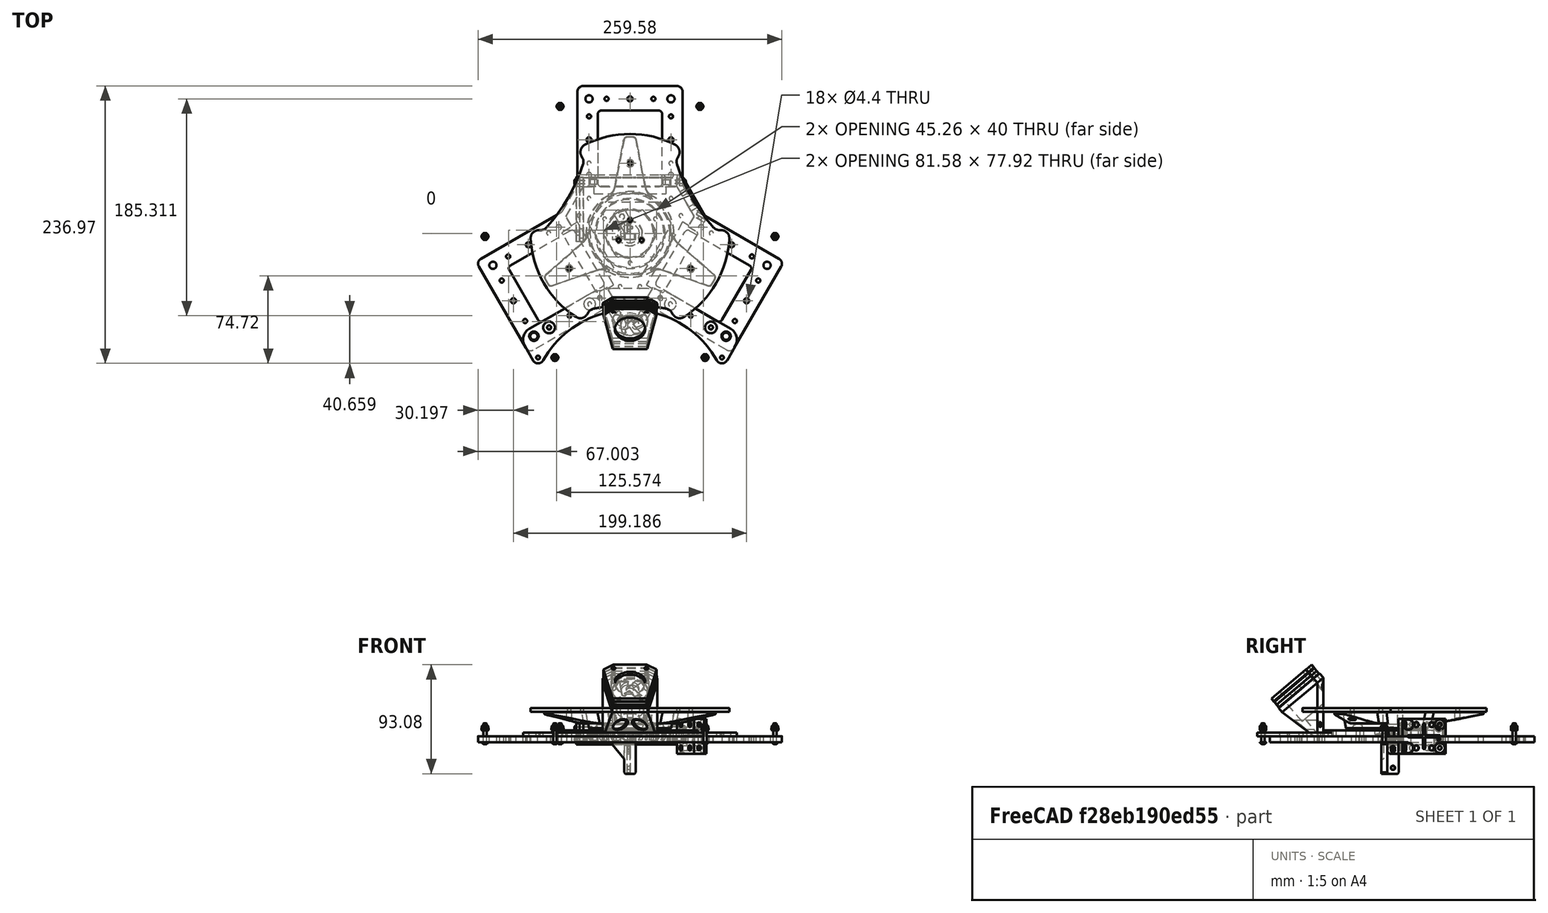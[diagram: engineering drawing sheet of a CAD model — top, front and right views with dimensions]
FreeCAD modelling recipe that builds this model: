
FCSTD DOCUMENT  (FreeCAD 2024.113R14555 (Git shallow))
Label: structures
License: Creative Commons Attribution-NoDerivatives
LicenseURL: http://creativecommons.org/licenses/by-nd/4.0/
objects: Sketcher::SketchObject×49, PartDesign::Pad×28, PartDesign::Pocket×26, PartDesign::Chamfer×25, PartDesign::Fillet×22, PartDesign::Body×20, App::Link×19, Part::FeaturePython×16, TechDraw::DrawProjGroupItem×14, TechDraw::DrawProjGroup×14, App::Part×12, TechDraw::DrawSVGTemplate×10, TechDraw::DrawPage×10, PartDesign::Mirrored×8, PartDesign::SubShapeBinder×7, PartDesign::PolarPattern×6, App::DocumentObjectGroup×6, TechDraw::DrawViewDimension×5, Part::SubShapeBinder×3, Part::Mirroring×2, +8 more types
note: 521 computed .brp shape members not serialized (recipe doc carries the construction recipe); baked Part::Feature solids carry a one-line shape summary decoded from their .brp
EXTERNAL_REF file=generic-hardware.FCStd obj=Part035
EXTERNAL_REF file=generic-hardware.FCStd obj=Part036
EXTERNAL_REF file=../robot_holonome.FCStd obj=Part

FEATURE [Sketcher::SketchObject] Sketch032
  ArcFitTolerance = 0
  AttachmentSupport = -> [XY_Plane026]
  ExternalBSplineMaxDegree = 0
  ExternalBSplineTolerance = 0
  FullyConstrained = true
  InternalTolerance = 1e-06
  InvalidShape = false
  MakeInternals = false
  MapMode = 5
  Support = -> [XY_Plane026]
  TreeRank = 0
  ValidateShape = true
  sketch-geometry (56):
    g0: LineSegment StartX=-131.619 StartY=-24.0289 StartZ=0 EndX=-58.007 EndY=18.4711 EndZ=0
    g1: LineSegment StartX=-58.007 StartY=18.4711 StartZ=0 EndX=-45 EndY=41 EndZ=0
    g2: LineSegment StartX=-45 StartY=41 StartZ=0 EndX=-45 EndY=126 EndZ=0
    g3: LineSegment StartX=-45 StartY=126 StartZ=0 EndX=45 EndY=126 EndZ=0
    g4: LineSegment StartX=45 StartY=126 StartZ=0 EndX=45 EndY=41 EndZ=0
    g5: LineSegment StartX=45 StartY=41 StartZ=0 EndX=58.007 EndY=18.4711 EndZ=0
    g6: LineSegment StartX=58.007 StartY=18.4711 StartZ=0 EndX=131.619 EndY=-24.0289 EndZ=0
    g7: LineSegment StartX=131.619 StartY=-24.0289 StartZ=0 EndX=86.6192 EndY=-101.971 EndZ=0
    g8: LineSegment StartX=86.6192 StartY=-101.971 StartZ=0 EndX=13.007 EndY=-59.4711 EndZ=0
    g9: LineSegment StartX=13.007 StartY=-59.4711 StartZ=0 EndX=-13.007 EndY=-59.4711 EndZ=0
    g10: LineSegment StartX=-13.007 StartY=-59.4711 StartZ=0 EndX=-86.6192 EndY=-101.971 EndZ=0
    g11: LineSegment StartX=-86.6192 StartY=-101.971 StartZ=0 EndX=-131.619 EndY=-24.0289 EndZ=0
    g12: LineSegment [constr] StartX=-1e-16 StartY=1e-16 StartZ=0 EndX=-1e-16 EndY=126 EndZ=0
    g13: LineSegment [constr] StartX=-1e-16 StartY=1e-16 StartZ=0 EndX=-109.119 EndY=-63 EndZ=0
    g14: LineSegment [constr] StartX=-1e-16 StartY=1e-16 StartZ=0 EndX=109.119 EndY=-63 EndZ=0
    g15: LineSegment StartX=-27.5 StartY=40 StartZ=0 EndX=27.5 EndY=40 EndZ=0
    g16: LineSegment StartX=27.5 StartY=40 StartZ=0 EndX=27.5 EndY=105 EndZ=0
    g17: LineSegment StartX=27.5 StartY=105 StartZ=0 EndX=-27.5 EndY=105 EndZ=0
    g18: LineSegment StartX=-27.5 StartY=105 StartZ=0 EndX=-27.5 EndY=40 EndZ=0
    g19: LineSegment StartX=20.891 StartY=-43.8157 StartZ=0 EndX=48.391 EndY=3.8157 EndZ=0
    g20: LineSegment StartX=48.391 StartY=3.8157 StartZ=0 EndX=104.683 EndY=-28.6843 EndZ=0
    g21: LineSegment StartX=104.683 StartY=-28.6843 StartZ=0 EndX=77.1827 EndY=-76.3157 EndZ=0
    g22: LineSegment StartX=77.1827 StartY=-76.3157 StartZ=0 EndX=20.891 EndY=-43.8157 EndZ=0
    g23: LineSegment StartX=-104.683 StartY=-28.6843 StartZ=0 EndX=-77.1827 EndY=-76.3157 EndZ=0
    g24: LineSegment StartX=-77.1827 StartY=-76.3157 StartZ=0 EndX=-20.891 EndY=-43.8157 EndZ=0
    g25: LineSegment StartX=-20.891 StartY=-43.8157 StartZ=0 EndX=-48.391 EndY=3.8157 EndZ=0
    g26: LineSegment StartX=-48.391 StartY=3.8157 StartZ=0 EndX=-104.683 EndY=-28.6843 EndZ=0
    g27: Circle [constr] CenterX=-1e-16 CenterY=1e-16 CenterZ=0 NormalX=0 NormalY=0 NormalZ=1 AngleXU=0 Radius=48.5412
    g28: LineSegment StartX=-11.547 StartY=-20 StartZ=0 EndX=-23.094 EndY=0 EndZ=0
    g29: LineSegment StartX=-23.094 StartY=-1.3e-15 StartZ=0 EndX=-11.547 EndY=20 EndZ=0
    g30: LineSegment StartX=-11.547 StartY=20 StartZ=0 EndX=11.547 EndY=20 EndZ=0
    g31: LineSegment StartX=11.547 StartY=20 StartZ=0 EndX=23.094 EndY=0 EndZ=0
    g32: LineSegment StartX=23.094 StartY=9e-16 StartZ=0 EndX=11.547 EndY=-20 EndZ=0
    g33: LineSegment StartX=11.547 StartY=-20 StartZ=0 EndX=-11.547 EndY=-20 EndZ=0
    g34: Circle [constr] CenterX=-1e-16 CenterY=1e-16 CenterZ=0 NormalX=0 NormalY=0 NormalZ=1 AngleXU=0 Radius=23.094
    g35: Circle CenterX=-21.6506 CenterY=12.5 CenterZ=0 NormalX=0 NormalY=0 NormalZ=1 AngleXU=0 Radius=1.6
    g36: Circle CenterX=21.6506 CenterY=12.5 CenterZ=0 NormalX=0 NormalY=0 NormalZ=1 AngleXU=0 Radius=1.6
    g37: Circle CenterX=0 CenterY=-25 CenterZ=0 NormalX=0 NormalY=0 NormalZ=1 AngleXU=0 Radius=1.6
    g38: LineSegment [constr] StartX=0 StartY=-25 StartZ=0 EndX=-1e-16 EndY=0 EndZ=0
    g39: LineSegment [constr] StartX=-1e-16 StartY=1e-16 StartZ=0 EndX=21.6506 EndY=12.5 EndZ=0
    g40: LineSegment [constr] StartX=-1e-16 StartY=1e-16 StartZ=0 EndX=-21.6506 EndY=12.5 EndZ=0
    g41: LineSegment [constr] StartX=-45 StartY=126 StartZ=0 EndX=-131.619 EndY=-24.0289 EndZ=0
    g42: LineSegment [constr] StartX=-86.6192 StartY=-101.971 StartZ=0 EndX=86.6192 EndY=-101.971 EndZ=0
    g43: LineSegment [constr] StartX=131.619 StartY=-24.0289 StartZ=0 EndX=45 EndY=126 EndZ=0
    g44: LineSegment [constr] StartX=-45 StartY=126 StartZ=0 EndX=-55 EndY=108.679 EndZ=0
    g45: LineSegment [constr] StartX=-55 StartY=108.679 StartZ=0 EndX=-45 EndY=41 EndZ=0
    g46: LineSegment [constr] StartX=-58.007 StartY=18.4711 StartZ=0 EndX=-121.619 EndY=-6.70835 EndZ=0
    g47: LineSegment [constr] StartX=-121.619 StartY=-6.70835 StartZ=0 EndX=-131.619 EndY=-24.0289 EndZ=0
    g48: LineSegment [constr] StartX=-86.6192 StartY=-101.971 StartZ=0 EndX=-66.6192 EndY=-101.971 EndZ=0
    g49: LineSegment [constr] StartX=-66.6192 StartY=-101.971 StartZ=0 EndX=-13.007 EndY=-59.4711 EndZ=0
    g50: LineSegment [constr] StartX=13.007 StartY=-59.4711 StartZ=0 EndX=66.6192 EndY=-101.971 EndZ=0
    g51: LineSegment [constr] StartX=66.6192 StartY=-101.971 StartZ=0 EndX=86.6192 EndY=-101.971 EndZ=0
    g52: LineSegment [constr] StartX=131.619 StartY=-24.0289 StartZ=0 EndX=121.619 EndY=-6.70835 EndZ=0
    g53: LineSegment [constr] StartX=121.619 StartY=-6.70835 StartZ=0 EndX=58.007 EndY=18.4711 EndZ=0
    g54: LineSegment [constr] StartX=45 StartY=41 StartZ=0 EndX=55 EndY=108.679 EndZ=0
    g55: LineSegment [constr] StartX=55 StartY=108.679 StartZ=0 EndX=45 EndY=126 EndZ=0
  constraints (151):
    c: Coincident(g0,g1)
    c: Coincident(g1,g2)
    c: Vertical(g2)
    c: Coincident(g2,g3)
    c: Horizontal(g3)
    c: Coincident(g3,g4)
    c: Vertical(g4)
    c: Coincident(g4,g5)
    c: Coincident(g5,g6)
    c: Coincident(g6,g7)
    c: Coincident(g7,g8)
    c: Coincident(g8,g9)
    c: Horizontal(g9)
    c: Coincident(g9,g10)
    c: Coincident(g10,g11)
    c: Coincident(g11,g0)
    c: Parallel(g8,g6)
    c: Parallel(g10,g0)
    c: Equal(g4,g6)
    c: Equal(g6,g8)
    c: Equal(g8,g10)
    c: Equal(g10,g0)
    c: Equal(g0,g2)
    c: Perpendicular(g6,g7)
    c: Perpendicular(g11,g10)
    c: Coincident(g12,g-1)
    c: PointOnObject(g12,g3)
    c: Vertical(g12)
    c: Coincident(g13,g12)
    c: Coincident(g14,g12)
    c: Symmetric(g6,g7,g14)
    c: Symmetric(g10,g0,g13)
    c: Perpendicular(g13,g11)
    c: Perpendicular(g7,g14)
    c: DistanceX(g3,g3) = 90
    c: Equal(g9,g5)
    c: Equal(g5,g1)
    c: Angle(g14,g12) = 2.0944
    c: Angle(g12,g13) = 2.0944
    c: DistanceY(g12,g2) = 126
    c: DistanceX(g9,g9) = 26.0141
    c: Coincident(g15,g16)
    c: Coincident(g16,g17)
    c: Coincident(g17,g18)
    c: Coincident(g18,g15)
    c: Horizontal(g15)
    c: Vertical(g16)
    c: Vertical(g18)
    c: Symmetric(g16,g17,g12)
    c: DistanceX(g17,g17) = 55
    c: DistanceY(g16,g16) = 65
    c: Coincident(g19,g20)
    c: Coincident(g20,g21)
    c: Coincident(g21,g22)
    c: Coincident(g22,g19)
    c: Coincident(g23,g24)
    c: Coincident(g24,g25)
    c: Coincident(g25,g26)
    c: Coincident(g26,g23)
    c: Equal(g25,g23)
    c: Equal(g23,g19)
    c: Equal(g19,g21)
    c: Equal(g21,g15)
    c: Equal(g22,g20)
    c: Equal(g20,g16)
    c: Equal(g16,g26)
    c: Equal(g26,g24)
    c: Parallel(g24,g13)
    c: Parallel(g22,g14)
    c: Symmetric(g23,g23,g13)
    c: Symmetric(g21,g20,g14)
    c: Coincident(g27,g12)
    c: PointOnObject(g19,g27)
    c: PointOnObject(g24,g27)
    c: PointOnObject(g15,g27)
    c: Equal(g11,g7)
    c: Equal(g7,g3)
    c: Coincident(g28,g29)
    c: Coincident(g29,g30)
    c: Coincident(g30,g31)
    c: Coincident(g31,g32)
    c: Coincident(g32,g33)
    c: Coincident(g33,g28)
    c: Horizontal(g33)
    c: Horizontal(g30)
    c: Equal(g29,g30)
    c: Equal(g30,g31)
    c: Equal(g31,g32)
    c: Equal(g32,g33)
    c: Equal(g33,g28)
    c: Coincident(g34,g12)
    c: PointOnObject(g30,g34)
    c: PointOnObject(g31,g34)
    c: PointOnObject(g32,g34)
    c: PointOnObject(g28,g34)
    c: PointOnObject(g28,g34)
    c: DistanceY(g12,g30) = 20
    c: PointOnObject(g37,g-2)
    c: Equal(g37,g36)
    c: Equal(g36,g35)
    c: Diameter(g35) = 3.2
    c: Coincident(g38,g37)
    c: Coincident(g38,g12)
    c: Coincident(g39,g12)
    c: Coincident(g39,g36)
    c: Coincident(g40,g12)
    c: Coincident(g40,g35)
    c: Perpendicular(g29,g40)
    c: Perpendicular(g31,g39)
    c: Equal(g40,g38)
    c: Equal(g38,g39)
    c: DistanceY(g38,g38) = 25
    c: Coincident(g41,g3)
    c: Coincident(g41,g11)
    c: Coincident(g42,g11)
    c: Coincident(g42,g7)
    c: Coincident(g43,g7)
    c: Coincident(g43,g3)
    c: Coincident(g3,g44)
    c: PointOnObject(g44,g41)
    c: Coincident(g44,g45)
    c: Coincident(g45,g1)
    c: Coincident(g1,g46)
    c: PointOnObject(g46,g41)
    c: Coincident(g46,g47)
    c: Coincident(g47,g11)
    c: Coincident(g11,g48)
    c: Horizontal(g48)
    c: Coincident(g48,g49)
    c: Coincident(g49,g9)
    c: Coincident(g9,g50)
    c: PointOnObject(g50,g42)
    c: Coincident(g50,g51)
    c: Coincident(g51,g7)
    c: Coincident(g7,g52)
    c: PointOnObject(g52,g43)
    c: Coincident(g52,g53)
    c: Coincident(g53,g5)
    c: Coincident(g5,g54)
    c: PointOnObject(g54,g43)
    c: Coincident(g54,g55)
    c: Coincident(g55,g3)
    c: Equal(g55,g44)
    c: Equal(g44,g47)
    c: Equal(g47,g48)
    c: Equal(g48,g51)
    c: Equal(g55,g52)
    c: DistanceX(g48,g48) = 20
    c: DistanceY(g16) = 105
    c: DistanceY(g50,g12) = 101.971
    c: DistanceY(g4,g4) = 85
FEATURE [PartDesign::Pad] Pad020
  AddSubType = 0
  AutoTaperInnerAngle = false
  CheckUpToFaceLimits = true
  ClaimChildren = false
  Direction = (0,0,1)
  Fit = 0
  FitJoin = 0
  InnerFit = 0
  InnerFitJoin = 0
  InvalidShape = false
  Length = 5
  Length2 = 100
  Linearize = true
  NewSolid = false
  Profile = -> Sketch032
  Refine = true
  Reversed = true
  Suppress = false
  TaperInnerAngle = 0
  TaperInnerAngleRev = 0
  TreeRank = 0
  Type = 0
  ValidateShape = true
  _ProfileBasedVersion = 1
FEATURE [PartDesign::Fillet] Fillet008
  AddSubType = 0
  Base = -> Pad020 [Edge41,Edge44,Edge37,Edge38,Edge65,Edge62,Edge61,Edge68,Edge49,Edge50,Edge53,Edge56]
  BaseFeature = -> Pad020
  InvalidShape = false
  NewSolid = false
  Radius = 3
  Refine = true
  SupportTransform = false
  Suppress = false
  TreeRank = 0
  UseAllEdges = false
  ValidateShape = true
FEATURE [PartDesign::Fillet] Fillet009
  AddSubType = 0
  Base = -> Fillet008 [Edge110,Edge99,Edge107,Edge106,Edge102,Edge103]
  BaseFeature = -> Fillet008
  InvalidShape = false
  NewSolid = false
  Radius = 5
  Refine = true
  SupportTransform = false
  Suppress = false
  TreeRank = 0
  UseAllEdges = false
  ValidateShape = true
FEATURE [PartDesign::Fillet] Fillet010
  AddSubType = 0
  Base = -> Fillet009 [Edge53,Edge57,Edge67,Edge71,Edge77,Edge81]
  BaseFeature = -> Fillet009
  InvalidShape = false
  NewSolid = false
  Radius = 5
  Refine = true
  SupportTransform = false
  Suppress = false
  TreeRank = 0
  UseAllEdges = false
  ValidateShape = true
FEATURE [Sketcher::SketchObject] Sketch033
  ArcFitTolerance = 0
  AttachmentSupport = -> [XY_Plane026]
  ExternalBSplineMaxDegree = 0
  ExternalBSplineTolerance = 0
  FullyConstrained = true
  InternalTolerance = 1e-06
  InvalidShape = false
  MakeInternals = false
  MapMode = 5
  Support = -> [XY_Plane026]
  TreeRank = 0
  ValidateShape = true
  sketch-geometry (13):
    g0: Circle CenterX=-20 CenterY=115 CenterZ=0 NormalX=0 NormalY=0 NormalZ=1 AngleXU=0 Radius=1.75
    g1: Circle CenterX=20 CenterY=115 CenterZ=0 NormalX=0 NormalY=0 NormalZ=1 AngleXU=0 Radius=1.75
    g2: Circle CenterX=-35 CenterY=60 CenterZ=0 NormalX=0 NormalY=0 NormalZ=1 AngleXU=0 Radius=1.75
    g3: Circle CenterX=-35 CenterY=100 CenterZ=0 NormalX=0 NormalY=0 NormalZ=1 AngleXU=0 Radius=1.75
    g4: Circle CenterX=35 CenterY=100 CenterZ=0 NormalX=0 NormalY=0 NormalZ=1 AngleXU=0 Radius=1.75
    g5: Circle CenterX=35 CenterY=60 CenterZ=0 NormalX=0 NormalY=0 NormalZ=1 AngleXU=0 Radius=1.75
    g6: Circle CenterX=-35 CenterY=115 CenterZ=0 NormalX=0 NormalY=0 NormalZ=1 AngleXU=0 Radius=3.1
    g7: Circle CenterX=35 CenterY=115 CenterZ=0 NormalX=0 NormalY=0 NormalZ=1 AngleXU=0 Radius=3.1
    g8: Circle CenterX=-35 CenterY=80 CenterZ=0 NormalX=0 NormalY=0 NormalZ=1 AngleXU=0 Radius=2.2
    g9: Circle CenterX=35 CenterY=80 CenterZ=0 NormalX=0 NormalY=0 NormalZ=1 AngleXU=0 Radius=2.2
    g10: Circle CenterX=-35 CenterY=50 CenterZ=0 NormalX=0 NormalY=0 NormalZ=1 AngleXU=0 Radius=2.2
    g11: Circle CenterX=35 CenterY=50 CenterZ=0 NormalX=0 NormalY=0 NormalZ=1 AngleXU=0 Radius=2.2
    g12: Circle CenterX=-1.0206e-12 CenterY=115 CenterZ=0 NormalX=0 NormalY=0 NormalZ=1 AngleXU=0 Radius=2.2
  constraints (31):
    c: Equal(g0,g3)
    c: Equal(g3,g2)
    c: Equal(g2,g1)
    c: Equal(g1,g4)
    c: Equal(g4,g5)
    c: Diameter(g0) = 3.5
    c: Symmetric(g1,g0,g-2)
    c: Symmetric(g3,g4,g-2)
    c: Symmetric(g2,g5,g-2)
    c: Vertical(g3,g2)
    c: DistanceX(g3,g4) = 70
    c: DistanceX(g0,g1) = 40
    c: DistanceY(g4,g1) = 15
    c: DistanceY(g5,g4) = 40
    c: DistanceY(g-1,g1) = 115
    c: Symmetric(g7,g6,g-2)
    c: Horizontal(g6,g0)
    c: Diameter(g7) = 6.2
    c: Equal(g7,g6)
    c: Vertical(g7,g4)
    c: Equal(g9,g8)
    c: Symmetric(g8,g9,g-2)
    c: Symmetric(g5,g4,g9)
    c: Diameter(g9) = 4.4
    c: Symmetric(g1,g0,g12)
    c: Equal(g12,g11)
    c: Equal(g11,g10)
    c: Equal(g10,g9)
    c: Vertical(g11,g5)
    c: Symmetric(g11,g10,g-2)
    c: DistanceY(g11,g5) = 10
FEATURE [PartDesign::Pocket] Pocket012
  AddSubType = 1
  AutoTaperInnerAngle = false
  BaseFeature = -> Fillet010
  CheckUpToFaceLimits = true
  ClaimChildren = false
  Direction = (1,1,1)
  Fit = 0
  FitJoin = 0
  InnerFit = 0
  InnerFitJoin = 0
  InvalidShape = false
  Length = 5
  Length2 = 100
  Linearize = true
  NewSolid = false
  Profile = -> Sketch033
  Refine = true
  Suppress = false
  TaperInnerAngle = 0
  TaperInnerAngleRev = 0
  TreeRank = 0
  Type = 1
  ValidateShape = true
  _ProfileBasedVersion = 1
  _Version = 0
FEATURE [PartDesign::PolarPattern] PolarPattern013
  AddSubType = 0
  Angle = 360
  Axis = -> Sketch033 [N_Axis]
  BaseFeature = -> Pocket012
  CopyShape = false
  InvalidShape = false
  NewSolid = false
  Occurrences = 3
  OriginalSubs = -> [Pocket012]
  Originals = -> [Pocket012]
  ParallelTransform = true
  Refine = true
  SubTransform = true
  Suppress = false
  TreeRank = 0
  ValidateShape = true
  _Version = 0
FEATURE [PartDesign::Fillet] Fillet011
  AddSubType = 0
  Base = -> PolarPattern013 [Edge190,Edge189,Edge192,Edge196,Edge198,Edge194]
  BaseFeature = -> PolarPattern013
  InvalidShape = false
  NewSolid = false
  Radius = 3
  Refine = true
  SupportTransform = false
  Suppress = false
  TreeRank = 0
  UseAllEdges = false
  ValidateShape = true
FEATURE [PartDesign::Body] Body019  label="Semelle"
  AutoGroupSolids = false
  ClaimAllChildren = false
  ExportMode = 0
  Group = -> [Sketch032,Pad020,Fillet008,Fillet009,Fillet010,Sketch033,Pocket012,PolarPattern013,Fillet011]
  InvalidShape = false
  Origin = -> Origin029
  SingleSolid = true
  Tip = -> Fillet011
  TreeRank = 0
  ValidateShape = true
  _ExportChildren = -> [Pad020,Fillet008,Fillet009,Fillet010,Pocket012,PolarPattern013,Fillet011]
  _GroupVersion = 1
FEATURE [Sketcher::SketchObject] Sketch034
  ArcFitTolerance = 0
  AttachmentSupport = -> [XY_Plane027]
  ExternalBSplineMaxDegree = 0
  ExternalBSplineTolerance = 0
  FullyConstrained = true
  InternalTolerance = 1e-06
  InvalidShape = false
  MakeInternals = false
  MapMode = 5
  Support = -> [XY_Plane027]
  TreeRank = 0
  ValidateShape = true
  sketch-geometry (33):
    g0: LineSegment StartX=-54.641 StartY=14.641 StartZ=0 EndX=-40 EndY=40 EndZ=0
    g1: LineSegment StartX=-40 StartY=40 StartZ=0 EndX=-31 EndY=40 EndZ=0
    g2: LineSegment StartX=-31 StartY=40 StartZ=0 EndX=-31 EndY=34 EndZ=0
    g3: LineSegment StartX=-31 StartY=34 StartZ=0 EndX=31 EndY=34 EndZ=0
    g4: LineSegment StartX=31 StartY=34 StartZ=0 EndX=31 EndY=40 EndZ=0
    g5: LineSegment StartX=31 StartY=40 StartZ=0 EndX=40 EndY=40 EndZ=0
    g6: LineSegment StartX=40 StartY=40 StartZ=0 EndX=54.641 EndY=14.641 EndZ=0
    g7: LineSegment StartX=54.641 StartY=14.641 StartZ=0 EndX=50.141 EndY=6.84679 EndZ=0
    g8: LineSegment StartX=50.141 StartY=6.84679 StartZ=0 EndX=44.9449 EndY=9.84679 EndZ=0
    g9: LineSegment StartX=44.9449 StartY=9.84679 StartZ=0 EndX=13.9449 EndY=-43.8468 EndZ=0
    g10: LineSegment StartX=13.9449 StartY=-43.8468 StartZ=0 EndX=19.141 EndY=-46.8468 EndZ=0
    g11: LineSegment StartX=19.141 StartY=-46.8468 StartZ=0 EndX=14.641 EndY=-54.641 EndZ=0
    g12: LineSegment StartX=14.641 StartY=-54.641 StartZ=0 EndX=-14.641 EndY=-54.641 EndZ=0
    g13: LineSegment StartX=-14.641 StartY=-54.641 StartZ=0 EndX=-19.141 EndY=-46.8468 EndZ=0
    g14: LineSegment StartX=-19.141 StartY=-46.8468 StartZ=0 EndX=-13.9449 EndY=-43.8468 EndZ=0
    g15: LineSegment StartX=-13.9449 StartY=-43.8468 StartZ=0 EndX=-44.9449 EndY=9.84679 EndZ=0
    g16: LineSegment StartX=-44.9449 StartY=9.84679 StartZ=0 EndX=-50.141 EndY=6.84679 EndZ=0
    g17: LineSegment StartX=-50.141 StartY=6.84679 StartZ=0 EndX=-54.641 EndY=14.641 EndZ=0
    g18: Circle [constr] CenterX=0 CenterY=0 CenterZ=0 NormalX=0 NormalY=0 NormalZ=1 AngleXU=0 Radius=56.5685
    g19: Circle [constr] CenterX=0 CenterY=0 CenterZ=0 NormalX=0 NormalY=0 NormalZ=1 AngleXU=0 Radius=25
    g20: Circle CenterX=-21.6506 CenterY=12.5 CenterZ=0 NormalX=0 NormalY=0 NormalZ=1 AngleXU=0 Radius=1.6
    g21: Circle CenterX=21.6506 CenterY=12.5 CenterZ=0 NormalX=0 NormalY=0 NormalZ=1 AngleXU=0 Radius=1.6
    g22: Circle CenterX=0 CenterY=-25 CenterZ=0 NormalX=0 NormalY=0 NormalZ=1 AngleXU=0 Radius=1.6
    g23: LineSegment [constr] StartX=0 StartY=0 StartZ=0 EndX=21.6506 EndY=12.5 EndZ=0
    g24: LineSegment [constr] StartX=0 StartY=0 StartZ=0 EndX=0 EndY=-25 EndZ=0
    g25: LineSegment [constr] StartX=0 StartY=0 StartZ=0 EndX=-21.6506 EndY=12.5 EndZ=0
    g26: LineSegment StartX=11.547 StartY=20 StartZ=0 EndX=-11.547 EndY=20 EndZ=0
    g27: LineSegment StartX=-11.547 StartY=20 StartZ=0 EndX=-23.094 EndY=1.0409e-12 EndZ=0
    g28: LineSegment StartX=-23.094 StartY=1.0409e-12 StartZ=0 EndX=-11.547 EndY=-20 EndZ=0
    g29: LineSegment StartX=-11.547 StartY=-20 StartZ=0 EndX=11.547 EndY=-20 EndZ=0
    g30: LineSegment StartX=11.547 StartY=-20 StartZ=0 EndX=23.094 EndY=1.0374e-12 EndZ=0
    g31: LineSegment StartX=23.094 StartY=1.0374e-12 StartZ=0 EndX=11.547 EndY=20 EndZ=0
    g32: Circle [constr] CenterX=0 CenterY=0 CenterZ=0 NormalX=0 NormalY=0 NormalZ=1 AngleXU=0 Radius=23.094
  constraints (88):
    c: Coincident(g0,g1)
    c: Horizontal(g1)
    c: Coincident(g1,g2)
    c: Vertical(g2)
    c: Coincident(g2,g3)
    c: Coincident(g3,g4)
    c: Vertical(g4)
    c: Coincident(g4,g5)
    c: Horizontal(g5)
    c: Coincident(g5,g6)
    c: Coincident(g6,g7)
    c: Coincident(g7,g8)
    c: Coincident(g8,g9)
    c: Coincident(g9,g10)
    c: Coincident(g10,g11)
    c: Coincident(g11,g12)
    c: Horizontal(g12)
    c: Coincident(g12,g13)
    c: Coincident(g13,g14)
    c: Coincident(g14,g15)
    c: Coincident(g15,g16)
    c: Coincident(g16,g17)
    c: Coincident(g17,g0)
    c: DistanceY(g-1,g1) = 40
    c: DistanceX(g1,g1) = 9
    c: Equal(g5,g1)
    c: Equal(g1,g17)
    c: Equal(g17,g13)
    c: Equal(g13,g11)
    c: Equal(g11,g7)
    c: Perpendicular(g10,g11)
    c: Perpendicular(g14,g13)
    c: Perpendicular(g15,g14)
    c: Perpendicular(g9,g10)
    c: Perpendicular(g9,g8)
    c: Perpendicular(g8,g7)
    c: Perpendicular(g17,g16)
    c: Perpendicular(g15,g16)
    c: DistanceY(g2,g2) = 6
    c: Equal(g8,g4)
    c: Equal(g4,g16)
    c: Equal(g0,g6)
    c: Equal(g6,g12)
    c: Coincident(g18,g-1)
    c: PointOnObject(g5,g18)
    c: PointOnObject(g6,g18)
    c: PointOnObject(g11,g18)
    c: PointOnObject(g12,g18)
    c: PointOnObject(g0,g18)
    c: PointOnObject(g0,g18)
    c: Symmetric(g3,g2,g-2)
    c: DistanceX(g3,g3) = 62
    c: Angle(g15,g3) = 1.0472
    c: Angle(g3,g9) = 1.0472
    c: Equal(g10,g8)
    c: Coincident(g19,g18)
    c: PointOnObject(g20,g19)
    c: PointOnObject(g21,g19)
    c: PointOnObject(g22,g19)
    c: PointOnObject(g22,g-2)
    c: Coincident(g23,g18)
    c: Coincident(g23,g21)
    c: Coincident(g24,g18)
    c: Coincident(g24,g22)
    c: Coincident(g25,g18)
    c: Coincident(g25,g20)
    c: Angle(g23,g25) = 2.0944
    c: Angle(g24,g23) = 2.0944
    c: DistanceY(g24,g24) = 25
    c: Equal(g21,g22)
    c: Equal(g22,g20)
    c: Diameter(g21) = 3.2
    c: Coincident(g26,g27)
    c: Coincident(g27,g28)
    c: Coincident(g28,g29)
    c: Coincident(g29,g30)
    c: Coincident(g30,g31)
    c: Coincident(g31,g26)
    c: Equal(g26, g27-g31) x5
    c: PointOnObject(g26,g32)
    c: PointOnObject(g27,g32)
    c: PointOnObject(g28,g32)
    c: PointOnObject(g29,g32)
    c: PointOnObject(g30,g32)
    c: PointOnObject(g31,g32)
    c: Coincident(g32,g18)
    c: Horizontal(g26)
    c: DistanceY(g26) = 20
FEATURE [PartDesign::Pad] Pad021
  AddSubType = 0
  AutoTaperInnerAngle = false
  CheckUpToFaceLimits = true
  ClaimChildren = false
  Direction = (1,1,1)
  Fit = 0
  FitJoin = 0
  InnerFit = 0
  InnerFitJoin = 0
  InvalidShape = false
  Length = 5
  Length2 = 100
  Linearize = true
  NewSolid = false
  Profile = -> Sketch034
  Refine = true
  Suppress = false
  TaperInnerAngle = 0
  TaperInnerAngleRev = 0
  TreeRank = 0
  Type = 0
  ValidateShape = true
  _ProfileBasedVersion = 1
FEATURE [PartDesign::Fillet] Fillet012
  AddSubType = 0
  Base = -> Pad021 [Edge59,Edge56,Edge68,Edge55,Edge65,Edge62]
  BaseFeature = -> Pad021
  InvalidShape = false
  NewSolid = false
  Radius = 3
  Refine = true
  SupportTransform = false
  Suppress = false
  TreeRank = 0
  UseAllEdges = false
  ValidateShape = true
FEATURE [PartDesign::Fillet] Fillet013
  AddSubType = 0
  Base = -> Fillet012 [Edge94,Edge93,Edge95,Edge96,Edge81,Edge82,Edge84,Edge83,Edge88,Edge87,Edge86,Edge85,Edge80,Edge79,Edge92,Edge91,Edge90,Edge89]
  BaseFeature = -> Fillet012
  InvalidShape = false
  NewSolid = false
  Radius = 0.5
  Refine = true
  SupportTransform = false
  Suppress = false
  TreeRank = 0
  UseAllEdges = false
  ValidateShape = true
FEATURE [PartDesign::Body] Body020  label="CaleCentrale"
  AutoGroupSolids = false
  ClaimAllChildren = false
  ExportMode = 0
  Group = -> [Sketch034,Pad021,Fillet012,Fillet013]
  InvalidShape = false
  Origin = -> Origin030
  SingleSolid = true
  Tip = -> Fillet013
  TreeRank = 0
  ValidateShape = true
  _ExportChildren = -> [Pad021,Fillet012,Fillet013]
  _GroupVersion = 1
FEATURE [Sketcher::SketchObject] Sketch043
  ArcFitTolerance = 0
  AttachmentSupport = -> [XY_Plane031]
  ExternalBSplineMaxDegree = 0
  ExternalBSplineTolerance = 0
  FullyConstrained = true
  InternalTolerance = 1e-06
  InvalidShape = false
  MakeInternals = false
  MapMode = 5
  Support = -> [XY_Plane031]
  TreeRank = 0
  ValidateShape = true
  sketch-geometry (13):
    g0: LineSegment StartX=0 StartY=0 StartZ=0 EndX=0 EndY=-54.641 EndZ=0
    g1: LineSegment StartX=0 StartY=-54.641 StartZ=0 EndX=-14.641 EndY=-54.641 EndZ=0
    g2: LineSegment StartX=-14.641 StartY=-54.641 StartZ=0 EndX=-19.641 EndY=-45.9808 EndZ=0
    g3: LineSegment StartX=-19.641 StartY=-45.9808 StartZ=0 EndX=-28.3013 EndY=-50.9808 EndZ=0
    g4: LineSegment StartX=-28.3013 StartY=-50.9808 StartZ=0 EndX=-58.3013 EndY=0.980762 EndZ=0
    g5: LineSegment StartX=-58.3013 StartY=0.980762 StartZ=0 EndX=-49.641 EndY=5.98076 EndZ=0
    g6: LineSegment StartX=-49.641 StartY=5.98076 StartZ=0 EndX=-54.641 EndY=14.641 EndZ=0
    g7: LineSegment StartX=-54.641 StartY=14.641 StartZ=0 EndX=-47.3205 EndY=27.3205 EndZ=0
    g8: LineSegment StartX=-47.3205 StartY=27.3205 StartZ=0 EndX=0 EndY=0 EndZ=0
    g9: LineSegment [constr] StartX=-49.641 StartY=5.98076 StartZ=0 EndX=-19.641 EndY=-45.9808 EndZ=0
    g10: Circle CenterX=-43.4808 CenterY=15.3109 CenterZ=0 NormalX=0 NormalY=0 NormalZ=1 AngleXU=0 Radius=1.6
    g11: Circle CenterX=-8.48076 CenterY=-45.3109 CenterZ=0 NormalX=0 NormalY=0 NormalZ=1 AngleXU=0 Radius=1.6
    g12: LineSegment [constr] StartX=0 StartY=0 StartZ=0 EndX=-43.3013 EndY=-25 EndZ=0
  constraints (35):
    c: Coincident(g0,g-1)
    c: PointOnObject(g0,g-2)
    c: Coincident(g1,g0)
    c: Horizontal(g1)
    c: Coincident(g1,g2)
    c: Coincident(g2,g3)
    c: Coincident(g3,g4)
    c: Coincident(g4,g5)
    c: Coincident(g5,g6)
    c: Coincident(g6,g7)
    c: Coincident(g7,g8)
    c: Coincident(g8,g0)
    c: Angle(g8,g0) = 2.0944
    c: Perpendicular(g7,g8)
    c: Perpendicular(g3,g2)
    c: Perpendicular(g4,g3)
    c: Perpendicular(g4,g5)
    c: Perpendicular(g6,g5)
    c: Equal(g7,g1)
    c: Coincident(g9,g5)
    c: Tangent(g9,g2) = 1.5708
    c: Equal(g2,g3)
    c: Equal(g5,g6)
    c: Distance(g6) = 10
    c: Equal(g0,g8)
    c: Distance(g4) = 60
    c: Distance(g0,g9) = 40
    c: Coincident(g12,g0)
    c: PointOnObject(g12,g4)
    c: Perpendicular(g4,g12)
    c: Symmetric(g11,g10,g12)
    c: Diameter(g10) = 3.2
    c: Equal(g10,g11)
    c: Distance(g11,g2) = 10
    c: Distance(g11,g12) = 35
FEATURE [PartDesign::Pad] Pad027
  AddSubType = 0
  AutoTaperInnerAngle = false
  CheckUpToFaceLimits = true
  ClaimChildren = false
  Direction = (1,1,1)
  Fit = 0
  FitJoin = 0
  InnerFit = 0
  InnerFitJoin = 0
  InvalidShape = false
  Length = 5
  Length2 = 100
  Linearize = true
  NewSolid = false
  Profile = -> Sketch043
  Refine = true
  Suppress = false
  TaperInnerAngle = 0
  TaperInnerAngleRev = 0
  TreeRank = 0
  Type = 0
  ValidateShape = true
  _ProfileBasedVersion = 1
FEATURE [PartDesign::PolarPattern] PolarPattern014
  AddSubType = 0
  Angle = 360
  Axis = -> Sketch043 [N_Axis]
  BaseFeature = -> Pad027
  CopyShape = false
  InvalidShape = false
  NewSolid = false
  Occurrences = 3
  OriginalSubs = -> [Pad027]
  Originals = -> [Pad027]
  ParallelTransform = true
  Refine = true
  SubTransform = true
  Suppress = false
  TreeRank = 0
  ValidateShape = true
  _Version = 2
FEATURE [Sketcher::SketchObject] Sketch044
  ArcFitTolerance = 0
  AttachmentSupport = -> [XY_Plane031]
  ExternalBSplineMaxDegree = 0
  ExternalBSplineTolerance = 0
  FullyConstrained = true
  InternalTolerance = 1e-06
  InvalidShape = false
  MakeInternals = false
  MapMode = 5
  Support = -> [XY_Plane031]
  TreeRank = 0
  ValidateShape = true
  sketch-geometry (5):
    g0: LineSegment StartX=-35.6218 StartY=8.30127 StartZ=0 EndX=-10.6218 EndY=-35 EndZ=0
    g1: LineSegment StartX=-10.6218 StartY=-35 StartZ=0 EndX=0 EndY=-35 EndZ=0
    g2: LineSegment StartX=0 StartY=-35 StartZ=0 EndX=0 EndY=0 EndZ=0
    g3: LineSegment StartX=0 StartY=0 StartZ=0 EndX=-30.3109 EndY=17.5 EndZ=0
    g4: LineSegment StartX=-30.3109 StartY=17.5 StartZ=0 EndX=-35.6218 EndY=8.30127 EndZ=0
  constraints (14):
    c: Coincident(g0,g1)
    c: PointOnObject(g1,g-2)
    c: Horizontal(g1)
    c: Coincident(g1,g2)
    c: Coincident(g2,g-1)
    c: Coincident(g2,g3)
    c: Coincident(g3,g4)
    c: Coincident(g4,g0)
    c: Perpendicular(g4,g3)
    c: Equal(g4,g1)
    c: Equal(g2,g3)
    c: Angle(g3,g2) = 2.0944
    c: Distance(g0) = 50
    c: DistanceY(g2,g2) = 35
FEATURE [PartDesign::Pocket] Pocket017
  AddSubType = 1
  AutoTaperInnerAngle = false
  BaseFeature = -> PolarPattern014
  CheckUpToFaceLimits = true
  ClaimChildren = false
  Direction = (1,1,1)
  Fit = 0
  FitJoin = 0
  InnerFit = 0
  InnerFitJoin = 0
  InvalidShape = false
  Length = 5
  Length2 = 100
  Linearize = true
  NewSolid = false
  Profile = -> Sketch044
  Refine = true
  Reversed = true
  Suppress = false
  TaperInnerAngle = 0
  TaperInnerAngleRev = 0
  TreeRank = 0
  Type = 1
  ValidateShape = true
  _ProfileBasedVersion = 1
  _Version = 0
FEATURE [PartDesign::PolarPattern] PolarPattern015
  AddSubType = 0
  Angle = 360
  Axis = -> Sketch044 [N_Axis]
  BaseFeature = -> Pocket017
  CopyShape = false
  InvalidShape = false
  NewSolid = false
  Occurrences = 3
  OriginalSubs = -> [Pocket017]
  Originals = -> [Pocket017]
  ParallelTransform = true
  Refine = true
  SubTransform = true
  Suppress = false
  TreeRank = 0
  ValidateShape = true
  _Version = 2
FEATURE [PartDesign::Chamfer] Chamfer007
  AddSubType = 0
  Angle = 45
  Base = -> PolarPattern015 [Edge8,Edge66,Edge67,Edge68,Edge77,Edge78]
  BaseFeature = -> PolarPattern015
  ChamferType = 0
  FlipDirection = false
  InvalidShape = false
  NewSolid = false
  Refine = true
  Size = 1
  Size2 = 1
  SupportTransform = false
  Suppress = false
  TreeRank = 0
  UseAllEdges = false
  ValidateShape = true
FEATURE [PartDesign::Fillet] Fillet014
  AddSubType = 0
  Base = -> Chamfer007 [Edge101,Edge103,Edge104,Edge105,Edge106,Edge102]
  BaseFeature = -> Chamfer007
  InvalidShape = false
  NewSolid = false
  Radius = 3
  Refine = true
  SupportTransform = false
  Suppress = false
  TreeRank = 0
  UseAllEdges = false
  ValidateShape = true
FEATURE [PartDesign::Body] Body024  label="PlaqueIntermediaire"
  AutoGroupSolids = false
  ClaimAllChildren = false
  ExportMode = 0
  Group = -> [Sketch043,Pad027,PolarPattern014,Sketch044,Pocket017,PolarPattern015,Chamfer007,Fillet014]
  InvalidShape = false
  Origin = -> Origin036
  SingleSolid = true
  Tip = -> Fillet014
  TreeRank = 0
  ValidateShape = true
  _ExportChildren = -> [Pad027,PolarPattern014,Pocket017,PolarPattern015,Chamfer007,Fillet014]
  _GroupVersion = 1
FEATURE [Sketcher::SketchObject] Sketch037
  ArcFitTolerance = 0
  AttachmentSupport = -> [XZ_Plane030]
  ExternalBSplineMaxDegree = 0
  ExternalBSplineTolerance = 0
  FullyConstrained = true
  InternalTolerance = 1e-06
  InvalidShape = false
  MakeInternals = false
  MapMode = 5
  Placement = pos=(0,0,0) rot=(1,0,0;1.5708rad)
  Support = -> [XZ_Plane030]
  TreeRank = 0
  ValidateShape = true
  sketch-geometry (6):
    g0: LineSegment StartX=-5 StartY=0 StartZ=0 EndX=15 EndY=0 EndZ=0
    g1: LineSegment StartX=15 StartY=0 StartZ=0 EndX=15 EndY=-7 EndZ=0
    g2: LineSegment StartX=15 StartY=-7 StartZ=0 EndX=5 EndY=-7 EndZ=0
    g3: LineSegment StartX=5 StartY=-7 StartZ=0 EndX=5 EndY=-32 EndZ=0
    g4: LineSegment StartX=5 StartY=-32 StartZ=0 EndX=-5 EndY=-32 EndZ=0
    g5: LineSegment StartX=-5 StartY=-32 StartZ=0 EndX=-5 EndY=0 EndZ=0
  constraints (18):
    c: PointOnObject(g0,g-1)
    c: Horizontal(g0)
    c: Coincident(g0,g1)
    c: Vertical(g1)
    c: Coincident(g1,g2)
    c: Horizontal(g2)
    c: Coincident(g2,g3)
    c: Vertical(g3)
    c: Coincident(g3,g4)
    c: Horizontal(g4)
    c: Coincident(g4,g5)
    c: Coincident(g5,g0)
    c: Vertical(g5)
    c: DistanceY(g1,g1) = 7
    c: DistanceX(g-1,g2) = 5
    c: DistanceX(g2,g2) = 10
    c: DistanceY(g3,g3) = 25
    c: DistanceX(g0,g-1) = 5
FEATURE [PartDesign::Pad] Pad024
  AddSubType = 0
  AutoTaperInnerAngle = false
  CheckUpToFaceLimits = true
  ClaimChildren = false
  Direction = (1,1,1)
  Fit = 0
  FitJoin = 0
  InnerFit = 0
  InnerFitJoin = 0
  InvalidShape = false
  Length = 10
  Length2 = 100
  Linearize = true
  NewSolid = false
  Placement = pos=(0,0,0) rot=(1,0,0;1.5708rad)
  Profile = -> Sketch037
  Refine = true
  Reversed = true
  Suppress = false
  TaperInnerAngle = 0
  TaperInnerAngleRev = 0
  TreeRank = 0
  Type = 0
  ValidateShape = true
  _ProfileBasedVersion = 1
FEATURE [PartDesign::Pad] Pad025
  AddSubType = 0
  AutoTaperInnerAngle = false
  BaseFeature = -> Pad024
  CheckUpToFaceLimits = true
  ClaimChildren = false
  Direction = (1,1,1)
  Fit = 0
  FitJoin = 0
  InnerFit = 0
  InnerFitJoin = 0
  InvalidShape = false
  Length = 5
  Length2 = 100
  Linearize = true
  NewSolid = false
  Placement = pos=(0,0,0) rot=(1,0,0;1.5708rad)
  Profile = -> Sketch037
  Refine = true
  Suppress = false
  TaperInnerAngle = 0
  TaperInnerAngleRev = 0
  TreeRank = 0
  Type = 0
  ValidateShape = true
  _ProfileBasedVersion = 1
FEATURE [Sketcher::SketchObject] Sketch038
  ArcFitTolerance = 0
  AttachmentSupport = -> [XZ_Plane030]
  ExternalBSplineMaxDegree = 0
  ExternalBSplineTolerance = 0
  ExternalGeometry = -> [Pad025]
  FullyConstrained = true
  InternalTolerance = 1e-06
  InvalidShape = false
  MakeInternals = false
  MapMode = 5
  Placement = pos=(0,0,0) rot=(1,0,0;1.5708rad)
  Support = -> [XZ_Plane030]
  TreeRank = 0
  ValidateShape = true
  sketch-geometry (4):
    g0: LineSegment StartX=0 StartY=0 StartZ=0 EndX=-5 EndY=0 EndZ=0
    g1: LineSegment StartX=-5 StartY=0 StartZ=0 EndX=-5 EndY=-32 EndZ=0
    g2: LineSegment StartX=-5 StartY=-32 StartZ=0 EndX=0 EndY=-32 EndZ=0
    g3: LineSegment StartX=0 StartY=-32 StartZ=0 EndX=0 EndY=0 EndZ=0
  constraints (10):
    c: Coincident(g0,g1)
    c: Coincident(g1,g2)
    c: Coincident(g2,g3)
    c: Coincident(g3,g0)
    c: Horizontal(g0)
    c: Horizontal(g2)
    c: Vertical(g1)
    c: Vertical(g3)
    c: Coincident(g0,g-1)
    c: Coincident(g-3,g1)
FEATURE [PartDesign::Pocket] Pocket013
  AddSubType = 1
  AutoTaperInnerAngle = false
  BaseFeature = -> Pad025
  CheckUpToFaceLimits = true
  ClaimChildren = false
  Direction = (1,1,1)
  Fit = 0
  FitJoin = 0
  InnerFit = 0
  InnerFitJoin = 0
  InvalidShape = false
  Length = 5
  Length2 = 100
  Linearize = true
  NewSolid = false
  Placement = pos=(0,0,0) rot=(1,0,0;1.5708rad)
  Profile = -> Sketch038
  Refine = true
  Suppress = false
  TaperInnerAngle = 0
  TaperInnerAngleRev = 0
  TreeRank = 0
  Type = 1
  ValidateShape = true
  _ProfileBasedVersion = 1
  _Version = 0
FEATURE [Sketcher::SketchObject] Sketch039
  ArcFitTolerance = 0
  AttachmentSupport = -> [Pocket013]
  ExternalBSplineMaxDegree = 0
  ExternalBSplineTolerance = 0
  ExternalGeometry = -> [Pocket013]
  FullyConstrained = true
  InternalTolerance = 1e-06
  InvalidShape = false
  MakeInternals = false
  MapMode = 5
  Placement = pos=(0,-5,-1.1e-15) rot=(1,0,0;1.5708rad)
  Support = -> [Pocket013]
  TreeRank = 0
  ValidateShape = true
  sketch-geometry (3):
    g0: LineSegment StartX=15 StartY=-7 StartZ=0 EndX=5 EndY=-19.5 EndZ=0
    g1: LineSegment StartX=5 StartY=-7 StartZ=0 EndX=5 EndY=-19.5 EndZ=0
    g2: LineSegment StartX=5 StartY=-7 StartZ=0 EndX=15 EndY=-7 EndZ=0
  constraints (6):
    c: Coincident(g0,g-3)
    c: Coincident(g1,g-4)
    c: Coincident(g1,g0)
    c: Coincident(g2,g1)
    c: Coincident(g2,g0)
    c: Symmetric(g1,g-4,g0)
FEATURE [PartDesign::Pad] Pad026
  AddSubType = 0
  AutoTaperInnerAngle = false
  BaseFeature = -> Pocket013
  CheckUpToFaceLimits = true
  ClaimChildren = false
  Direction = (1,1,1)
  Fit = 0
  FitJoin = 0
  InnerFit = 0
  InnerFitJoin = 0
  InvalidShape = false
  Length = 2
  Length2 = 100
  Linearize = true
  NewSolid = false
  Placement = pos=(0,0,0) rot=(1,0,0;1.5708rad)
  Profile = -> Sketch039
  Refine = true
  Reversed = true
  Suppress = false
  TaperInnerAngle = 0
  TaperInnerAngleRev = 0
  TreeRank = 0
  Type = 0
  ValidateShape = true
  _ProfileBasedVersion = 1
FEATURE [Sketcher::SketchObject] Sketch040
  ArcFitTolerance = 0
  AttachmentSupport = -> [XY_Plane030]
  ExternalBSplineMaxDegree = 0
  ExternalBSplineTolerance = 0
  ExternalGeometry = -> [Pad026]
  FullyConstrained = true
  InternalTolerance = 1e-06
  InvalidShape = false
  MakeInternals = false
  MapMode = 5
  Support = -> [XY_Plane030]
  TreeRank = 0
  ValidateShape = true
  sketch-geometry (1):
    g0: Circle CenterX=10 CenterY=5 CenterZ=0 NormalX=0 NormalY=0 NormalZ=1 AngleXU=0 Radius=2.05
  constraints (3):
    c: DistanceX(g0,g-3) = 5
    c: DistanceY(g0,g-3) = 5
    c: Diameter(g0) = 4.1
FEATURE [PartDesign::Pocket] Pocket014
  AddSubType = 1
  AutoTaperInnerAngle = false
  BaseFeature = -> Pad026
  CheckUpToFaceLimits = true
  ClaimChildren = false
  Direction = (1,1,1)
  Fit = 0
  FitJoin = 0
  InnerFit = 0
  InnerFitJoin = 0
  InvalidShape = false
  Length = 5
  Length2 = 100
  Linearize = true
  NewSolid = false
  Placement = pos=(0,0,0) rot=(1,0,0;1.5708rad)
  Profile = -> Sketch040
  Refine = true
  Suppress = false
  TaperInnerAngle = 0
  TaperInnerAngleRev = 0
  TreeRank = 0
  Type = 1
  ValidateShape = true
  _ProfileBasedVersion = 1
  _Version = 0
FEATURE [Sketcher::SketchObject] Sketch041
  ArcFitTolerance = 0
  AttachmentSupport = -> [Pocket014]
  ExternalBSplineMaxDegree = 0
  ExternalBSplineTolerance = 0
  ExternalGeometry = -> [Pocket014]
  FullyConstrained = true
  InternalTolerance = 1e-06
  InvalidShape = false
  MakeInternals = false
  MapMode = 5
  Placement = pos=(5,0,0) rot=(0.707107,0,0.707107;3.14159rad)
  Support = -> [Pocket014]
  TreeRank = 0
  ValidateShape = true
  sketch-geometry (4):
    g0: Circle CenterX=-27 CenterY=-5 CenterZ=0 NormalX=0 NormalY=0 NormalZ=1 AngleXU=0 Radius=1.6
    g1: Circle CenterX=-12 CenterY=-5 CenterZ=0 NormalX=0 NormalY=0 NormalZ=1 AngleXU=0 Radius=1.6
    g2: LineSegment [constr] StartX=-32 StartY=-5 StartZ=0 EndX=-7 EndY=-5 EndZ=0
    g3: GeomPoint [constr] X=-19.5 Y=-5 Z=0
  constraints (10):
    c: Diameter(g0) = 3.2
    c: Equal(g0,g1)
    c: Horizontal(g1,g0)
    c: PointOnObject(g2,g-4)
    c: PointOnObject(g2,g-3)
    c: Horizontal(g2)
    c: DistanceY(g-5,g2) = 5
    c: Symmetric(g2,g2,g3)
    c: Symmetric(g0,g1,g3)
    c: DistanceX(g2,g0) = 5
FEATURE [PartDesign::Pocket] Pocket015
  AddSubType = 1
  AutoTaperInnerAngle = false
  BaseFeature = -> Pocket014
  CheckUpToFaceLimits = true
  ClaimChildren = false
  Direction = (1,1,1)
  Fit = 0
  FitJoin = 0
  InnerFit = 0
  InnerFitJoin = 0
  InvalidShape = false
  Length = 5
  Length2 = 100
  Linearize = true
  NewSolid = false
  Placement = pos=(0,0,0) rot=(1,0,0;1.5708rad)
  Profile = -> Sketch041
  Refine = true
  Suppress = false
  TaperInnerAngle = 0
  TaperInnerAngleRev = 0
  TreeRank = 0
  Type = 1
  ValidateShape = true
  _ProfileBasedVersion = 1
  _Version = 0
FEATURE [Sketcher::SketchObject] Sketch042
  ArcFitTolerance = 0
  AttachmentSupport = -> [Pocket015]
  ExternalBSplineMaxDegree = 0
  ExternalBSplineTolerance = 0
  ExternalGeometry = -> [Pocket015]
  FullyConstrained = true
  InternalTolerance = 1e-06
  InvalidShape = false
  MakeInternals = false
  MapMode = 5
  Placement = pos=(5,0,0) rot=(0.707107,0,0.707107;3.14159rad)
  Support = -> [Pocket015]
  TreeRank = 0
  ValidateShape = true
  sketch-geometry (5):
    g0: LineSegment StartX=-32 StartY=-10 StartZ=0 EndX=-32 EndY=-0.75 EndZ=0
    g1: LineSegment StartX=-32 StartY=-10 StartZ=0 EndX=-7.75 EndY=-10 EndZ=0
    g2: LineSegment StartX=-7.75 StartY=-10 StartZ=0 EndX=-7.75 EndY=-5 EndZ=0
    g3: ArcOfCircle CenterX=-12 CenterY=-5 CenterZ=0 NormalX=0 NormalY=0 NormalZ=1 AngleXU=0 Radius=4.25 StartAngle=0 EndAngle=1.5708
    g4: LineSegment StartX=-32 StartY=-0.75 StartZ=0 EndX=-12 EndY=-0.75 EndZ=0
  constraints (12):
    c: Coincident(g0,g-4)
    c: PointOnObject(g0,g-3)
    c: Coincident(g1,g0)
    c: PointOnObject(g1,g-4)
    c: Coincident(g2,g1)
    c: Vertical(g2)
    c: Coincident(g4,g0)
    c: Horizontal(g4)
    c: Tangent(g4,g3) = 1.5708
    c: Tangent(g3,g2) = -1.5708
    c: Coincident(g3,g-5)
    c: Diameter(g3) = 8.5
FEATURE [PartDesign::Pocket] Pocket016
  AddSubType = 1
  AutoTaperInnerAngle = false
  BaseFeature = -> Pocket015
  CheckUpToFaceLimits = true
  ClaimChildren = false
  Direction = (1,1,1)
  Fit = 0
  FitJoin = 0
  InnerFit = 0
  InnerFitJoin = 0
  InvalidShape = false
  Length = 2.5
  Length2 = 100
  Linearize = true
  NewSolid = false
  Placement = pos=(0,0,0) rot=(1,0,0;1.5708rad)
  Profile = -> Sketch042
  Refine = true
  Suppress = false
  TaperInnerAngle = 0
  TaperInnerAngleRev = 0
  TreeRank = 0
  Type = 0
  ValidateShape = true
  _ProfileBasedVersion = 1
  _Version = 0
FEATURE [PartDesign::Chamfer] Chamfer006
  AddSubType = 0
  Angle = 45
  Base = -> Pocket016 [Edge46,Edge41,Edge42,Edge39,Edge40,Edge36]
  BaseFeature = -> Pocket016
  ChamferType = 0
  FlipDirection = false
  InvalidShape = false
  NewSolid = false
  Placement = pos=(0,0,0) rot=(1,0,0;1.5708rad)
  Refine = true
  Size = 0.2
  Size2 = 1
  SupportTransform = false
  Suppress = false
  TreeRank = 0
  UseAllEdges = false
  ValidateShape = true
FEATURE [PartDesign::Chamfer] Chamfer005
  AddSubType = 0
  Angle = 45
  Base = -> Chamfer006 [Edge9,Edge36,Edge45,Edge21,Edge13]
  BaseFeature = -> Chamfer006
  ChamferType = 0
  FlipDirection = false
  InvalidShape = false
  NewSolid = false
  Placement = pos=(0,0,0) rot=(1,0,0;1.5708rad)
  Refine = true
  Size = 1
  Size2 = 1
  SupportTransform = false
  Suppress = false
  TreeRank = 0
  UseAllEdges = false
  ValidateShape = true
FEATURE [PartDesign::Body] Body023  label="BodySupport3DInter"
  AutoGroupSolids = false
  ClaimAllChildren = false
  ExportMode = 0
  Group = -> [Sketch037,Pad024,Pad025,Sketch038,Pocket013,Sketch039,Pad026,Sketch040,Pocket014,Sketch041,Pocket015,Sketch042,Pocket016,Chamfer006,Chamfer005]
  InvalidShape = false
  Origin = -> Origin034
  SingleSolid = true
  Tip = -> Chamfer005
  TreeRank = 0
  ValidateShape = true
  _ExportChildren = -> [Pad024,Pad025,Pocket013,Pad026,Pocket014,Pocket015,Pocket016,Chamfer006,Chamfer005]
  _GroupVersion = 1
FEATURE [Part::Mirroring] Part__Mirroring  label="BodySupport3DInter (Mirror #1)"
  Base = (0,0,0)
  InvalidShape = false
  Normal = (1,0,0)
  Source = -> Body023
  TreeRank = 0
  ValidateShape = true
FEATURE [App::Part] Part004  label="SupportGauche3D"
  ClaimAllChildren = false
  ExportMode = 1
  Group = -> [Body023,Part__Mirroring]
  Origin = -> Origin033
  TreeRank = 0
  _ExportChildren = -> [Part__Mirroring]
  _GroupVersion = 1
FEATURE [App::Link] Link054  label="Link054(BodySupport3DInter)"
  AutoLinkLabel = true
  AutoPlacement = true
  LinkedObject = -> Body023
  SyncGroupVisibility = false
  TreeRank = 0
  _LinkVersion = 1
FEATURE [App::Part] Part005  label="SupportDroit3D"
  ClaimAllChildren = false
  ExportMode = 1
  Group = -> [Link054]
  Origin = -> Origin035
  TreeRank = 0
  _ExportChildren = -> [Link054]
  _GroupVersion = 1
FEATURE [Sketcher::SketchObject] Sketch049
  ArcFitTolerance = 0
  AttachmentSupport = -> [XY_Plane033]
  ExternalBSplineMaxDegree = 0
  ExternalBSplineTolerance = 0
  FullyConstrained = true
  InternalTolerance = 1e-06
  InvalidShape = false
  MakeInternals = false
  MapMode = 5
  Support = -> [XY_Plane033]
  TreeRank = 0
  ValidateShape = true
  sketch-geometry (13):
    g0: LineSegment [constr] StartX=0 StartY=0 StartZ=0 EndX=0 EndY=12.5 EndZ=0
    g1: LineSegment StartX=0 StartY=12.5 StartZ=0 EndX=5 EndY=21.1603 EndZ=0
    g2: LineSegment StartX=5 StartY=21.1603 StartZ=0 EndX=13.6603 EndY=16.1603 EndZ=0
    g3: LineSegment StartX=13.6603 StartY=16.1603 StartZ=0 EndX=4.33013 EndY=0 EndZ=0
    g4: LineSegment StartX=4.33013 StartY=0 StartZ=0 EndX=0 EndY=0 EndZ=0
    g5: LineSegment StartX=0 StartY=12.5 StartZ=0 EndX=-2 EndY=12.5 EndZ=0
    g6: LineSegment StartX=-2 StartY=12.5 StartZ=0 EndX=-2 EndY=10 EndZ=0
    g7: LineSegment StartX=-2 StartY=10 StartZ=0 EndX=0 EndY=10 EndZ=0
    g8: LineSegment StartX=0 StartY=10 StartZ=0 EndX=0 EndY=6.25 EndZ=0
    g9: LineSegment StartX=0 StartY=6.25 StartZ=0 EndX=-2 EndY=6.25 EndZ=0
    g10: LineSegment StartX=-2 StartY=6.25 StartZ=0 EndX=-2 EndY=3.75 EndZ=0
    g11: LineSegment StartX=-2 StartY=3.75 StartZ=0 EndX=0 EndY=3.75 EndZ=0
    g12: LineSegment StartX=0 StartY=3.75 StartZ=0 EndX=0 EndY=0 EndZ=0
  constraints (37):
    c: Coincident(g-1,g0)
    c: PointOnObject(g0,g-2)
    c: Coincident(g1,g2)
    c: Coincident(g2,g3)
    c: PointOnObject(g3,g-1)
    c: Coincident(g3,g4)
    c: Coincident(g4,g0)
    c: Perpendicular(g2,g1)
    c: Perpendicular(g2,g3)
    c: DistanceY(g0,g0) = 12.5
    c: Distance(g2) = 10
    c: Distance(g1) = 10
    c: Horizontal(g5)
    c: Coincident(g6,g5)
    c: Vertical(g6)
    c: Coincident(g7,g6)
    c: PointOnObject(g7,g0)
    c: Horizontal(g7)
    c: Coincident(g8,g7)
    c: PointOnObject(g8,g0)
    c: Coincident(g9,g8)
    c: Coincident(g10,g9)
    c: Coincident(g11,g10)
    c: PointOnObject(g11,g0)
    c: Coincident(g12,g11)
    c: Coincident(g12,g4)
    c: Perpendicular(g10,g9)
    c: Perpendicular(g10,g11)
    c: Parallel(g10,g8)
    c: Equal(g8,g12)
    c: DistanceY(g4,g7) = 10
    c: DistanceY(g10,g10) = 2.5
    c: DistanceX(g9,g9) = 2
    c: DistanceX(g5,g5) = 2
    c: Coincident(g1,g5)
    c: Coincident(g1,g0)
    c: Angle(g1,g5) = 2.0944
FEATURE [PartDesign::Pad] Pad029
  AddSubType = 0
  AutoTaperInnerAngle = false
  CheckUpToFaceLimits = true
  ClaimChildren = false
  Direction = (1,1,1)
  Fit = 0
  FitJoin = 0
  InnerFit = 0
  InnerFitJoin = 0
  InvalidShape = false
  Length = 7
  Length2 = 100
  Linearize = true
  NewSolid = false
  Profile = -> Sketch049
  Refine = true
  Suppress = false
  TaperInnerAngle = 0
  TaperInnerAngleRev = 0
  TreeRank = 0
  Type = 0
  ValidateShape = true
  _ProfileBasedVersion = 1
FEATURE [Sketcher::SketchObject] Sketch051
  ArcFitTolerance = 0
  AttachmentSupport = -> [XY_Plane033]
  ExternalBSplineMaxDegree = 0
  ExternalBSplineTolerance = 0
  ExternalGeometry = -> [Pad029]
  FullyConstrained = true
  InternalTolerance = 1e-06
  InvalidShape = false
  MakeInternals = false
  MapMode = 5
  Support = -> [XY_Plane033]
  TreeRank = 0
  ValidateShape = true
  sketch-geometry (4):
    g0: LineSegment StartX=4.33013 StartY=10 StartZ=0 EndX=4.33013 EndY=0 EndZ=0
    g1: LineSegment StartX=0 StartY=6.25 StartZ=0 EndX=0 EndY=3.75 EndZ=0
    g2: LineSegment StartX=4.33013 StartY=10 StartZ=0 EndX=0 EndY=12.5 EndZ=0
    g3: LineSegment StartX=0 StartY=12.5 StartZ=0 EndX=-2 EndY=12.5 EndZ=0
  constraints (10):
    c: Vertical(g0)
    c: Coincident(g1,g-8)
    c: Coincident(g1,g-5)
    c: Coincident(g0,g-11)
    c: Coincident(g2,g0)
    c: PointOnObject(g2,g-12)
    c: Coincident(g3,g-10)
    c: Coincident(g2,g3)
    c: Horizontal(g3)
    c: Perpendicular(g-12,g2)
FEATURE [PartDesign::Pad] Pad030
  AddSubType = 0
  AutoTaperInnerAngle = false
  BaseFeature = -> Pad029
  CheckUpToFaceLimits = true
  ClaimChildren = false
  Direction = (1,1,1)
  Fit = 0
  FitJoin = 0
  InnerFit = 0
  InnerFitJoin = 0
  InvalidShape = false
  Length = 15
  Length2 = 100
  Linearize = true
  NewSolid = false
  Profile = -> Sketch051
  Refine = true
  Reversed = true
  Suppress = false
  TaperInnerAngle = 0
  TaperInnerAngleRev = 0
  TreeRank = 0
  Type = 0
  ValidateShape = true
  _ProfileBasedVersion = 1
FEATURE [Sketcher::SketchObject] Sketch052
  ArcFitTolerance = 0
  AttachmentSupport = -> [YZ_Plane033]
  ExternalBSplineMaxDegree = 0
  ExternalBSplineTolerance = 0
  ExternalGeometry = -> [Pad030]
  FullyConstrained = true
  InternalTolerance = 1e-06
  InvalidShape = false
  MakeInternals = false
  MapMode = 5
  Placement = pos=(0,0,0) rot=(0.57735,0.57735,0.57735;2.0944rad)
  Support = -> [YZ_Plane033]
  TreeRank = 0
  ValidateShape = true
  sketch-geometry (1):
    g0: Circle CenterX=5 CenterY=-10 CenterZ=0 NormalX=0 NormalY=0 NormalZ=1 AngleXU=0 Radius=1.6
  constraints (3):
    c: DistanceX(g0) = 5
    c: Diameter(g0) = 3.2
    c: DistanceY(g-3,g0) = 5
FEATURE [PartDesign::Pocket] Pocket020
  AddSubType = 1
  AutoTaperInnerAngle = false
  BaseFeature = -> Pad030
  CheckUpToFaceLimits = true
  ClaimChildren = false
  Direction = (1,1,1)
  Fit = 0
  FitJoin = 0
  InnerFit = 0
  InnerFitJoin = 0
  InvalidShape = false
  Length = 5
  Length2 = 100
  Linearize = true
  NewSolid = false
  Profile = -> Sketch052
  Refine = true
  Reversed = true
  Suppress = false
  TaperInnerAngle = 0
  TaperInnerAngleRev = 0
  TreeRank = 0
  Type = 1
  ValidateShape = true
  _ProfileBasedVersion = 1
  _Version = 0
FEATURE [Sketcher::SketchObject] Sketch054
  ArcFitTolerance = 0
  AttachmentSupport = -> [XY_Plane033]
  ExternalBSplineMaxDegree = 0
  ExternalBSplineTolerance = 0
  ExternalGeometry = -> [Pocket020]
  FullyConstrained = true
  InternalTolerance = 1e-06
  InvalidShape = false
  MakeInternals = false
  MapMode = 5
  Support = -> [XY_Plane033]
  TreeRank = 0
  ValidateShape = true
  sketch-geometry (3):
    g0: Circle CenterX=6.83013 CenterY=14.3301 CenterZ=0 NormalX=0 NormalY=0 NormalZ=1 AngleXU=0 Radius=2.1
    g1: LineSegment [constr] StartX=9.33013 StartY=18.6603 StartZ=0 EndX=6.83013 EndY=14.3301 EndZ=0
    g2: LineSegment [constr] StartX=6.83013 StartY=14.3301 StartZ=0 EndX=11.1603 EndY=11.8301 EndZ=0
  constraints (11):
    c: Diameter(g0) = 4.2
    c: Coincident(g1,g0)
    c: Coincident(g1,g2)
    c: Perpendicular(g1,g2)
    c: Distance(g1) = 5
    c: Distance(g2) = 5
    c: PointOnObject(g2,g-4)
    c: PointOnObject(g1,g-3)
    c: Perpendicular(g-3,g1)
    c: DistanceX(g-1,g0) = 6.83013
    c: DistanceY(g-1,g0) = 14.3301
FEATURE [PartDesign::Pocket] Pocket022
  AddSubType = 1
  AutoTaperInnerAngle = false
  BaseFeature = -> Pocket020
  CheckUpToFaceLimits = true
  ClaimChildren = false
  Direction = (1,1,1)
  Fit = 0
  FitJoin = 0
  InnerFit = 0
  InnerFitJoin = 0
  InvalidShape = false
  Length = 5
  Length2 = 100
  Linearize = true
  NewSolid = false
  Profile = -> Sketch054
  Refine = true
  Reversed = true
  Suppress = false
  TaperInnerAngle = 0
  TaperInnerAngleRev = 0
  TreeRank = 0
  Type = 1
  ValidateShape = true
  _ProfileBasedVersion = 1
  _Version = 0
FEATURE [Sketcher::SketchObject] Sketch055
  ArcFitTolerance = 0
  AttachmentSupport = -> [Pocket022]
  ExternalBSplineMaxDegree = 0
  ExternalBSplineTolerance = 0
  ExternalGeometry = -> [Pocket022]
  FullyConstrained = true
  InternalTolerance = 1e-06
  InvalidShape = false
  MakeInternals = false
  MapMode = 5
  Placement = pos=(4.33013,0,0) rot=(0.57735,0.57735,0.57735;2.0944rad)
  Support = -> [Pocket022]
  TreeRank = 0
  ValidateShape = true
  sketch-geometry (4):
    g0: LineSegment StartX=0 StartY=-15 StartZ=0 EndX=12.5 EndY=-15 EndZ=0
    g1: LineSegment StartX=12.5 StartY=-15 StartZ=0 EndX=12.5 EndY=-5 EndZ=0
    g2: LineSegment StartX=12.5 StartY=-5 StartZ=0 EndX=0 EndY=-5 EndZ=0
    g3: LineSegment StartX=0 StartY=-5 StartZ=0 EndX=0 EndY=-15 EndZ=0
  constraints (11):
    c: Coincident(g0,g1)
    c: Coincident(g1,g2)
    c: Coincident(g2,g3)
    c: Coincident(g3,g0)
    c: Horizontal(g0)
    c: Horizontal(g2)
    c: Vertical(g1)
    c: Vertical(g3)
    c: PointOnObject(g1,g-4)
    c: Coincident(g0,g-3)
    c: DistanceY(g3,g3) = 10
FEATURE [PartDesign::Pocket] Pocket023
  AddSubType = 1
  AutoTaperInnerAngle = false
  BaseFeature = -> Pocket022
  CheckUpToFaceLimits = true
  ClaimChildren = false
  Direction = (1,1,1)
  Fit = 0
  FitJoin = 0
  InnerFit = 0
  InnerFitJoin = 0
  InvalidShape = false
  Length = 1.9
  Length2 = 100
  Linearize = true
  NewSolid = false
  Profile = -> Sketch055
  Refine = true
  Suppress = false
  TaperInnerAngle = 0
  TaperInnerAngleRev = 0
  TreeRank = 0
  Type = 0
  ValidateShape = true
  _ProfileBasedVersion = 1
  _Version = 0
FEATURE [Sketcher::SketchObject] Sketch056
  ArcFitTolerance = 0
  AttachmentSupport = -> [XY_Plane033]
  ExternalBSplineMaxDegree = 0
  ExternalBSplineTolerance = 0
  ExternalGeometry = -> [Pocket023]
  FullyConstrained = true
  InternalTolerance = 1e-06
  InvalidShape = false
  MakeInternals = false
  MapMode = 5
  Support = -> [XY_Plane033]
  TreeRank = 0
  ValidateShape = true
  sketch-geometry (3):
    g0: LineSegment StartX=4.33013 StartY=10 StartZ=0 EndX=4.33013 EndY=0 EndZ=0
    g1: LineSegment StartX=4.33013 StartY=0 StartZ=0 EndX=8.66025 EndY=7.5 EndZ=0
    g2: LineSegment StartX=8.66025 StartY=7.5 StartZ=0 EndX=4.33013 EndY=10 EndZ=0
  constraints (7):
    c: Coincident(g-5,g0)
    c: Coincident(g0,g-4)
    c: Coincident(g0,g1)
    c: PointOnObject(g1,g-4)
    c: Coincident(g1,g2)
    c: Coincident(g2,g0)
    c: Parallel(g2,g-5)
FEATURE [PartDesign::Pad] Pad031
  AddSubType = 0
  AutoTaperInnerAngle = false
  BaseFeature = -> Pocket023
  CheckUpToFaceLimits = true
  ClaimChildren = false
  Direction = (1,1,1)
  Fit = 0
  FitJoin = 0
  InnerFit = 0
  InnerFitJoin = 0
  InvalidShape = false
  Length = 10
  Length2 = 100
  Linearize = true
  NewSolid = false
  Profile = -> Sketch056
  Refine = true
  Reversed = true
  Suppress = false
  TaperInnerAngle = 0
  TaperInnerAngleRev = 0
  TreeRank = 0
  Type = 3
  UpToFace = -> Pocket023 [Face19]
  ValidateShape = true
  _ProfileBasedVersion = 1
FEATURE [PartDesign::Draft] Draft
  AddSubType = 0
  Angle = 38.5
  Base = -> Pad031 [Face20]
  BaseFeature = -> Pad031
  InvalidShape = false
  NeutralPlane = -> Pad031 [Face15]
  NewSolid = false
  Refine = true
  SupportTransform = false
  Suppress = false
  TreeRank = 0
  ValidateShape = true
FEATURE [PartDesign::Chamfer] Chamfer009
  AddSubType = 0
  Angle = 45
  Base = -> Draft [Edge26]
  BaseFeature = -> Draft
  ChamferType = 0
  FlipDirection = false
  InvalidShape = false
  NewSolid = false
  Refine = true
  Size = 2
  Size2 = 1
  SupportTransform = false
  Suppress = false
  TreeRank = 0
  UseAllEdges = false
  ValidateShape = true
FEATURE [PartDesign::Draft] Draft001
  AddSubType = 0
  Angle = 66.5
  Base = -> Chamfer009 [Face16]
  BaseFeature = -> Chamfer009
  InvalidShape = false
  NeutralPlane = -> Chamfer009 [Face21]
  NewSolid = false
  Refine = true
  Reversed = true
  SupportTransform = false
  Suppress = false
  TreeRank = 0
  ValidateShape = true
FEATURE [PartDesign::Chamfer] Chamfer010
  AddSubType = 0
  Angle = 45
  Base = -> Draft001 [Edge51,Edge50,Edge54,Edge53]
  BaseFeature = -> Draft001
  ChamferType = 0
  FlipDirection = false
  InvalidShape = false
  NewSolid = false
  Refine = true
  Size = 0.4
  Size2 = 1
  SupportTransform = false
  Suppress = false
  TreeRank = 0
  UseAllEdges = false
  ValidateShape = true
FEATURE [PartDesign::Chamfer] Chamfer011
  AddSubType = 0
  Angle = 45
  Base = -> Chamfer010 [Edge45]
  BaseFeature = -> Chamfer010
  ChamferType = 0
  FlipDirection = false
  InvalidShape = false
  NewSolid = false
  Refine = true
  Size = 1
  Size2 = 1
  SupportTransform = false
  Suppress = false
  TreeRank = 0
  UseAllEdges = false
  ValidateShape = true
FEATURE [PartDesign::Chamfer] Chamfer012
  AddSubType = 0
  Angle = 45
  Base = -> Chamfer011 [Edge10,Edge19]
  BaseFeature = -> Chamfer011
  ChamferType = 0
  FlipDirection = false
  InvalidShape = false
  NewSolid = false
  Refine = true
  Size = 0.2
  Size2 = 1
  SupportTransform = false
  Suppress = false
  TreeRank = 0
  UseAllEdges = false
  ValidateShape = true
FEATURE [PartDesign::Chamfer] Chamfer013
  AddSubType = 0
  Angle = 45
  Base = -> Chamfer012 [Edge64,Edge38]
  BaseFeature = -> Chamfer012
  ChamferType = 0
  FlipDirection = false
  InvalidShape = false
  NewSolid = false
  Refine = true
  Size = 1
  Size2 = 1
  SupportTransform = false
  Suppress = false
  TreeRank = 0
  UseAllEdges = false
  ValidateShape = true
FEATURE [PartDesign::Fillet] Fillet016
  AddSubType = 0
  Base = -> Chamfer013 [Edge37]
  BaseFeature = -> Chamfer013
  InvalidShape = false
  NewSolid = false
  Radius = 2
  Refine = true
  SupportTransform = false
  Suppress = false
  TreeRank = 0
  UseAllEdges = false
  ValidateShape = true
FEATURE [PartDesign::Chamfer] Chamfer014
  AddSubType = 0
  Angle = 45
  Base = -> Fillet016 [Edge20,Edge70,Edge79,Edge44]
  BaseFeature = -> Fillet016
  ChamferType = 0
  FlipDirection = false
  InvalidShape = false
  NewSolid = false
  Refine = true
  Size = 0.2
  Size2 = 1
  SupportTransform = false
  Suppress = false
  TreeRank = 0
  UseAllEdges = false
  ValidateShape = true
FEATURE [Sketcher::SketchObject] Sketch057
  ArcFitTolerance = 0
  AttachmentSupport = -> [XY_Plane033]
  ExternalBSplineMaxDegree = 0
  ExternalBSplineTolerance = 0
  FullyConstrained = false
  InternalTolerance = 1e-06
  InvalidShape = false
  MakeInternals = false
  MapMode = 5
  Support = -> [XY_Plane033]
  TreeRank = 0
  ValidateShape = true
  sketch-geometry (4):
    g0: LineSegment StartX=0 StartY=15.6465 StartZ=0 EndX=-3.55109 EndY=15.6465 EndZ=0
    g1: LineSegment StartX=-3.55109 StartY=15.6465 StartZ=0 EndX=-3.55109 EndY=7.42705 EndZ=0
    g2: LineSegment StartX=-3.55109 StartY=7.42705 StartZ=0 EndX=0 EndY=7.42705 EndZ=0
    g3: LineSegment StartX=0 StartY=7.42705 StartZ=0 EndX=0 EndY=15.6465 EndZ=0
  constraints (9):
    c: Coincident(g0,g1)
    c: Coincident(g1,g2)
    c: Coincident(g2,g3)
    c: Coincident(g3,g0)
    c: Horizontal(g0)
    c: Horizontal(g2)
    c: Vertical(g1)
    c: Vertical(g3)
    c: PointOnObject(g0,g-2)
FEATURE [PartDesign::Pocket] Pocket024
  AddSubType = 1
  AutoTaperInnerAngle = false
  BaseFeature = -> Chamfer014
  CheckUpToFaceLimits = true
  ClaimChildren = false
  Direction = (1,1,1)
  Fit = 0
  FitJoin = 0
  InnerFit = 0
  InnerFitJoin = 0
  InvalidShape = false
  Length = 39
  Length2 = 100
  Linearize = true
  Midplane = true
  NewSolid = false
  Profile = -> Sketch057
  Refine = true
  Suppress = false
  TaperInnerAngle = 0
  TaperInnerAngleRev = 0
  TreeRank = 0
  Type = 1
  ValidateShape = true
  _ProfileBasedVersion = 1
  _Version = 0
FEATURE [PartDesign::Chamfer] Chamfer015
  AddSubType = 0
  Angle = 45
  Base = -> Pocket024 [Edge69,Edge58,Edge54]
  BaseFeature = -> Pocket024
  ChamferType = 0
  FlipDirection = false
  InvalidShape = false
  NewSolid = false
  Refine = true
  Size = 0.5
  Size2 = 1
  SupportTransform = false
  Suppress = false
  TreeRank = 0
  UseAllEdges = false
  ValidateShape = true
FEATURE [PartDesign::Body] Body026
  AutoGroupSolids = false
  ClaimAllChildren = false
  ExportMode = 0
  Group = -> [Sketch049,Sketch051,Sketch052,Sketch054,Pad029,Pad030,Pocket020,Pocket022,Sketch055,Pocket023,Sketch056,Pad031,Draft,Chamfer009,Draft001,Chamfer010,Chamfer011,Chamfer012,Chamfer013,Fillet016,Chamfer014,Sketch057,Pocket024,Chamfer015]
  InvalidShape = false
  Origin = -> Origin041
  SingleSolid = true
  Tip = -> Chamfer015
  TreeRank = 0
  ValidateShape = true
  _ExportChildren = -> [Pad029,Pad030,Pocket020,Pocket022,Pocket023,Pad031,Draft,Chamfer009,Draft001,Chamfer010,Chamfer011,Chamfer012,Chamfer013,Fillet016,Chamfer014,Pocket024,Chamfer015]
  _GroupVersion = 1
FEATURE [Part::Mirroring] Part__Mirroring001  label="Body026 (Mirror #2)"
  Base = (0,0,0)
  InvalidShape = false
  Normal = (1,0,0)
  Source = -> Body026
  TreeRank = 0
  ValidateShape = true
FEATURE [App::Part] Part008  label="SupportGauche120d"
  ClaimAllChildren = false
  ExportMode = 1
  Group = -> [Body026,Part__Mirroring001]
  Origin = -> Origin040
  TreeRank = 0
  _ExportChildren = -> [Part__Mirroring001]
  _GroupVersion = 1
FEATURE [App::Link] Link063  label="Link063(Body026)"
  AutoLinkLabel = true
  AutoPlacement = true
  LinkedObject = -> Body026
  SyncGroupVisibility = false
  TreeRank = 0
  _LinkVersion = 1
FEATURE [App::Part] Part009  label="SupportDroite120d"
  ClaimAllChildren = false
  ExportMode = 1
  Group = -> [Link063]
  Origin = -> Origin042
  TreeRank = 0
  _ExportChildren = -> [Link063]
  _GroupVersion = 1
FEATURE [Sketcher::SketchObject] Sketch045
  ArcFitTolerance = 0
  AttachmentSupport = -> [XY_Plane032]
  ExternalBSplineMaxDegree = 0
  ExternalBSplineTolerance = 0
  FullyConstrained = true
  InternalTolerance = 1e-06
  InvalidShape = false
  MakeInternals = false
  MapMode = 5
  Support = -> [XY_Plane032]
  TreeRank = 0
  ValidateShape = true
  sketch-geometry (6):
    g0: LineSegment StartX=40 StartY=50 StartZ=0 EndX=40 EndY=40 EndZ=0
    g1: LineSegment StartX=40 StartY=40 StartZ=0 EndX=47.3205 EndY=27.3205 EndZ=0
    g2: LineSegment [constr] StartX=0 StartY=0 StartZ=0 EndX=54.6506 EndY=31.5526 EndZ=0
    g3: LineSegment StartX=40 StartY=50 StartZ=0 EndX=44 EndY=50 EndZ=0
    g4: LineSegment StartX=44 StartY=50 StartZ=0 EndX=54.6506 EndY=31.5526 EndZ=0
    g5: LineSegment StartX=54.6506 StartY=31.5526 StartZ=0 EndX=47.3205 EndY=27.3205 EndZ=0
  constraints (17):
    c: Vertical(g0)
    c: Coincident(g1,g0)
    c: Coincident(g2,g-1)
    c: Angle(g2,g-2) = 1.0472
    c: PointOnObject(g1,g2)
    c: Coincident(g0,g3)
    c: Horizontal(g3)
    c: Coincident(g3,g4)
    c: Coincident(g4,g5)
    c: Coincident(g5,g1)
    c: Parallel(g1,g4)
    c: DistanceX(g2,g0) = 40
    c: DistanceY(g0,g0) = 10
    c: DistanceY(g0) = 40
    c: Perpendicular(g5,g1)
    c: DistanceX(g3,g3) = 4
    c: Coincident(g2,g4)
FEATURE [PartDesign::Plane] DatumPlane004
  AttachmentOffset = pos=(0,0,0) rot=(0,-1,0;1.0472rad)
  AttachmentSupport = -> [YZ_Plane032]
  InvalidShape = false
  Length = 81.5526
  MapMode = 5
  MinimumLength = 10
  MinimumWidth = 10
  Placement = pos=(0,0,0) rot=(0.935113,0.250563,0.250563;1.63783rad)
  ResizeMode = 0
  Support = -> [YZ_Plane032]
  TreeRank = 0
  ValidateShape = true
  Width = 30
FEATURE [PartDesign::Pad] Pad028
  AddSubType = 0
  AutoTaperInnerAngle = false
  CheckUpToFaceLimits = true
  ClaimChildren = false
  Direction = (1,1,1)
  Fit = 0
  FitJoin = 0
  InnerFit = 0
  InnerFitJoin = 0
  InvalidShape = false
  Length = 30
  Length2 = 100
  Linearize = true
  Midplane = true
  NewSolid = false
  Profile = -> Sketch045
  Refine = true
  Suppress = false
  TaperInnerAngle = 0
  TaperInnerAngleRev = 0
  TreeRank = 0
  Type = 0
  ValidateShape = true
  _ProfileBasedVersion = 1
FEATURE [PartDesign::Mirrored] Mirrored
  AddSubType = 0
  BaseFeature = -> Pad028
  CopyShape = false
  InvalidShape = false
  MirrorPlane = -> DatumPlane004
  NewSolid = false
  OriginalSubs = -> [Pad028]
  Originals = -> [Pad028]
  ParallelTransform = true
  Refine = true
  SubTransform = true
  Suppress = false
  TreeRank = 0
  ValidateShape = true
  _Version = 2
FEATURE [Sketcher::SketchObject] Sketch046
  ArcFitTolerance = 0
  AttachmentOffset = pos=(0,0,-10) rot=(0,0,1;0rad)
  AttachmentSupport = -> [Mirrored]
  ExternalBSplineMaxDegree = 0
  ExternalBSplineTolerance = 0
  ExternalGeometry = -> [Mirrored]
  FullyConstrained = true
  InternalTolerance = 1e-06
  InvalidShape = false
  MakeInternals = false
  MapMode = 5
  Placement = pos=(50,0,0) rot=(0.57735,-0.57735,-0.57735;2.0944rad)
  Support = -> [Mirrored]
  TreeRank = 0
  ValidateShape = true
  sketch-geometry (2):
    g0: Circle CenterX=-45 CenterY=10 CenterZ=0 NormalX=0 NormalY=0 NormalZ=1 AngleXU=0 Radius=1.5
    g1: LineSegment [constr] StartX=-45 StartY=15 StartZ=0 EndX=-45 EndY=-15 EndZ=0
  constraints (6):
    c: Diameter(g0) = 3
    c: DistanceY(g0) = 10
    c: PointOnObject(g1,g-4)
    c: Vertical(g1)
    c: Symmetric(g-3,g-3,g1)
    c: PointOnObject(g0,g1)
FEATURE [PartDesign::Hole] Hole
  AddSubType = 1
  BaseFeature = -> Mirrored
  ClaimChildren = false
  CustomThreadClearance = 0
  Depth = 25
  DepthType = 0
  Diameter = 3.2
  DrillForDepth = false
  DrillPoint = 1
  DrillPointAngle = 118
  Fit = 0
  FitJoin = 0
  HoleCutCountersinkAngle = 90
  HoleCutCustomValues = false
  HoleCutDepth = 7.5
  HoleCutDiameter = 8.5
  HoleCutType = 1
  InnerFit = 0
  InnerFitJoin = 0
  InvalidShape = false
  ModelThread = false
  NewSolid = false
  Profile = -> Sketch046
  Refine = true
  Reversed = true
  Suppress = false
  Tapered = false
  TaperedAngle = 90
  ThreadClass = 0
  ThreadDepth = 23.5
  ThreadDepthType = 0
  ThreadDirection = 0
  ThreadFit = 0
  ThreadSize = 0
  ThreadType = 0
  Threaded = false
  TreeRank = 0
  UseCustomThreadClearance = false
  ValidateShape = true
  _ProfileBasedVersion = 1
FEATURE [PartDesign::Mirrored] Mirrored001
  AddSubType = 0
  CopyShape = false
  InvalidShape = false
  MirrorPlane = -> XY_Plane032
  NewSolid = false
  ParallelTransform = true
  Refine = true
  SubTransform = true
  Suppress = false
  TreeRank = 0
  ValidateShape = true
  _Version = 2
FEATURE [PartDesign::Mirrored] Mirrored002
  AddSubType = 0
  CopyShape = false
  InvalidShape = false
  MirrorPlane = -> DatumPlane004
  NewSolid = false
  ParallelTransform = true
  Refine = true
  SubTransform = true
  Suppress = false
  TreeRank = 0
  ValidateShape = true
  _Version = 2
FEATURE [PartDesign::MultiTransform] MultiTransform002
  AddSubType = 0
  BaseFeature = -> Hole
  CopyShape = false
  InvalidShape = false
  NewSolid = false
  OriginalSubs = -> [Hole]
  Originals = -> [Hole]
  ParallelTransform = true
  Refine = true
  SubTransform = true
  Suppress = false
  Transformations = -> [Mirrored001,Mirrored002]
  TreeRank = 0
  ValidateShape = true
  _Version = 2
FEATURE [Sketcher::SketchObject] Sketch047
  ArcFitTolerance = 0
  AttachmentSupport = -> [MultiTransform002]
  ExternalBSplineMaxDegree = 0
  ExternalBSplineTolerance = 0
  FullyConstrained = true
  InternalTolerance = 1e-06
  InvalidShape = false
  MakeInternals = false
  MapMode = 5
  Placement = pos=(54.6506,31.5526,-6.3e-15) rot=(0.377964,0.654654,0.654654;2.41886rad)
  Support = -> [MultiTransform002]
  TreeRank = 0
  ValidateShape = true
  sketch-geometry (1):
    g0: Circle CenterX=7.5 CenterY=10 CenterZ=0 NormalX=0 NormalY=0 NormalZ=1 AngleXU=0 Radius=2.05
  constraints (3):
    c: Diameter(g0) = 4.1
    c: DistanceY(g-1,g0) = 10
    c: DistanceX(g-1,g0) = 7.5
FEATURE [PartDesign::Pocket] Pocket018
  AddSubType = 1
  AutoTaperInnerAngle = false
  BaseFeature = -> MultiTransform002
  CheckUpToFaceLimits = true
  ClaimChildren = false
  Direction = (1,1,1)
  Fit = 0
  FitJoin = 0
  InnerFit = 0
  InnerFitJoin = 0
  InvalidShape = false
  Length = 5
  Length2 = 100
  Linearize = true
  NewSolid = false
  Profile = -> Sketch047
  Refine = true
  Suppress = false
  TaperInnerAngle = 0
  TaperInnerAngleRev = 0
  TreeRank = 0
  Type = 1
  ValidateShape = true
  _ProfileBasedVersion = 1
  _Version = 0
FEATURE [PartDesign::Mirrored] Mirrored003
  AddSubType = 0
  CopyShape = false
  InvalidShape = false
  MirrorPlane = -> DatumPlane004
  NewSolid = false
  ParallelTransform = true
  Refine = true
  SubTransform = true
  Suppress = false
  TreeRank = 0
  ValidateShape = true
  _Version = 2
FEATURE [PartDesign::Mirrored] Mirrored004
  AddSubType = 0
  CopyShape = false
  InvalidShape = false
  MirrorPlane = -> XY_Plane032
  NewSolid = false
  ParallelTransform = true
  Refine = true
  SubTransform = true
  Suppress = false
  TreeRank = 0
  ValidateShape = true
  _Version = 2
FEATURE [PartDesign::MultiTransform] MultiTransform003
  AddSubType = 0
  BaseFeature = -> Pocket018
  CopyShape = false
  InvalidShape = false
  NewSolid = false
  OriginalSubs = -> [Pocket018]
  Originals = -> [Pocket018]
  ParallelTransform = true
  Refine = true
  SubTransform = true
  Suppress = false
  Transformations = -> [Mirrored003,Mirrored004]
  TreeRank = 0
  ValidateShape = true
  _Version = 2
FEATURE [PartDesign::Chamfer] Chamfer008
  AddSubType = 0
  Angle = 45
  Base = -> MultiTransform003 [Edge5,Edge6,Edge38,Edge37,Edge21,Edge19,Edge20,Edge22,Edge30,Edge29,Edge33,Edge34,Edge32,Edge28,Edge35,Edge31]
  BaseFeature = -> MultiTransform003
  ChamferType = 0
  FlipDirection = false
  InvalidShape = false
  NewSolid = false
  Refine = true
  Size = 0.2
  Size2 = 1
  SupportTransform = false
  Suppress = false
  TreeRank = 0
  UseAllEdges = false
  ValidateShape = true
FEATURE [Sketcher::SketchObject] Sketch048
  ArcFitTolerance = 0
  AttachmentSupport = -> [Chamfer008]
  ExternalBSplineMaxDegree = 0
  ExternalBSplineTolerance = 0
  FullyConstrained = true
  InternalTolerance = 1e-06
  InvalidShape = false
  MakeInternals = false
  MapMode = 5
  Placement = pos=(54.6506,31.5526,-6.3e-15) rot=(0.377964,0.654654,0.654654;2.41886rad)
  Support = -> [Chamfer008]
  TreeRank = 0
  ValidateShape = true
  sketch-geometry (16):
    g0: ArcOfCircle CenterX=-15 CenterY=0 CenterZ=0 NormalX=0 NormalY=0 NormalZ=1 AngleXU=0 Radius=1 StartAngle=1.5708 EndAngle=4.71239
    g1: ArcOfCircle CenterX=15 CenterY=0 CenterZ=0 NormalX=0 NormalY=0 NormalZ=1 AngleXU=0 Radius=1 StartAngle=4.71239 EndAngle=7.85398
    g2: LineSegment [constr] StartX=-15 StartY=-1 StartZ=0 EndX=15 EndY=-1 EndZ=0
    g3: LineSegment [constr] StartX=-15 StartY=1 StartZ=0 EndX=15 EndY=1 EndZ=0
    g4: ArcOfCircle CenterX=2.81924e-11 CenterY=-10 CenterZ=0 NormalX=0 NormalY=0 NormalZ=1 AngleXU=0 Radius=1 StartAngle=3.14159 EndAngle=6.28319
    g5: ArcOfCircle CenterX=-2.81924e-11 CenterY=10 CenterZ=0 NormalX=0 NormalY=0 NormalZ=1 AngleXU=0 Radius=1 StartAngle=0 EndAngle=3.14159
    g6: LineSegment [constr] StartX=1 StartY=-10 StartZ=0 EndX=1 EndY=10 EndZ=0
    g7: LineSegment [constr] StartX=-1 StartY=-10 StartZ=0 EndX=-1 EndY=10 EndZ=0
    g8: LineSegment StartX=-15 StartY=1 StartZ=0 EndX=-1 EndY=1 EndZ=0
    g9: LineSegment StartX=-1 StartY=1 StartZ=0 EndX=-1 EndY=10 EndZ=0
    g10: LineSegment StartX=1 StartY=10 StartZ=0 EndX=1 EndY=1 EndZ=0
    g11: LineSegment StartX=1 StartY=1 StartZ=0 EndX=15 EndY=1 EndZ=0
    g12: LineSegment StartX=-15 StartY=-1 StartZ=0 EndX=-1 EndY=-1 EndZ=0
    g13: LineSegment StartX=-1 StartY=-1 StartZ=0 EndX=-1 EndY=-10 EndZ=0
    g14: LineSegment StartX=1 StartY=-10 StartZ=0 EndX=1 EndY=-1 EndZ=0
    g15: LineSegment StartX=1 StartY=-1 StartZ=0 EndX=15 EndY=-1 EndZ=0
  constraints (36):
    c: Tangent(g0,g3) = 1.5708
    c: Tangent(g0,g2) = -1.5708
    c: Tangent(g2,g1) = -1.5708
    c: Tangent(g3,g1) = 1.5708
    c: Horizontal(g2)
    c: Equal(g0,g1)
    c: Tangent(g4,g7) = 1.5708
    c: Tangent(g4,g6) = -1.5708
    c: Tangent(g6,g5) = -1.5708
    c: Tangent(g7,g5) = 1.5708
    c: Vertical(g6)
    c: Equal(g4,g5)
    c: Equal(g5,g0)
    c: Symmetric(g0,g1,g-1)
    c: Symmetric(g4,g5,g-1)
    c: Diameter(g0) = 2
    c: DistanceX(g0,g1) = 30
    c: DistanceY(g4,g5) = 20
    c: Tangent(g0,g8) = 1.5708
    c: Coincident(g8,g9)
    c: Coincident(g9,g5)
    c: Vertical(g9)
    c: Tangent(g5,g10) = 1.5708
    c: Coincident(g11,g10)
    c: Coincident(g11,g1)
    c: Horizontal(g11)
    c: Coincident(g12,g0)
    c: PointOnObject(g12,g7)
    c: Horizontal(g12)
    c: Coincident(g13,g12)
    c: Coincident(g13,g4)
    c: Coincident(g14,g4)
    c: PointOnObject(g14,g2)
    c: Vertical(g14)
    c: Coincident(g15,g14)
    c: Coincident(g15,g1)
FEATURE [PartDesign::Pocket] Pocket019
  AddSubType = 1
  AutoTaperInnerAngle = false
  BaseFeature = -> Chamfer008
  CheckUpToFaceLimits = true
  ClaimChildren = false
  Direction = (1,1,1)
  Fit = 0
  FitJoin = 0
  InnerFit = 0
  InnerFitJoin = 0
  InvalidShape = false
  Length = 0.7
  Length2 = 100
  Linearize = true
  NewSolid = false
  Profile = -> Sketch048
  Refine = true
  Suppress = false
  TaperInnerAngle = 0
  TaperInnerAngleRev = 0
  TreeRank = 0
  Type = 0
  ValidateShape = true
  _ProfileBasedVersion = 1
  _Version = 0
FEATURE [PartDesign::Fillet] Fillet015
  AddSubType = 0
  Base = -> Pocket019 [Edge97,Edge79,Edge85,Edge91]
  BaseFeature = -> Pocket019
  InvalidShape = false
  NewSolid = false
  Radius = 0.5
  Refine = true
  SupportTransform = false
  Suppress = false
  TreeRank = 0
  UseAllEdges = false
  ValidateShape = true
FEATURE [PartDesign::Body] Body025  label="BodyPartSide"
  AutoGroupSolids = false
  ClaimAllChildren = false
  ExportMode = 0
  Group = -> [Sketch045,DatumPlane004,Pad028,Mirrored,Sketch046,Hole,MultiTransform002,Mirrored001,Mirrored002,Sketch047,Pocket018,MultiTransform003,Chamfer008,Mirrored003,Mirrored004,Sketch048,Pocket019,Fillet015]
  InvalidShape = false
  Origin = -> Origin038
  SingleSolid = true
  Tip = -> Fillet015
  TreeRank = 0
  ValidateShape = true
  _ExportChildren = -> [DatumPlane004,Pad028,Mirrored,Hole,MultiTransform002,Pocket018,MultiTransform003,Chamfer008,Pocket019,Fillet015]
  _GroupVersion = 1
FEATURE [App::Part] Part006  label="PartSideModule"
  ClaimAllChildren = false
  ExportMode = 1
  Group = -> [Body025]
  Origin = -> Origin037
  TreeRank = 0
  _ExportChildren = -> [Body025]
  _GroupVersion = 1
FEATURE [Part::Part2DObjectPython] ShapeString  # Draft 2D object (typed FeaturePython)
  FontFile = <userpath>/Downloads/baveuse/baveuse.ttf
  InvalidShape = false
  Placement = pos=(-35.5,-8,-3) rot=(1,0,0;1.5708rad)
  Size = 5
  String = KARIBOUS
  Tracking = 0
  TreeRank = 0
  ValidateShape = true
FEATURE [Sketcher::SketchObject] Sketch
  ArcFitTolerance = 0
  AttachmentSupport = -> [XZ_Plane]
  ExternalBSplineMaxDegree = 0
  ExternalBSplineTolerance = 0
  FullyConstrained = true
  InternalTolerance = 1e-06
  InvalidShape = false
  MakeInternals = false
  MapMode = 5
  Placement = pos=(0,0,0) rot=(1,0,0;1.5708rad)
  Support = -> [XZ_Plane]
  TreeRank = 0
  ValidateShape = true
  sketch-geometry (4):
    g0: LineSegment StartX=-40 StartY=11 StartZ=0 EndX=40 EndY=11 EndZ=0
    g1: LineSegment StartX=40 StartY=11 StartZ=0 EndX=40 EndY=-7 EndZ=0
    g2: LineSegment StartX=40 StartY=-7 StartZ=0 EndX=-40 EndY=-7 EndZ=0
    g3: LineSegment StartX=-40 StartY=-7 StartZ=0 EndX=-40 EndY=11 EndZ=0
  constraints (11):
    c: Coincident(g0,g1)
    c: Coincident(g1,g2)
    c: Coincident(g2,g3)
    c: Coincident(g3,g0)
    c: Horizontal(g0)
    c: Vertical(g1)
    c: Vertical(g3)
    c: Symmetric(g1,g2,g-2)
    c: DistanceY(g0) = 11
    c: DistanceY(g1,g-1) = 7
    c: DistanceX(g0,g0) = 80
FEATURE [PartDesign::Pad] Pad
  AddSubType = 0
  AutoTaperInnerAngle = false
  CheckUpToFaceLimits = true
  ClaimChildren = false
  Direction = (1,1,1)
  Fit = 0
  FitJoin = 0
  InnerFit = 0
  InnerFitJoin = 0
  InvalidShape = false
  Length = 8
  Length2 = 100
  Linearize = true
  NewSolid = false
  Placement = pos=(0,0,0) rot=(1,0,0;1.5708rad)
  Profile = -> Sketch
  Refine = true
  Suppress = false
  TaperInnerAngle = 0
  TaperInnerAngleRev = 0
  TreeRank = 0
  Type = 0
  ValidateShape = true
  _ProfileBasedVersion = 1
FEATURE [Sketcher::SketchObject] Sketch001
  ArcFitTolerance = 0
  AttachmentSupport = -> [Pad]
  ExternalBSplineMaxDegree = 0
  ExternalBSplineTolerance = 0
  ExternalGeometry = -> [Pad]
  FullyConstrained = true
  InternalTolerance = 1e-06
  InvalidShape = false
  MakeInternals = false
  MapMode = 5
  Placement = pos=(40,0,0) rot=(0.707107,0,0.707107;3.14159rad)
  Support = -> [Pad]
  TreeRank = 0
  ValidateShape = true
  sketch-geometry (4):
    g0: Circle CenterX=-2.5 CenterY=4 CenterZ=0 NormalX=0 NormalY=0 NormalZ=1 AngleXU=0 Radius=2.05
    g1: Circle CenterX=6.5 CenterY=4 CenterZ=0 NormalX=0 NormalY=0 NormalZ=1 AngleXU=0 Radius=2.05
    g2: LineSegment [constr] StartX=-7 StartY=4 StartZ=0 EndX=11 EndY=4 EndZ=0
    g3: LineSegment [constr] StartX=2 StartY=8 StartZ=0 EndX=2 EndY=0 EndZ=0
  constraints (10):
    c: Horizontal(g1,g0)
    c: PointOnObject(g2,g-5)
    c: Horizontal(g2)
    c: PointOnObject(g3,g-1)
    c: Symmetric(g-4,g-4,g2)
    c: Symmetric(g-4,g-5,g3)
    c: Equal(g0,g1)
    c: Symmetric(g0,g1,g3)
    c: Diameter(g1) = 4.1
    c: Symmetric(g-5,g3,g0)
FEATURE [PartDesign::Pocket] Pocket
  AddSubType = 1
  AutoTaperInnerAngle = false
  BaseFeature = -> Pad
  CheckUpToFaceLimits = true
  ClaimChildren = false
  Direction = (1,1,1)
  Fit = 0
  FitJoin = 0
  InnerFit = 0
  InnerFitJoin = 0
  InvalidShape = false
  Length = 12
  Length2 = 100
  Linearize = true
  NewSolid = false
  Placement = pos=(0,0,0) rot=(1,0,0;1.5708rad)
  Profile = -> Sketch001
  Refine = true
  Suppress = false
  TaperInnerAngle = 0
  TaperInnerAngleRev = 0
  TreeRank = 0
  Type = 0
  ValidateShape = true
  _ProfileBasedVersion = 1
  _Version = 1
FEATURE [PartDesign::Mirrored] Mirrored005
  AddSubType = 0
  BaseFeature = -> Pocket
  CopyShape = false
  InvalidShape = false
  MirrorPlane = -> YZ_Plane
  NewSolid = false
  OriginalSubs = -> [Pocket]
  Originals = -> [Pocket]
  ParallelTransform = true
  Placement = pos=(0,0,0) rot=(1,0,0;1.5708rad)
  Refine = true
  SubTransform = true
  Suppress = false
  TreeRank = 0
  ValidateShape = true
  _Version = 3
FEATURE [PartDesign::Chamfer] Chamfer
  AddSubType = 0
  Angle = 45
  Base = -> Mirrored005 [Edge9,Edge8,Edge13,Edge14]
  BaseFeature = -> Mirrored005
  ChamferType = 0
  FlipDirection = false
  InvalidShape = false
  NewSolid = false
  Placement = pos=(0,0,0) rot=(1,0,0;1.5708rad)
  Refine = true
  Size = 0.4
  Size2 = 1
  SupportTransform = false
  Suppress = false
  TreeRank = 0
  UseAllEdges = false
  ValidateShape = true
FEATURE [PartDesign::Chamfer] Chamfer001
  AddSubType = 0
  Angle = 45
  Base = -> Chamfer [Edge11,Edge10,Edge12]
  BaseFeature = -> Chamfer
  ChamferType = 0
  FlipDirection = false
  InvalidShape = false
  NewSolid = false
  Placement = pos=(0,0,0) rot=(1,0,0;1.5708rad)
  Refine = true
  Size = 0.4
  Size2 = 1
  SupportTransform = false
  Suppress = false
  TreeRank = 0
  UseAllEdges = false
  ValidateShape = true
FEATURE [PartDesign::Fillet] Fillet
  AddSubType = 0
  Base = -> Chamfer001 [Edge20]
  BaseFeature = -> Chamfer001
  InvalidShape = false
  NewSolid = false
  Placement = pos=(0,0,0) rot=(1,0,0;1.5708rad)
  Radius = 2
  Refine = true
  SupportTransform = false
  Suppress = false
  TreeRank = 0
  UseAllEdges = false
  ValidateShape = true
FEATURE [PartDesign::Pocket] Pocket001
  AddSubType = 1
  AutoTaperInnerAngle = false
  BaseFeature = -> Fillet
  CheckUpToFaceLimits = true
  ClaimChildren = false
  Direction = (1,1,1)
  Fit = 0
  FitJoin = 0
  InnerFit = 0
  InnerFitJoin = 0
  InvalidShape = false
  Length = 0.5
  Length2 = 100
  Linearize = true
  NewSolid = false
  Placement = pos=(0,0,0) rot=(1,0,0;1.5708rad)
  Profile = -> ShapeString
  Refine = true
  Suppress = false
  TaperInnerAngle = 0
  TaperInnerAngleRev = 0
  TreeRank = 0
  Type = 0
  ValidateShape = true
  _ProfileBasedVersion = 1
  _Version = 1
FEATURE [PartDesign::Body] Body  label="Front"
  AutoGroupSolids = false
  ClaimAllChildren = false
  ExportMode = 0
  Group = -> [Sketch,Pad,Sketch001,Pocket,Mirrored005,Chamfer,Chamfer001,Fillet,ShapeString,Pocket001]
  InvalidShape = false
  Origin = -> Origin
  Placement = pos=(-6.99382e-06,40,0) rot=(0,0,1;3.14159rad)
  SingleSolid = true
  Tip = -> Pocket001
  TreeRank = 0
  ValidateShape = true
  _ExportChildren = -> [Pad,Pocket,Mirrored005,Chamfer,Chamfer001,Fillet,Pocket001]
  _GroupVersion = 1
FEATURE [Sketcher::SketchObject] Sketch058
  ArcFitTolerance = 0
  AttachmentSupport = -> [YZ_Plane034]
  ExternalBSplineMaxDegree = 0
  ExternalBSplineTolerance = 0
  FullyConstrained = true
  InternalTolerance = 1e-06
  InvalidShape = false
  MakeInternals = false
  MapMode = 5
  Placement = pos=(0,0,0) rot=(0.57735,0.57735,0.57735;2.0944rad)
  Support = -> [YZ_Plane034]
  TreeRank = 0
  ValidateShape = true
  sketch-geometry (10):
    g0: LineSegment StartX=-8 StartY=-7 StartZ=0 EndX=-8 EndY=11 EndZ=0
    g1: LineSegment StartX=-8 StartY=11 StartZ=0 EndX=0 EndY=11 EndZ=0
    g2: LineSegment StartX=0 StartY=11 StartZ=0 EndX=47 EndY=7 EndZ=0
    g3: LineSegment StartX=47 StartY=7 StartZ=0 EndX=47 EndY=-7 EndZ=0
    g4: LineSegment StartX=47 StartY=-7 StartZ=0 EndX=-8 EndY=-7 EndZ=0
    g5: Circle CenterX=40 CenterY=0 CenterZ=0 NormalX=0 NormalY=0 NormalZ=1 AngleXU=0 Radius=4
    g6: Circle CenterX=-4 CenterY=6.5 CenterZ=0 NormalX=0 NormalY=0 NormalZ=1 AngleXU=0 Radius=1.6
    g7: Circle CenterX=-4 CenterY=-2.5 CenterZ=0 NormalX=0 NormalY=0 NormalZ=1 AngleXU=0 Radius=1.6
    g8: LineSegment [constr] StartX=-4 StartY=11 StartZ=0 EndX=-4 EndY=-7 EndZ=0
    g9: LineSegment [constr] StartX=-8 StartY=2 StartZ=0 EndX=0 EndY=2 EndZ=0
  constraints (27):
    c: Vertical(g0)
    c: Coincident(g0,g1)
    c: PointOnObject(g1,g-2)
    c: Horizontal(g1)
    c: Coincident(g1,g2)
    c: Coincident(g2,g3)
    c: Coincident(g3,g4)
    c: Coincident(g4,g0)
    c: Horizontal(g4)
    c: DistanceY(g0) = -7
    c: DistanceY(g0) = 11
    c: PointOnObject(g5,g-1)
    c: DistanceX(g5) = 40
    c: Symmetric(g2,g3,g-1)
    c: Diameter(g5) = 8
    c: DistanceX(g2) = 47
    c: DistanceX(g1,g1) = 8
    c: Vertical(g7,g6)
    c: PointOnObject(g8,g4)
    c: Vertical(g8)
    c: PointOnObject(g9,g-2)
    c: Symmetric(g0,g0,g9)
    c: Symmetric(g0,g1,g8)
    c: Symmetric(g6,g7,g9)
    c: Diameter(g6) = 3.2
    c: Equal(g6,g7)
    c: Symmetric(g9,g1,g6)
FEATURE [PartDesign::Pad] Pad032
  AddSubType = 0
  AutoTaperInnerAngle = false
  CheckUpToFaceLimits = true
  ClaimChildren = false
  Direction = (1,1,1)
  Fit = 0
  FitJoin = 0
  InnerFit = 0
  InnerFitJoin = 0
  InvalidShape = false
  Length = 3
  Length2 = 100
  Linearize = true
  NewSolid = false
  Placement = pos=(0,0,0) rot=(0.57735,0.57735,0.57735;2.0944rad)
  Profile = -> Sketch058
  Refine = true
  Suppress = false
  TaperInnerAngle = 0
  TaperInnerAngleRev = 0
  TreeRank = 0
  Type = 0
  ValidateShape = true
  _ProfileBasedVersion = 1
FEATURE [PartDesign::Fillet] Fillet017
  AddSubType = 0
  Base = -> Pad032 [Edge2]
  BaseFeature = -> Pad032
  InvalidShape = false
  NewSolid = false
  Placement = pos=(0,0,0) rot=(0.57735,0.57735,0.57735;2.0944rad)
  Radius = 2
  Refine = true
  SupportTransform = false
  Suppress = false
  TreeRank = 0
  UseAllEdges = false
  ValidateShape = true
FEATURE [PartDesign::Fillet] Fillet020
  AddSubType = 0
  Base = -> Fillet017 [Edge24,Edge15]
  BaseFeature = -> Fillet017
  InvalidShape = false
  NewSolid = false
  Placement = pos=(0,0,0) rot=(0.57735,0.57735,0.57735;2.0944rad)
  Radius = 7.1
  Refine = true
  SupportTransform = false
  Suppress = false
  TreeRank = 0
  UseAllEdges = false
  ValidateShape = true
FEATURE [PartDesign::Chamfer] Chamfer016
  AddSubType = 0
  Angle = 45
  Base = -> Fillet020 [Edge13]
  BaseFeature = -> Fillet020
  ChamferType = 0
  FlipDirection = false
  InvalidShape = false
  NewSolid = false
  Placement = pos=(0,0,0) rot=(0.57735,0.57735,0.57735;2.0944rad)
  Refine = true
  Size = 0.4
  Size2 = 1
  SupportTransform = false
  Suppress = false
  TreeRank = 0
  UseAllEdges = false
  ValidateShape = true
FEATURE [PartDesign::Body] Body027  label="Lateral"
  AutoGroupSolids = false
  ClaimAllChildren = false
  ExportMode = 0
  Group = -> [Sketch058,Pad032,Fillet017,Fillet020,Chamfer016]
  InvalidShape = false
  Origin = -> Origin044
  Placement = pos=(-40,40,0) rot=(0,0,1;3.14159rad)
  SingleSolid = true
  Tip = -> Chamfer016
  TreeRank = 0
  ValidateShape = true
  _ExportChildren = -> [Pad032,Fillet017,Fillet020,Chamfer016]
  _GroupVersion = 1
FEATURE [Sketcher::SketchObject] Sketch059
  ArcFitTolerance = 0
  AttachmentSupport = -> [YZ_Plane035]
  ExternalBSplineMaxDegree = 0
  ExternalBSplineTolerance = 0
  FullyConstrained = true
  InternalTolerance = 1e-06
  InvalidShape = false
  MakeInternals = false
  MapMode = 5
  Placement = pos=(0,0,0) rot=(0.57735,0.57735,0.57735;2.0944rad)
  Support = -> [YZ_Plane035]
  TreeRank = 0
  ValidateShape = true
  sketch-geometry (10):
    g0: LineSegment StartX=-8 StartY=-7 StartZ=0 EndX=-8 EndY=11 EndZ=0
    g1: LineSegment StartX=-8 StartY=11 StartZ=0 EndX=0 EndY=11 EndZ=0
    g2: LineSegment StartX=0 StartY=11 StartZ=0 EndX=47 EndY=7 EndZ=0
    g3: LineSegment StartX=47 StartY=7 StartZ=0 EndX=47 EndY=-7 EndZ=0
    g4: LineSegment StartX=47 StartY=-7 StartZ=0 EndX=-8 EndY=-7 EndZ=0
    g5: Circle CenterX=40 CenterY=0 CenterZ=0 NormalX=0 NormalY=0 NormalZ=1 AngleXU=0 Radius=1.7
    g6: Circle CenterX=-4 CenterY=6.5 CenterZ=0 NormalX=0 NormalY=0 NormalZ=1 AngleXU=0 Radius=1.6
    g7: Circle CenterX=-4 CenterY=-2.5 CenterZ=0 NormalX=0 NormalY=0 NormalZ=1 AngleXU=0 Radius=1.6
    g8: LineSegment [constr] StartX=-4 StartY=11 StartZ=0 EndX=-4 EndY=-7 EndZ=0
    g9: LineSegment [constr] StartX=-8 StartY=2 StartZ=0 EndX=0 EndY=2 EndZ=0
  constraints (27):
    c: Vertical(g0)
    c: Coincident(g0,g1)
    c: PointOnObject(g1,g-2)
    c: Horizontal(g1)
    c: Coincident(g1,g2)
    c: Coincident(g2,g3)
    c: Coincident(g3,g4)
    c: Coincident(g4,g0)
    c: Horizontal(g4)
    c: DistanceY(g0) = -7
    c: DistanceY(g0) = 11
    c: PointOnObject(g5,g-1)
    c: DistanceX(g5) = 40
    c: Symmetric(g2,g3,g-1)
    c: Diameter(g5) = 3.4
    c: DistanceX(g2) = 47
    c: DistanceX(g1,g1) = 8
    c: Vertical(g7,g6)
    c: PointOnObject(g8,g4)
    c: Vertical(g8)
    c: PointOnObject(g9,g-2)
    c: Symmetric(g0,g0,g9)
    c: Symmetric(g0,g1,g8)
    c: Symmetric(g6,g7,g9)
    c: Diameter(g6) = 3.2
    c: Equal(g6,g7)
    c: Symmetric(g9,g1,g6)
FEATURE [PartDesign::Pad] Pad033
  AddSubType = 0
  AutoTaperInnerAngle = false
  CheckUpToFaceLimits = true
  ClaimChildren = false
  Direction = (1,1,1)
  Fit = 0
  FitJoin = 0
  InnerFit = 0
  InnerFitJoin = 0
  InvalidShape = false
  Length = 3
  Length2 = 100
  Linearize = true
  NewSolid = false
  Placement = pos=(0,0,0) rot=(0.57735,0.57735,0.57735;2.0944rad)
  Profile = -> Sketch059
  Refine = true
  Suppress = false
  TaperInnerAngle = 0
  TaperInnerAngleRev = 0
  TreeRank = 0
  Type = 0
  ValidateShape = true
  _ProfileBasedVersion = 1
FEATURE [PartDesign::Fillet] Fillet021
  AddSubType = 0
  Base = -> Pad033 [Edge2]
  BaseFeature = -> Pad033
  InvalidShape = false
  NewSolid = false
  Placement = pos=(0,0,0) rot=(0.57735,0.57735,0.57735;2.0944rad)
  Radius = 2
  Refine = true
  SupportTransform = false
  Suppress = false
  TreeRank = 0
  UseAllEdges = false
  ValidateShape = true
FEATURE [PartDesign::Fillet] Fillet022
  AddSubType = 0
  Base = -> Fillet021 [Edge24,Edge15]
  BaseFeature = -> Fillet021
  InvalidShape = false
  NewSolid = false
  Placement = pos=(0,0,0) rot=(0.57735,0.57735,0.57735;2.0944rad)
  Radius = 7.1
  Refine = true
  SupportTransform = false
  Suppress = false
  TreeRank = 0
  UseAllEdges = false
  ValidateShape = true
FEATURE [PartDesign::Chamfer] Chamfer017
  AddSubType = 0
  Angle = 45
  Base = -> Fillet022 [Edge13]
  BaseFeature = -> Fillet022
  ChamferType = 0
  FlipDirection = false
  InvalidShape = false
  NewSolid = false
  Placement = pos=(0,0,0) rot=(0.57735,0.57735,0.57735;2.0944rad)
  Refine = true
  Size = 0.4
  Size2 = 1
  SupportTransform = false
  Suppress = false
  TreeRank = 0
  UseAllEdges = false
  ValidateShape = true
FEATURE [PartDesign::Body] Body028  label="Lateral001"
  AutoGroupSolids = false
  ClaimAllChildren = false
  ExportMode = 0
  Group = -> [Sketch059,Pad033,Fillet021,Fillet022,Chamfer017]
  InvalidShape = false
  Origin = -> Origin045
  Placement = pos=(-43,40,-8.9e-15) rot=(0,0,1;3.14159rad)
  SingleSolid = true
  Tip = -> Chamfer017
  TreeRank = 0
  ValidateShape = true
  _ExportChildren = -> [Pad033,Fillet021,Fillet022,Chamfer017]
  _GroupVersion = 1
FEATURE [App::Link] Link  label="Link(Lateral)"
  AutoLinkLabel = true
  AutoPlacement = true
  LinkPlacement = pos=(43,40,0) rot=(0,0,1;3.14159rad)
  LinkedObject = -> Body027
  Placement = pos=(43,40,0) rot=(0,0,1;3.14159rad)
  SyncGroupVisibility = false
  TreeRank = 0
  _LinkVersion = 1
FEATURE [App::Link] Link064  label="Link064(Lateral001)"
  AutoLinkLabel = true
  AutoPlacement = true
  LinkPlacement = pos=(46,40,0) rot=(0,0,1;3.14159rad)
  LinkedObject = -> Body028
  Placement = pos=(46,40,0) rot=(0,0,1;3.14159rad)
  SyncGroupVisibility = false
  TreeRank = 0
  _LinkVersion = 1
FEATURE [TechDraw::DrawSVGTemplate] Template
  Height = 210
  Orientation = 1
  TreeRank = 0
  Width = 297
FEATURE [TechDraw::DrawProjGroupItem] ProjItem  label="Front001"
  CoarseView = false
  Direction = (1,0,0)
  Focus = 100
  HardHidden = false
  IsoCount = 0
  IsoHidden = false
  IsoVisible = false
  LockPosition = true
  Perspective = false
  Rotation = 0
  RotationVector = (0,-1,0)
  ScaleType = 2
  ScrubCount = 0
  SeamHidden = false
  SeamVisible = true
  SmoothHidden = false
  SmoothVisible = true
  Source = -> [Chamfer016]
  TreeRank = 0
  Type = 0
  X = 0
  XDirection = (0,-1,0)
  Y = 0
FEATURE [TechDraw::DrawProjGroup] ProjGroup
  Anchor = -> ProjItem
  AutoDistribute = true
  LockPosition = false
  ProjectionType = 0
  Rotation = 0
  ScaleType = 0
  Source = -> [Chamfer016]
  TreeRank = 0
  Views = -> [ProjItem]
  X = 148.5
  Y = 105
  spacingX = 15
  spacingY = 15
FEATURE [TechDraw::DrawProjGroupItem] ProjItem001  label="Front002"
  CoarseView = false
  Direction = (1,0,0)
  Focus = 100
  HardHidden = false
  IsoCount = 0
  IsoHidden = false
  IsoVisible = false
  LockPosition = true
  Perspective = false
  Rotation = 0
  RotationVector = (0,-1,0)
  ScaleType = 2
  ScrubCount = 0
  SeamHidden = false
  SeamVisible = true
  SmoothHidden = false
  SmoothVisible = true
  Source = -> [Chamfer017]
  TreeRank = 0
  Type = 0
  X = 0
  XDirection = (0,-1,0)
  Y = 0
FEATURE [TechDraw::DrawProjGroup] ProjGroup001
  Anchor = -> ProjItem001
  AutoDistribute = true
  LockPosition = false
  ProjectionType = 0
  Rotation = 0
  ScaleType = 0
  Source = -> [Chamfer017]
  TreeRank = 0
  Views = -> [ProjItem001]
  X = 148.5
  Y = 84.6454
  spacingX = 15
  spacingY = 15
FEATURE [TechDraw::DrawPage] Page  label="Laser3mmPoignee"
  KeepUpdated = true
  NextBalloonIndex = 1
  ProjectionType = 0
  Template = -> Template
  TreeRank = 0
  Views = -> [ProjGroup,ProjGroup001]
FEATURE [Part::FeaturePython] Screw  label="M3x12-Screw"  # Fasteners workbench fastener (typed FeaturePython)
  InvalidShape = false
  Placement = pos=(-46,44,6.5) rot=(0,-1,0;1.5708rad)
  TreeRank = 0
  ValidateShape = true
  baseObject = -> Body028 [Edge36]
  diameter = 1
  invert = false
  leftHanded = false
  length = 3
  lengthCustom = 12
  matchOuter = false
  offset = 0
  thread = false
  type = 40
FEATURE [Part::FeaturePython] Screw001  label="M3x12-Screw020"  # Fasteners workbench fastener (typed FeaturePython)
  InvalidShape = false
  Placement = pos=(-46,44,-2.5) rot=(0,-1,0;1.5708rad)
  TreeRank = 0
  ValidateShape = true
  baseObject = -> Body028 [Edge34]
  diameter = 1
  invert = false
  leftHanded = false
  length = 3
  lengthCustom = 12
  matchOuter = false
  offset = 0
  thread = false
  type = 40
FEATURE [Part::FeaturePython] Screw002  label="M3x12-Screw018"  # Fasteners workbench fastener (typed FeaturePython)
  InvalidShape = false
  Placement = pos=(46,44,6.5) rot=(0.707107,0,0.707107;3.14159rad)
  TreeRank = 0
  ValidateShape = true
  diameter = 1
  invert = false
  leftHanded = false
  length = 3
  lengthCustom = 12
  matchOuter = false
  offset = 0
  thread = false
  type = 40
FEATURE [Part::FeaturePython] Screw003  label="M3x12-Screw019"  # Fasteners workbench fastener (typed FeaturePython)
  InvalidShape = false
  Placement = pos=(46,44,-2.5) rot=(0.707107,0,0.707107;3.14159rad)
  TreeRank = 0
  ValidateShape = true
  diameter = 1
  invert = false
  leftHanded = false
  length = 3
  lengthCustom = 12
  matchOuter = false
  offset = 0
  thread = false
  type = 40
FEATURE [App::DocumentObjectGroup] Group001  label="Visserie"
  ClaimAllChildren = true
  ExportMode = 1
  Group = -> [Screw,Screw001,Screw002,Screw003]
  TreeRank = 0
  _GroupVersion = 1
FEATURE [App::Part] Part  label="Poignee"
  ClaimAllChildren = false
  ExportMode = 1
  Group = -> [Body,Body027,Body028,Link,Link064,Screw,Screw001,Screw002,Screw003,Group001]
  Origin = -> Origin043
  TreeRank = 0
  _ExportChildren = -> [Body,Body027,Body028,Link,Link064,Group001]
  _GroupVersion = 1
FEATURE [Sketcher::SketchObject] Sketch060
  ArcFitTolerance = 0
  AttachmentSupport = -> [XY_Plane037]
  ExternalBSplineMaxDegree = 0
  ExternalBSplineTolerance = 0
  FullyConstrained = true
  InternalTolerance = 1e-06
  InvalidShape = false
  MakeInternals = false
  MapMode = 5
  Support = -> [XY_Plane037]
  TreeRank = 0
  ValidateShape = true
  sketch-geometry (10):
    g0: LineSegment [constr] StartX=0 StartY=0 StartZ=0 EndX=34.641 EndY=-20 EndZ=0
    g1: LineSegment [constr] StartX=0 StartY=0 StartZ=0 EndX=-34.641 EndY=-20 EndZ=0
    g2: LineSegment [constr] StartX=-34.641 StartY=-20 StartZ=0 EndX=-14.641 EndY=-54.641 EndZ=0
    g3: LineSegment [constr] StartX=34.641 StartY=-20 StartZ=0 EndX=14.641 EndY=-54.641 EndZ=0
    g4: LineSegment StartX=-14.641 StartY=-54.641 StartZ=0 EndX=-23.3013 EndY=-59.641 EndZ=0
    g5: LineSegment StartX=14.641 StartY=-54.641 StartZ=0 EndX=23.3013 EndY=-59.641 EndZ=0
    g6: LineSegment StartX=-23.3013 StartY=-59.641 StartZ=0 EndX=-15 EndY=-89.641 EndZ=0
    g7: LineSegment StartX=23.3013 StartY=-59.641 StartZ=0 EndX=15 EndY=-89.641 EndZ=0
    g8: LineSegment StartX=-14.641 StartY=-54.641 StartZ=0 EndX=14.641 EndY=-54.641 EndZ=0
    g9: LineSegment StartX=-15 StartY=-89.641 StartZ=0 EndX=15 EndY=-89.641 EndZ=0
  constraints (24):
    c: Coincident(g0,g-1)
    c: Coincident(g1,g0)
    c: Symmetric(g0,g1,g-2)
    c: Angle(g1,g0) = 2.0944
    c: Coincident(g2,g1)
    c: Perpendicular(g1,g2)
    c: Coincident(g3,g0)
    c: Symmetric(g3,g2,g-2)
    c: Distance(g2) = 40
    c: Distance(g0) = 40
    c: Coincident(g4,g2)
    c: Coincident(g5,g3)
    c: Perpendicular(g3,g5)
    c: Symmetric(g4,g5,g-2)
    c: Distance(g5) = 10
    c: Coincident(g6,g4)
    c: Coincident(g7,g5)
    c: Symmetric(g7,g6,g-2)
    c: DistanceY(g7,g3) = 35
    c: Coincident(g8,g4)
    c: Coincident(g8,g5)
    c: Coincident(g9,g6)
    c: Coincident(g9,g7)
    c: DistanceX(g9,g9) = 30
FEATURE [PartDesign::Pad] Pad034
  AddSubType = 0
  AutoTaperInnerAngle = false
  CheckUpToFaceLimits = true
  ClaimChildren = false
  Direction = (1,1,1)
  Fit = 0
  FitJoin = 0
  InnerFit = 0
  InnerFitJoin = 0
  InvalidShape = false
  Length = 50
  Length2 = 100
  Linearize = true
  NewSolid = false
  Profile = -> Sketch060
  Refine = true
  Suppress = false
  TaperInnerAngle = 0
  TaperInnerAngleRev = 0
  TreeRank = 0
  Type = 0
  ValidateShape = true
  _ProfileBasedVersion = 1
FEATURE [Sketcher::SketchObject] Sketch061
  ArcFitTolerance = 0
  AttachmentSupport = -> [YZ_Plane037]
  ExternalBSplineMaxDegree = 0
  ExternalBSplineTolerance = 0
  ExternalGeometry = -> [Pad034]
  FullyConstrained = true
  InternalTolerance = 1e-06
  InvalidShape = false
  MakeInternals = false
  MapMode = 5
  Placement = pos=(0,0,0) rot=(0.57735,0.57735,0.57735;2.0944rad)
  Support = -> [YZ_Plane037]
  TreeRank = 0
  ValidateShape = true
  sketch-geometry (4):
    g0: LineSegment StartX=-62.641 StartY=0 StartZ=0 EndX=-89.641 EndY=20.6315 EndZ=0
    g1: LineSegment StartX=-62.641 StartY=0 StartZ=0 EndX=-89.641 EndY=0 EndZ=0
    g2: LineSegment StartX=-89.641 StartY=0 StartZ=0 EndX=-89.641 EndY=20.6315 EndZ=0
    g3: LineSegment [constr] StartX=-89.641 StartY=20.6315 StartZ=0 EndX=-54.641 EndY=50 EndZ=0
  constraints (11):
    c: PointOnObject(g0,g-4)
    c: PointOnObject(g0,g-1)
    c: DistanceX(g0,g-3) = 3
    c: Coincident(g0,g1)
    c: PointOnObject(g1,g-4)
    c: Horizontal(g1)
    c: Coincident(g1,g2)
    c: Coincident(g2,g0)
    c: Coincident(g3,g0)
    c: Coincident(g3,g-5)
    c: Angle(g-4,g3) = 2.26893
FEATURE [PartDesign::Pocket] Pocket025
  AddSubType = 1
  AutoTaperInnerAngle = false
  BaseFeature = -> Pad034
  CheckUpToFaceLimits = true
  ClaimChildren = false
  Direction = (1,1,1)
  Fit = 0
  FitJoin = 0
  InnerFit = 0
  InnerFitJoin = 0
  InvalidShape = false
  Length = 5
  Length2 = 100
  Linearize = true
  Midplane = true
  NewSolid = false
  Profile = -> Sketch061
  Refine = true
  Suppress = false
  TaperInnerAngle = 0
  TaperInnerAngleRev = 0
  TreeRank = 0
  Type = 1
  ValidateShape = true
  _ProfileBasedVersion = 1
  _Version = 1
FEATURE [Sketcher::SketchObject] Sketch062
  ArcFitTolerance = 0
  AttachmentSupport = -> [YZ_Plane037]
  ExternalBSplineMaxDegree = 0
  ExternalBSplineTolerance = 0
  ExternalGeometry = -> [Pocket025]
  FullyConstrained = true
  InternalTolerance = 1e-06
  InvalidShape = false
  MakeInternals = false
  MapMode = 5
  Placement = pos=(0,0,0) rot=(0.57735,0.57735,0.57735;2.0944rad)
  Support = -> [YZ_Plane037]
  TreeRank = 0
  ValidateShape = true
  sketch-geometry (3):
    g0: LineSegment StartX=-89.641 StartY=50 StartZ=0 EndX=-89.641 EndY=20.6315 EndZ=0
    g1: LineSegment StartX=-89.641 StartY=20.6315 StartZ=0 EndX=-54.641 EndY=50 EndZ=0
    g2: LineSegment StartX=-89.641 StartY=50 StartZ=0 EndX=-54.641 EndY=50 EndZ=0
  constraints (6):
    c: Coincident(g1,g0)
    c: Coincident(g-3,g0)
    c: Coincident(g-3,g0)
    c: Coincident(g2,g0)
    c: Coincident(g2,g1)
    c: Coincident(g1,g-5)
FEATURE [PartDesign::Pocket] Pocket026
  AddSubType = 1
  AutoTaperInnerAngle = false
  BaseFeature = -> Pocket025
  CheckUpToFaceLimits = true
  ClaimChildren = false
  Direction = (1,1,1)
  Fit = 0
  FitJoin = 0
  InnerFit = 0
  InnerFitJoin = 0
  InvalidShape = false
  Length = 5
  Length2 = 100
  Linearize = true
  Midplane = true
  NewSolid = false
  Profile = -> Sketch062
  Refine = true
  Suppress = false
  TaperInnerAngle = 0
  TaperInnerAngleRev = 0
  TreeRank = 0
  Type = 1
  ValidateShape = true
  _ProfileBasedVersion = 1
  _Version = 1
FEATURE [PartDesign::Plane] DatumPlane
  AttachmentOffset = pos=(0,0,-30) rot=(0,0,1;0rad)
  AttachmentSupport = -> [Pocket026]
  InvalidShape = false
  Length = 68.3013
  MapMode = 5
  MinimumLength = 10
  MinimumWidth = 10
  Placement = pos=(-35,-60.6218,3.3e-15) rot=(0.186157,0.694747,0.694747;2.77349rad)
  ResizeMode = 0
  Support = -> [Pocket026]
  TreeRank = 0
  ValidateShape = true
  Width = 10
FEATURE [Sketcher::SketchObject] Sketch063
  ArcFitTolerance = 0
  AttachmentSupport = -> [DatumPlane]
  ExternalBSplineMaxDegree = 0
  ExternalBSplineTolerance = 0
  ExternalGeometry = -> [Pocket026]
  FullyConstrained = true
  InternalTolerance = 1e-06
  InvalidShape = false
  MakeInternals = false
  MapMode = 5
  Placement = pos=(-35,-60.6218,3.3e-15) rot=(0.186157,0.694747,0.694747;2.77349rad)
  Support = -> [DatumPlane]
  TreeRank = 0
  ValidateShape = true
  sketch-geometry (2):
    g0: Circle CenterX=-45 CenterY=10 CenterZ=0 NormalX=0 NormalY=0 NormalZ=1 AngleXU=0 Radius=1.6
    g1: LineSegment [constr] StartX=-50 StartY=10 StartZ=0 EndX=-40 EndY=10 EndZ=0
  constraints (6):
    c: PointOnObject(g1,g-3)
    c: PointOnObject(g1,g-4)
    c: Horizontal(g1)
    c: Symmetric(g1,g1,g0)
    c: Diameter(g0) = 3.2
    c: Distance(g-3,g1) = 10
FEATURE [PartDesign::Hole] Hole001
  AddSubType = 1
  BaseFeature = -> Pocket026
  ClaimChildren = false
  CustomThreadClearance = 0
  Depth = 39
  DepthType = 0
  Diameter = 3.2
  DrillForDepth = false
  DrillPoint = 1
  DrillPointAngle = 118
  Fit = 0
  FitJoin = 0
  HoleCutCountersinkAngle = 90
  HoleCutCustomValues = true
  HoleCutDepth = 27
  HoleCutDiameter = 8
  HoleCutType = 1
  InnerFit = 0
  InnerFitJoin = 0
  InvalidShape = false
  ModelThread = false
  NewSolid = false
  Profile = -> Sketch063
  Refine = true
  Reversed = true
  Suppress = false
  Tapered = false
  TaperedAngle = 90
  ThreadClass = 0
  ThreadDepth = 39
  ThreadDepthType = 0
  ThreadDirection = 0
  ThreadFit = 0
  ThreadSize = 0
  ThreadType = 0
  Threaded = false
  TreeRank = 0
  UseCustomThreadClearance = false
  ValidateShape = true
  _ProfileBasedVersion = 1
FEATURE [PartDesign::Mirrored] Mirrored006
  AddSubType = 0
  BaseFeature = -> Hole001
  CopyShape = false
  InvalidShape = false
  MirrorPlane = -> YZ_Plane037
  NewSolid = false
  OriginalSubs = -> [Hole001]
  Originals = -> [Hole001]
  ParallelTransform = true
  Refine = true
  SubTransform = true
  Suppress = false
  TreeRank = 0
  ValidateShape = true
  _Version = 3
FEATURE [Sketcher::SketchObject] Sketch064
  ArcFitTolerance = 0
  AttachmentSupport = -> [Mirrored006]
  ExternalBSplineMaxDegree = 0
  ExternalBSplineTolerance = 0
  ExternalGeometry = -> [Mirrored006]
  FullyConstrained = true
  InternalTolerance = 1e-06
  InvalidShape = false
  MakeInternals = false
  MapMode = 5
  Placement = pos=(-2.64e-14,-47.1965,56.2467) rot=(1,0,0;0.698132rad)
  Support = -> [Mirrored006]
  TreeRank = 0
  ValidateShape = true
  sketch-geometry (2):
    g0: Circle CenterX=-14 CenterY=-14.7181 CenterZ=0 NormalX=0 NormalY=0 NormalZ=1 AngleXU=0 Radius=2.05
    g1: Circle CenterX=14 CenterY=-14.7181 CenterZ=0 NormalX=0 NormalY=0 NormalZ=1 AngleXU=0 Radius=2.05
  constraints (5):
    c: Symmetric(g1,g0,g-2)
    c: Diameter(g0) = 4.1
    c: Equal(g0,g1)
    c: DistanceX(g0,g1) = 28
    c: DistanceY(g0,g-3) = 5
FEATURE [PartDesign::Pocket] Pocket027
  AddSubType = 1
  AutoTaperInnerAngle = false
  BaseFeature = -> Mirrored006
  CheckUpToFaceLimits = true
  ClaimChildren = false
  Direction = (1,1,1)
  Fit = 0
  FitJoin = 0
  InnerFit = 0
  InnerFitJoin = 0
  InvalidShape = false
  Length = 5
  Length2 = 100
  Linearize = true
  NewSolid = false
  Profile = -> Sketch064
  Refine = true
  Suppress = false
  TaperInnerAngle = 0
  TaperInnerAngleRev = 0
  TreeRank = 0
  Type = 1
  ValidateShape = true
  _ProfileBasedVersion = 1
  _Version = 1
FEATURE [Sketcher::SketchObject] Sketch065
  ArcFitTolerance = 0
  AttachmentSupport = -> [Pocket027]
  ExternalBSplineMaxDegree = 0
  ExternalBSplineTolerance = 0
  ExternalGeometry = -> [Pocket027]
  FullyConstrained = true
  InternalTolerance = 1e-06
  InvalidShape = false
  MakeInternals = false
  MapMode = 5
  Placement = pos=(-2.64e-14,-47.1965,56.2467) rot=(1,0,0;0.698132rad)
  Support = -> [Pocket027]
  TreeRank = 0
  ValidateShape = true
  sketch-geometry (3):
    g0: Circle CenterX=0 CenterY=-32.5627 CenterZ=0 NormalX=0 NormalY=0 NormalZ=1 AngleXU=0 Radius=15
    g1: GeomPoint [constr] X=2e-16 Y=-55.4073 Z=0
    g2: GeomPoint [constr] X=0 Y=-9.71807 Z=0
  constraints (6):
    c: PointOnObject(g0,g-2)
    c: Diameter(g0) = 30
    c: PointOnObject(g2,g-2)
    c: PointOnObject(g2,g-3)
    c: PointOnObject(g1,g-4)
    c: Symmetric(g1,g2,g0)
FEATURE [PartDesign::Pocket] Pocket028
  AddSubType = 1
  AutoTaperInnerAngle = false
  BaseFeature = -> Pocket027
  CheckUpToFaceLimits = true
  ClaimChildren = false
  Direction = (1,1,1)
  Fit = 0
  FitJoin = 0
  InnerFit = 0
  InnerFitJoin = 0
  InvalidShape = false
  Length = 17
  Length2 = 100
  Linearize = true
  NewSolid = false
  Profile = -> Sketch065
  Refine = true
  Suppress = false
  TaperInnerAngle = 0
  TaperInnerAngleRev = 0
  TreeRank = 0
  Type = 0
  ValidateShape = true
  _ProfileBasedVersion = 1
  _Version = 1
FEATURE [Sketcher::SketchObject] Sketch066
  ArcFitTolerance = 0
  AttachmentSupport = -> [Pocket028]
  ExternalBSplineMaxDegree = 0
  ExternalBSplineTolerance = 0
  ExternalGeometry = -> [Pocket028]
  FullyConstrained = true
  InternalTolerance = 1e-06
  InvalidShape = false
  MakeInternals = false
  MapMode = 5
  Placement = pos=(-2.64e-14,-47.1965,56.2467) rot=(1,0,0;0.698132rad)
  Support = -> [Pocket028]
  TreeRank = 0
  ValidateShape = true
  sketch-geometry (4):
    g0: ArcOfCircle CenterX=0 CenterY=-32.5627 CenterZ=0 NormalX=0 NormalY=0 NormalZ=1 AngleXU=0 Radius=11.5 StartAngle=3.22982 EndAngle=6.19496
    g1: LineSegment StartX=-11.4553 StartY=-33.576 StartZ=0 EndX=-12.3039 EndY=-23.9828 EndZ=0
    g2: LineSegment StartX=12.3039 StartY=-23.9828 StartZ=0 EndX=11.4553 EndY=-33.576 EndZ=0
    g3: LineSegment StartX=-12.3039 StartY=-23.9828 StartZ=0 EndX=12.3039 EndY=-23.9828 EndZ=0
  constraints (8):
    c: Coincident(g0,g-3)
    c: Diameter(g0) = 23
    c: Coincident(g1,g-4)
    c: Coincident(g2,g-4)
    c: Coincident(g3,g1)
    c: Coincident(g3,g2)
    c: Tangent(g1,g0) = 1.5708
    c: Tangent(g2,g0) = 1.5708
FEATURE [PartDesign::Pocket] Pocket029
  AddSubType = 1
  AutoTaperInnerAngle = false
  BaseFeature = -> Pocket028
  CheckUpToFaceLimits = true
  ClaimChildren = false
  Direction = (1,1,1)
  Fit = 0
  FitJoin = 0
  InnerFit = 0
  InnerFitJoin = 0
  InvalidShape = false
  Length = 5
  Length2 = 100
  Linearize = true
  NewSolid = false
  Profile = -> Sketch066
  Refine = true
  Suppress = false
  TaperInnerAngle = 0
  TaperInnerAngleRev = 0
  TreeRank = 0
  Type = 1
  ValidateShape = true
  _ProfileBasedVersion = 1
  _Version = 1
FEATURE [PartDesign::Chamfer] Chamfer018
  AddSubType = 0
  Angle = 45
  Base = -> Pocket029 [Edge44,Edge31]
  BaseFeature = -> Pocket029
  ChamferType = 0
  FlipDirection = false
  InvalidShape = false
  NewSolid = false
  Refine = true
  Size = 0.4
  Size2 = 1
  SupportTransform = false
  Suppress = false
  TreeRank = 0
  UseAllEdges = false
  ValidateShape = true
FEATURE [App::Link] Link065  label="Link065(CoinStandard)"
  AutoLinkLabel = true
  AutoPlacement = true
  LinkedObject = -> Body029
  SyncGroupVisibility = false
  TreeRank = 0
  _LinkVersion = 1
FEATURE [PartDesign::SubShapeBinder] Binder  label="Binder(Chamfer023)"
  BindCopyOnChange = 0
  BindMode = 0
  ClaimChildren = false
  Context = -> Part010 [Body030.Binder.]
  EdgeTolerance = 1e-06
  FillStyle = 0
  Fuse = false
  InvalidShape = false
  MakeFace = true
  MergeEdges = true
  OffsetFill = false
  OffsetIntersection = false
  OffsetJoinType = 0
  OffsetOpenResult = false
  Outline = false
  PartialLoad = false
  Refine = true
  Relative = true
  SplitEdges = false
  Support = -> [Chamfer023[Face30]]
  TightBound = false
  TreeRank = 0
  ValidateShape = true
  _Version = 8
FEATURE [Sketcher::SketchObject] Sketch067
  ArcFitTolerance = 0
  AttachmentSupport = -> [Binder]
  ExternalBSplineMaxDegree = 0
  ExternalBSplineTolerance = 0
  ExternalGeometry = -> [Binder]
  FullyConstrained = true
  InternalTolerance = 1e-06
  InvalidShape = false
  MakeInternals = false
  MapMode = 5
  Placement = pos=(-2.82e-14,-50.4105,60.0769) rot=(1,0,0;0.698132rad)
  Support = -> [Binder]
  TreeRank = 0
  ValidateShape = true
  sketch-geometry (3):
    g0: Circle CenterX=-2e-16 CenterY=-32.5627 CenterZ=0 NormalX=0 NormalY=0 NormalZ=1 AngleXU=0 Radius=8
    g1: Circle CenterX=14 CenterY=-14.7181 CenterZ=0 NormalX=0 NormalY=0 NormalZ=1 AngleXU=0 Radius=1.6
    g2: Circle CenterX=-14 CenterY=-14.7181 CenterZ=0 NormalX=0 NormalY=0 NormalZ=1 AngleXU=0 Radius=1.6
  constraints (6):
    c: Coincident(g0,g-9)
    c: Diameter(g0) = 16
    c: Coincident(g1,g-10)
    c: Coincident(g2,g-11)
    c: Diameter(g2) = 3.2
    c: Equal(g2,g1)
FEATURE [PartDesign::Pad] Pad035
  AddSubType = 0
  AutoTaperInnerAngle = false
  CheckUpToFaceLimits = true
  ClaimChildren = false
  Direction = (-4e-16,-0.642788,0.766044)
  Fit = 0
  FitJoin = 0
  InnerFit = 0
  InnerFitJoin = 0
  InvalidShape = false
  Length = 3
  Length2 = 100
  Linearize = true
  NewSolid = false
  Profile = -> Sketch067
  Refine = true
  Suppress = false
  TaperInnerAngle = 0
  TaperInnerAngleRev = 0
  TreeRank = 0
  Type = 0
  ValidateShape = true
  _ProfileBasedVersion = 1
FEATURE [PartDesign::Chamfer] Chamfer021
  AddSubType = 0
  Angle = 45
  Base = -> Pad035 [Edge8,Edge11,Edge5,Edge1,Edge14,Edge2]
  BaseFeature = -> Pad035
  ChamferType = 0
  FlipDirection = false
  InvalidShape = false
  NewSolid = false
  Refine = true
  Size = 0.4
  Size2 = 1
  SupportTransform = false
  Suppress = false
  TreeRank = 0
  UseAllEdges = false
  ValidateShape = true
FEATURE [PartDesign::Body] Body030  label="PlateBAU"
  AutoGroupSolids = false
  ClaimAllChildren = false
  ExportMode = 0
  Group = -> [Binder,Sketch067,Pad035,Chamfer021]
  InvalidShape = false
  Origin = -> Origin048
  SingleSolid = true
  Tip = -> Chamfer021
  TreeRank = 0
  ValidateShape = true
  _ExportChildren = -> [Binder,Pad035,Chamfer021]
  _GroupVersion = 1
FEATURE [TechDraw::DrawSVGTemplate] Template001
  Height = 210
  Orientation = 1
  TreeRank = 0
  Width = 297
FEATURE [TechDraw::DrawProjGroupItem] ProjItem002  label="Front003"
  CoarseView = false
  Direction = (0,-0.643,0.766)
  Focus = 100
  HardHidden = false
  IsoCount = 0
  IsoHidden = false
  IsoVisible = false
  LockPosition = true
  Perspective = false
  Rotation = 0
  RotationVector = (-1,0,0)
  ScaleType = 2
  ScrubCount = 0
  SeamHidden = false
  SeamVisible = true
  SmoothHidden = false
  SmoothVisible = true
  Source = -> [Chamfer021]
  TreeRank = 0
  Type = 0
  X = 0
  XDirection = (-1,0,0)
  Y = 0
FEATURE [TechDraw::DrawProjGroup] ProjGroup002
  Anchor = -> ProjItem002
  AutoDistribute = true
  LockPosition = false
  ProjectionType = 0
  Rotation = 0
  ScaleType = 0
  Source = -> [Chamfer021]
  TreeRank = 0
  Views = -> [ProjItem002]
  X = 23.7819
  Y = 186.665
  spacingX = 15
  spacingY = 15
FEATURE [TechDraw::DrawPage] Page001  label="Laser3mmPlateBau"
  KeepUpdated = true
  NextBalloonIndex = 1
  ProjectionType = 0
  Template = -> Template001
  TreeRank = 0
  Views = -> [ProjGroup002]
FEATURE [PartDesign::Pad] Pad036
  AddSubType = 0
  AutoTaperInnerAngle = false
  BaseFeature = -> Chamfer018
  CheckUpToFaceLimits = true
  ClaimChildren = false
  Direction = (1,1,1)
  Fit = 0
  FitJoin = 0
  InnerFit = 0
  InnerFitJoin = 0
  InvalidShape = false
  Length = 5
  Length2 = 100
  Linearize = true
  NewSolid = false
  Profile = -> Chamfer018 [Face5]
  Refine = true
  Suppress = false
  TaperInnerAngle = 0
  TaperInnerAngleRev = 0
  TreeRank = 0
  Type = 0
  ValidateShape = true
  _ProfileBasedVersion = 1
FEATURE [PartDesign::Chamfer] Chamfer022
  AddSubType = 0
  Angle = 45
  Base = -> Pad036 [Face15]
  BaseFeature = -> Pad036
  ChamferType = 0
  FlipDirection = false
  InvalidShape = false
  NewSolid = false
  Refine = true
  Size = 0.4
  Size2 = 1
  SupportTransform = false
  Suppress = false
  TreeRank = 0
  UseAllEdges = false
  ValidateShape = true
FEATURE [PartDesign::Chamfer] Chamfer023
  AddSubType = 0
  Angle = 45
  Base = -> Chamfer022 [Edge64,Edge63]
  BaseFeature = -> Chamfer022
  ChamferType = 0
  FlipDirection = false
  InvalidShape = false
  NewSolid = false
  Refine = true
  Size = 1
  Size2 = 1
  SupportTransform = false
  Suppress = false
  TreeRank = 0
  UseAllEdges = false
  ValidateShape = true
FEATURE [PartDesign::Body] Body029  label="CoinStandard"
  AutoGroupSolids = false
  ClaimAllChildren = false
  ExportMode = 0
  Group = -> [Sketch060,Pad034,Sketch061,Pocket025,Sketch062,Pocket026,DatumPlane,Sketch063,Hole001,Mirrored006,Sketch064,Pocket027,Sketch065,Pocket028,Sketch066,Pocket029,Chamfer018,Pad036,Chamfer022,Chamfer023]
  InvalidShape = false
  Origin = -> Origin046
  SingleSolid = true
  Tip = -> Chamfer023
  TreeRank = 0
  ValidateShape = true
  _ExportChildren = -> [Pad034,Pocket025,Pocket026,DatumPlane,Hole001,Mirrored006,Pocket027,Pocket028,Pocket029,Chamfer018,Pad036,Chamfer022,Chamfer023]
  _GroupVersion = 1
FEATURE [App::Link] Link066  label="Link066(CoinStandard)"
  AutoLinkLabel = true
  AutoPlacement = true
  LinkedObject = -> Body029
  SyncGroupVisibility = false
  TreeRank = 0
  _LinkVersion = 1
FEATURE [PartDesign::FeatureBase] Clone
  BaseFeature = -> Body030
  InvalidShape = false
  NewSolid = false
  Suppress = false
  TreeRank = 0
  ValidateShape = true
FEATURE [Sketcher::SketchObject] Sketch068
  ArcFitTolerance = 0
  AttachmentSupport = -> [Clone]
  ExternalBSplineMaxDegree = 0
  ExternalBSplineTolerance = 0
  ExternalGeometry = -> [Clone]
  FullyConstrained = true
  InternalTolerance = 1e-06
  InvalidShape = false
  MakeInternals = false
  MapMode = 5
  Placement = pos=(-3.09e-14,-52.3388,62.375) rot=(1,0,0;0.698132rad)
  Support = -> [Clone]
  TreeRank = 0
  ValidateShape = true
  sketch-geometry (2):
    g0: Circle CenterX=0 CenterY=-32.5627 CenterZ=0 NormalX=0 NormalY=0 NormalZ=1 AngleXU=0 Radius=3
    g1: Circle CenterX=0 CenterY=-32.5627 CenterZ=0 NormalX=0 NormalY=0 NormalZ=1 AngleXU=0 Radius=15
  constraints (4):
    c: Coincident(g0,g-3)
    c: Coincident(g1,g0)
    c: Diameter(g1) = 30
    c: Diameter(g0) = 6
FEATURE [PartDesign::Pad] Pad037
  AddSubType = 0
  AutoTaperInnerAngle = false
  BaseFeature = -> Clone
  CheckUpToFaceLimits = true
  ClaimChildren = false
  Direction = (-4e-16,-0.642788,0.766044)
  Fit = 0
  FitJoin = 0
  InnerFit = 0
  InnerFitJoin = 0
  InvalidShape = false
  Length = 10
  Length2 = 100
  Linearize = true
  NewSolid = false
  Profile = -> Sketch068
  Refine = true
  Suppress = false
  TaperInnerAngle = 0
  TaperInnerAngleRev = 0
  TreeRank = 0
  Type = 3
  UpToFace = -> Clone [Face2]
  ValidateShape = true
  _ProfileBasedVersion = 1
FEATURE [PartDesign::Body] Body032  label="PlateTirette_1"
  AutoGroupSolids = false
  BaseFeature = -> Body030
  ClaimAllChildren = false
  ExportMode = 0
  Group = -> [Clone,Sketch068,Pad037]
  InvalidShape = false
  Origin = -> Origin051
  SingleSolid = true
  Tip = -> Pad037
  TreeRank = 0
  ValidateShape = true
  _ExportChildren = -> [Clone,Pad037]
  _GroupVersion = 1
FEATURE [PartDesign::SubShapeBinder] Binder001  label="Binder001(Pad037)"
  BindCopyOnChange = 0
  BindMode = 2
  ClaimChildren = false
  Context = -> Part011 [Body033.Binder001.]
  EdgeTolerance = 1e-06
  FillStyle = 0
  Fuse = false
  InvalidShape = false
  MakeFace = true
  MergeEdges = true
  OffsetFill = false
  OffsetIntersection = false
  OffsetJoinType = 0
  OffsetOpenResult = false
  Outline = false
  PartialLoad = false
  Refine = true
  Relative = true
  SplitEdges = false
  TightBound = false
  TreeRank = 0
  ValidateShape = true
  _Version = 8
FEATURE [PartDesign::Pad] Pad038
  AddSubType = 0
  AutoTaperInnerAngle = false
  CheckUpToFaceLimits = true
  ClaimChildren = false
  Direction = (-4e-16,-0.642788,0.766044)
  Fit = 0
  FitJoin = 0
  InnerFit = 0
  InnerFitJoin = 0
  InvalidShape = false
  Length = 3
  Length2 = 100
  Linearize = true
  NewSolid = false
  Profile = -> Binder001
  Refine = true
  Suppress = false
  TaperInnerAngle = 0
  TaperInnerAngleRev = 0
  TreeRank = 0
  Type = 0
  ValidateShape = true
  _ProfileBasedVersion = 1
FEATURE [Sketcher::SketchObject] Sketch069
  ArcFitTolerance = 0
  AttachmentSupport = -> [Pad038]
  ExternalBSplineMaxDegree = 0
  ExternalBSplineTolerance = 0
  ExternalGeometry = -> [Pad038]
  FullyConstrained = true
  InternalTolerance = 1e-06
  InvalidShape = false
  MakeInternals = false
  MapMode = 5
  Placement = pos=(-3.46e-14,-54.2672,64.6731) rot=(1,0,0;0.698132rad)
  Support = -> [Pad038]
  TreeRank = 0
  ValidateShape = true
  sketch-geometry (1):
    g0: Circle CenterX=0 CenterY=-32.5627 CenterZ=0 NormalX=0 NormalY=0 NormalZ=1 AngleXU=0 Radius=12
  constraints (2):
    c: Coincident(g0,g-3)
    c: Diameter(g0) = 24
FEATURE [PartDesign::Pocket] Pocket030
  AddSubType = 1
  AutoTaperInnerAngle = false
  BaseFeature = -> Pad038
  CheckUpToFaceLimits = true
  ClaimChildren = false
  Direction = (1,1,1)
  Fit = 0
  FitJoin = 0
  InnerFit = 0
  InnerFitJoin = 0
  InvalidShape = false
  Length = 5
  Length2 = 100
  Linearize = true
  NewSolid = false
  Profile = -> Sketch069
  Refine = true
  Suppress = false
  TaperInnerAngle = 0
  TaperInnerAngleRev = 0
  TreeRank = 0
  Type = 1
  ValidateShape = true
  _ProfileBasedVersion = 1
  _Version = 1
FEATURE [PartDesign::Body] Body033  label="PlateTirette_2"
  AutoGroupSolids = false
  ClaimAllChildren = false
  ExportMode = 0
  Group = -> [Binder001,Pad038,Sketch069,Pocket030]
  InvalidShape = false
  Origin = -> Origin052
  SingleSolid = true
  Tip = -> Pocket030
  TreeRank = 0
  ValidateShape = true
  _ExportChildren = -> [Pad038,Pocket030]
  _GroupVersion = 1
FEATURE [PartDesign::SubShapeBinder] Binder002  label="Binder002(Pocket030)"
  BindCopyOnChange = 0
  BindMode = 0
  ClaimChildren = false
  Context = -> Part011 [Body034.Binder002.]
  EdgeTolerance = 1e-06
  FillStyle = 0
  Fuse = false
  InvalidShape = false
  MakeFace = true
  MergeEdges = true
  OffsetFill = false
  OffsetIntersection = false
  OffsetJoinType = 0
  OffsetOpenResult = false
  Outline = false
  PartialLoad = false
  Refine = true
  Relative = true
  SplitEdges = false
  Support = -> [Body033[Pocket030.Face5]]
  TightBound = false
  TreeRank = 0
  ValidateShape = true
  _Version = 8
FEATURE [PartDesign::Pad] Pad039
  AddSubType = 0
  AutoTaperInnerAngle = false
  CheckUpToFaceLimits = true
  ClaimChildren = false
  Direction = (-4e-16,-0.642788,0.766044)
  Fit = 0
  FitJoin = 0
  InnerFit = 0
  InnerFitJoin = 0
  InvalidShape = false
  Length = 0.8
  Length2 = 100
  Linearize = true
  NewSolid = false
  Profile = -> Binder002
  Refine = true
  Suppress = false
  TaperInnerAngle = 0
  TaperInnerAngleRev = 0
  TreeRank = 0
  Type = 0
  ValidateShape = true
  _ProfileBasedVersion = 1
FEATURE [Sketcher::SketchObject] Sketch070
  ArcFitTolerance = 0
  AttachmentSupport = -> [Pad039]
  ExternalBSplineMaxDegree = 0
  ExternalBSplineTolerance = 0
  ExternalGeometry = -> [Pad039]
  FullyConstrained = true
  InternalTolerance = 1e-06
  InvalidShape = false
  MakeInternals = false
  MapMode = 5
  Placement = pos=(-3.49e-14,-54.7814,65.286) rot=(1,0,0;0.698132rad)
  Support = -> [Pad039]
  TreeRank = 0
  ValidateShape = true
  sketch-geometry (1):
    g0: Circle CenterX=0 CenterY=-32.5627 CenterZ=0 NormalX=0 NormalY=0 NormalZ=1 AngleXU=0 Radius=15
  constraints (2):
    c: Coincident(g0,g-3)
    c: Diameter(g0) = 30
FEATURE [PartDesign::Pad] Pad040
  AddSubType = 0
  AutoTaperInnerAngle = false
  BaseFeature = -> Pad039
  CheckUpToFaceLimits = true
  ClaimChildren = false
  Direction = (-4e-16,-0.642788,0.766044)
  Fit = 0
  FitJoin = 0
  InnerFit = 0
  InnerFitJoin = 0
  InvalidShape = false
  Length = 10
  Length2 = 100
  Linearize = true
  NewSolid = false
  Profile = -> Sketch070
  Refine = true
  Reversed = true
  Suppress = false
  TaperInnerAngle = 0
  TaperInnerAngleRev = 0
  TreeRank = 0
  Type = 3
  UpToFace = -> Pad039 [Face16]
  ValidateShape = true
  _ProfileBasedVersion = 1
FEATURE [PartDesign::Body] Body034  label="InterPlateTirette"
  AutoGroupSolids = false
  ClaimAllChildren = false
  ExportMode = 0
  Group = -> [Binder002,Pad039,Sketch070,Pad040]
  InvalidShape = false
  Origin = -> Origin053
  SingleSolid = true
  Tip = -> Pad040
  TreeRank = 0
  ValidateShape = true
  _ExportChildren = -> [Pad039,Pad040]
  _GroupVersion = 1
FEATURE [PartDesign::SubShapeBinder] Binder003  label="Binder003(Pad040)"
  BindCopyOnChange = 0
  BindMode = 2
  ClaimChildren = false
  Context = -> Part011 [Body035.Binder003.]
  EdgeTolerance = 1e-06
  FillStyle = 0
  Fuse = false
  InvalidShape = false
  MakeFace = true
  MergeEdges = true
  OffsetFill = false
  OffsetIntersection = false
  OffsetJoinType = 0
  OffsetOpenResult = false
  Outline = false
  PartialLoad = false
  Refine = true
  Relative = true
  SplitEdges = false
  TightBound = false
  TreeRank = 0
  ValidateShape = true
  _Version = 8
FEATURE [PartDesign::Pad] Pad041
  AddSubType = 0
  AutoTaperInnerAngle = false
  CheckUpToFaceLimits = true
  ClaimChildren = false
  Direction = (-4e-16,-0.642788,0.766044)
  Fit = 0
  FitJoin = 0
  InnerFit = 0
  InnerFitJoin = 0
  InvalidShape = false
  Length = 3
  Length2 = 100
  Linearize = true
  NewSolid = false
  Profile = -> Binder003
  Refine = true
  Suppress = false
  TaperInnerAngle = 0
  TaperInnerAngleRev = 0
  TreeRank = 0
  Type = 0
  ValidateShape = true
  _ProfileBasedVersion = 1
FEATURE [Part::SubShapeBinder] Import  label="Import(Pocket030)"
  BindCopyOnChange = 0
  BindMode = 0
  ClaimChildren = false
  Context = -> Part011 [Body035.Import.]
  EdgeTolerance = 1e-06
  FillStyle = 0
  Fuse = false
  InvalidShape = false
  MakeFace = false
  MergeEdges = true
  OffsetFill = false
  OffsetIntersection = false
  OffsetJoinType = 0
  OffsetOpenResult = false
  Outline = false
  PartialLoad = false
  Refine = true
  Relative = true
  SplitEdges = false
  Support = -> [Body033[Pocket030.]]
  TightBound = false
  TreeRank = 0
  ValidateShape = true
  _Version = 8
FEATURE [Sketcher::SketchObject] Sketch071
  ArcFitTolerance = 0
  AttachmentSupport = -> [Pad041]
  ExternalBSplineMaxDegree = 0
  ExternalBSplineTolerance = 0
  ExternalGeometry = -> [Import]
  FullyConstrained = true
  InternalTolerance = 1e-06
  InvalidShape = false
  MakeInternals = false
  MapMode = 5
  Placement = pos=(-3.62e-14,-56.7098,67.5841) rot=(1,0,0;0.698132rad)
  Support = -> [Pad041]
  TreeRank = 0
  ValidateShape = true
  sketch-geometry (2):
    g0: Circle CenterX=0 CenterY=-32.5627 CenterZ=0 NormalX=0 NormalY=0 NormalZ=1 AngleXU=0 Radius=13
    g1: LineSegment [constr] StartX=-1.96e-14 StartY=-55.0073 StartZ=0 EndX=1.98e-14 EndY=-10.1181 EndZ=0
  constraints (5):
    c: PointOnObject(g0,g-2)
    c: Diameter(g0) = 26
    c: PointOnObject(g1,g-4)
    c: Symmetric(g-3,g-3,g1)
    c: Symmetric(g1,g1,g0)
FEATURE [PartDesign::Pocket] Pocket031
  AddSubType = 1
  AutoTaperInnerAngle = false
  BaseFeature = -> Pad041
  CheckUpToFaceLimits = true
  ClaimChildren = false
  Direction = (1,1,1)
  Fit = 0
  FitJoin = 0
  InnerFit = 0
  InnerFitJoin = 0
  InvalidShape = false
  Length = 5
  Length2 = 100
  Linearize = true
  NewSolid = false
  Profile = -> Sketch071
  Refine = true
  Suppress = false
  TaperInnerAngle = 0
  TaperInnerAngleRev = 0
  TreeRank = 0
  Type = 1
  ValidateShape = true
  _ProfileBasedVersion = 1
  _Version = 1
FEATURE [PartDesign::Body] Body035  label="PlateTirette_3"
  AutoGroupSolids = false
  ClaimAllChildren = false
  ExportMode = 0
  Group = -> [Binder003,Pad041,Sketch071,Import,Pocket031]
  InvalidShape = false
  Origin = -> Origin054
  SingleSolid = true
  Tip = -> Pocket031
  TreeRank = 0
  ValidateShape = true
  _ExportChildren = -> [Pad041,Import,Pocket031]
  _GroupVersion = 1
FEATURE [App::Part] Part011  label="CoinTirette"
  ClaimAllChildren = false
  ExportMode = 1
  Group = -> [Link066,Body032,Body033,Body034,Body035]
  Origin = -> Origin049
  TreeRank = 0
  _ExportChildren = -> [Link066,Body032,Body033,Body034,Body035]
  _GroupVersion = 1
FEATURE [TechDraw::DrawSVGTemplate] Template002
  Height = 210
  Orientation = 1
  TreeRank = 0
  Width = 297
FEATURE [TechDraw::DrawProjGroupItem] ProjItem003  label="Front004"
  CoarseView = false
  Direction = (0,-0.643,0.766)
  Focus = 100
  HardHidden = false
  IsoCount = 0
  IsoHidden = false
  IsoVisible = false
  LockPosition = true
  Perspective = false
  Rotation = 0
  RotationVector = (-1,0,0)
  ScaleType = 2
  ScrubCount = 0
  SeamHidden = false
  SeamVisible = true
  SmoothHidden = false
  SmoothVisible = true
  Source = -> [Pad037]
  TreeRank = 0
  Type = 0
  X = 0
  XDirection = (-1,0,0)
  Y = 0
FEATURE [TechDraw::DrawProjGroup] ProjGroup003
  Anchor = -> ProjItem003
  AutoDistribute = true
  LockPosition = false
  ProjectionType = 0
  Rotation = 0
  ScaleType = 0
  Source = -> [Pad037]
  TreeRank = 0
  Views = -> [ProjItem003]
  X = 25.296
  Y = 185.829
  spacingX = 15
  spacingY = 15
FEATURE [TechDraw::DrawProjGroupItem] ProjItem004  label="Front005"
  CoarseView = false
  Direction = (0,-0.643,0.766)
  Focus = 100
  HardHidden = false
  IsoCount = 0
  IsoHidden = false
  IsoVisible = false
  LockPosition = true
  Perspective = false
  Rotation = 0
  RotationVector = (-1,0,0)
  ScaleType = 2
  ScrubCount = 0
  SeamHidden = false
  SeamVisible = true
  SmoothHidden = false
  SmoothVisible = true
  Source = -> [Pocket030]
  TreeRank = 0
  Type = 0
  X = 0
  XDirection = (-1,0,0)
  Y = 0
FEATURE [TechDraw::DrawProjGroup] ProjGroup004
  Anchor = -> ProjItem004
  AutoDistribute = true
  LockPosition = false
  ProjectionType = 0
  Rotation = 0
  ScaleType = 0
  Source = -> [Pocket030]
  TreeRank = 0
  Views = -> [ProjItem004]
  X = 74.5095
  Y = 185.806
  spacingX = 15
  spacingY = 15
FEATURE [TechDraw::DrawProjGroupItem] ProjItem006  label="Front007"
  CoarseView = false
  Direction = (0,-0.643,0.766)
  Focus = 100
  HardHidden = false
  IsoCount = 0
  IsoHidden = false
  IsoVisible = false
  LockPosition = true
  Perspective = false
  Rotation = 0
  RotationVector = (-1,0,0)
  ScaleType = 2
  ScrubCount = 0
  SeamHidden = false
  SeamVisible = true
  SmoothHidden = false
  SmoothVisible = true
  Source = -> [Pocket031]
  TreeRank = 0
  Type = 0
  X = 0
  XDirection = (-1,0,0)
  Y = 0
FEATURE [TechDraw::DrawProjGroup] ProjGroup006
  Anchor = -> ProjItem006
  AutoDistribute = true
  LockPosition = false
  ProjectionType = 0
  Rotation = 0
  ScaleType = 0
  Source = -> [Pocket031]
  TreeRank = 0
  Views = -> [ProjItem006]
  X = 123.484
  Y = 185.606
  spacingX = 15
  spacingY = 15
FEATURE [TechDraw::DrawPage] Page002  label="Laser3mmPlateTirette"
  KeepUpdated = true
  NextBalloonIndex = 1
  ProjectionType = 0
  Template = -> Template002
  TreeRank = 0
  Views = -> [ProjGroup003,ProjGroup004,ProjGroup006]
FEATURE [TechDraw::DrawSVGTemplate] Template003
  Height = 210
  Orientation = 1
  TreeRank = 0
  Width = 297
FEATURE [TechDraw::DrawProjGroupItem] ProjItem007  label="Front008"
  CoarseView = false
  Direction = (0,-0.643,0.766)
  Focus = 100
  HardHidden = false
  IsoCount = 0
  IsoHidden = false
  IsoVisible = false
  LockPosition = true
  Perspective = false
  Rotation = 0
  RotationVector = (-1,0,0)
  ScaleType = 2
  ScrubCount = 0
  SeamHidden = false
  SeamVisible = true
  SmoothHidden = false
  SmoothVisible = true
  Source = -> [Pad040]
  TreeRank = 0
  Type = 0
  X = 0
  XDirection = (-1,0,0)
  Y = 0
FEATURE [TechDraw::DrawProjGroup] ProjGroup007
  Anchor = -> ProjItem007
  AutoDistribute = true
  LockPosition = false
  ProjectionType = 0
  Rotation = 0
  ScaleType = 0
  Source = -> [Pad040]
  TreeRank = 0
  Views = -> [ProjItem007]
  X = 25.1312
  Y = 184.681
  spacingX = 15
  spacingY = 15
FEATURE [TechDraw::DrawPage] Page003  label="LaserPetg"
  KeepUpdated = true
  NextBalloonIndex = 1
  ProjectionType = 0
  Template = -> Template003
  TreeRank = 0
  Views = -> [ProjGroup007]
FEATURE [App::Link] Link067  label="Link067(CoinStandard)"
  AutoLinkLabel = true
  AutoPlacement = true
  LinkedObject = -> Body029
  SyncGroupVisibility = false
  TreeRank = 0
  _LinkVersion = 1
FEATURE [PartDesign::SubShapeBinder] Binder004  label="Binder004(Chamfer023)"
  BindCopyOnChange = 0
  BindMode = 0
  ClaimChildren = false
  Context = -> Part012 [Body036.Binder004.]
  EdgeTolerance = 1e-06
  FillStyle = 0
  Fuse = false
  InvalidShape = false
  MakeFace = true
  MergeEdges = true
  OffsetFill = false
  OffsetIntersection = false
  OffsetJoinType = 0
  OffsetOpenResult = false
  Outline = false
  PartialLoad = false
  Refine = true
  Relative = true
  SplitEdges = false
  Support = -> [Chamfer023[Face30]]
  TightBound = false
  TreeRank = 0
  ValidateShape = true
  _Version = 8
FEATURE [Sketcher::SketchObject] Sketch072
  ArcFitTolerance = 0
  AttachmentSupport = -> [Binder004]
  ExternalBSplineMaxDegree = 0
  ExternalBSplineTolerance = 0
  ExternalGeometry = -> [Binder004]
  FullyConstrained = true
  InternalTolerance = 1e-06
  InvalidShape = false
  MakeInternals = false
  MapMode = 5
  Placement = pos=(-2.82e-14,-50.4105,60.0769) rot=(1,0,0;0.698132rad)
  Support = -> [Binder004]
  TreeRank = 0
  ValidateShape = true
  sketch-geometry (2):
    g0: Circle CenterX=-14 CenterY=-14.7181 CenterZ=0 NormalX=0 NormalY=0 NormalZ=1 AngleXU=0 Radius=1.6
    g1: Circle CenterX=14 CenterY=-14.7181 CenterZ=0 NormalX=0 NormalY=0 NormalZ=1 AngleXU=0 Radius=1.6
  constraints (4):
    c: Coincident(g0,g-10)
    c: Coincident(g1,g-9)
    c: Diameter(g1) = 3.2
    c: Equal(g1,g0)
FEATURE [PartDesign::Pad] Pad042
  AddSubType = 0
  AutoTaperInnerAngle = false
  CheckUpToFaceLimits = true
  ClaimChildren = false
  Direction = (1,1,1)
  Fit = 0
  FitJoin = 0
  InnerFit = 0
  InnerFitJoin = 0
  InvalidShape = false
  Length = 3
  Length2 = 100
  Linearize = true
  NewSolid = false
  Profile = -> Sketch072
  Refine = true
  Suppress = false
  TaperInnerAngle = 0
  TaperInnerAngleRev = 0
  TreeRank = 0
  Type = 0
  ValidateShape = true
  _ProfileBasedVersion = 1
FEATURE [App::FeaturePython] WPProxy  # WARN: FeaturePython — macro-defined, semantics opaque (R4)
  Placement = pos=(-1.1e-15,-76.5169,42.0872) rot=(1,0,0;0.698132rad)
  TreeRank = 0
FEATURE [Part::Part2DObjectPython] ShapeString001  # Draft 2D object (typed FeaturePython)
  FontFile = <userpath>/Downloads/baveuse/baveuse.ttf
  InvalidShape = false
  Placement = pos=(-9,-91.52,42.09) rot=(1,0,0;0.698132rad)
  Size = 10
  String = K
  Tracking = 0
  TreeRank = 0
  ValidateShape = true
FEATURE [PartDesign::SubShapeBinder] Import001  label="Import001(ShapeString001)"
  BindCopyOnChange = 0
  BindMode = 0
  ClaimChildren = false
  Context = -> Part012 [Body036.Import001.]
  EdgeTolerance = 1e-06
  FillStyle = 0
  Fuse = false
  InvalidShape = false
  MakeFace = false
  MergeEdges = true
  OffsetFill = false
  OffsetIntersection = false
  OffsetJoinType = 0
  OffsetOpenResult = false
  Outline = false
  PartialLoad = false
  Refine = true
  Relative = true
  SplitEdges = false
  Support = -> [ShapeString001]
  TightBound = false
  TreeRank = 0
  ValidateShape = true
  _Version = 8
FEATURE [PartDesign::Pocket] Pocket032
  AddSubType = 1
  AutoTaperInnerAngle = false
  BaseFeature = -> Pad042
  CheckUpToFaceLimits = true
  ClaimChildren = false
  Direction = (1,1,1)
  Fit = 0
  FitJoin = 0
  InnerFit = 0
  InnerFitJoin = 0
  InvalidShape = false
  Length = 10
  Length2 = 100
  Linearize = true
  NewSolid = false
  Profile = -> Import001
  Refine = true
  Suppress = false
  TaperInnerAngle = 0
  TaperInnerAngleRev = 0
  TreeRank = 0
  Type = 0
  ValidateShape = true
  _ProfileBasedVersion = 1
  _Version = 1
FEATURE [PartDesign::Chamfer] Chamfer024
  AddSubType = 0
  Angle = 45
  Base = -> Pocket032 [Edge48,Edge49,Edge8,Edge5,Edge1,Edge2]
  BaseFeature = -> Pocket032
  ChamferType = 0
  FlipDirection = false
  InvalidShape = false
  NewSolid = false
  Refine = true
  Size = 0.4
  Size2 = 1
  SupportTransform = false
  Suppress = false
  TreeRank = 0
  UseAllEdges = false
  ValidateShape = true
FEATURE [PartDesign::Body] Body036  label="PlateLogo"
  AutoGroupSolids = false
  ClaimAllChildren = false
  ExportMode = 0
  Group = -> [Binder004,Sketch072,Pad042,ShapeString001,Import001,Pocket032,Chamfer024]
  InvalidShape = false
  Origin = -> Origin056
  SingleSolid = true
  Tip = -> Chamfer024
  TreeRank = 0
  ValidateShape = true
  _ExportChildren = -> [Binder004,Pad042,ShapeString001,Pocket032,Chamfer024]
  _GroupVersion = 1
FEATURE [PartDesign::FeatureBase] Clone001
  BaseFeature = -> Pad042
  InvalidShape = false
  NewSolid = false
  Suppress = false
  TreeRank = 10
  ValidateShape = true
FEATURE [Sketcher::SketchObject] Sketch073
  ArcFitTolerance = 0
  AttachmentSupport = -> [Clone001]
  ExternalBSplineMaxDegree = 0
  ExternalBSplineTolerance = 0
  ExternalGeometry = -> [Clone001]
  FullyConstrained = true
  InternalTolerance = 1e-06
  InvalidShape = false
  MakeInternals = false
  MapMode = 5
  Placement = pos=(-3.18e-14,-52.3388,62.375) rot=(1,0,0;0.698132rad)
  Support = -> [Clone001]
  TreeRank = 12
  ValidateShape = true
  sketch-geometry (1):
    g0: Circle CenterX=0 CenterY=-32.5673 CenterZ=0 NormalX=0 NormalY=0 NormalZ=1 AngleXU=0 Radius=7.5
  constraints (3):
    c: PointOnObject(g0,g-2)
    c: DistanceY(g-3,g0) = 22.44
    c: Diameter(g0) = 15
FEATURE [PartDesign::Pocket] Pocket033
  AddSubType = 1
  AutoTaperInnerAngle = false
  BaseFeature = -> Clone001
  CheckUpToFaceLimits = true
  ClaimChildren = false
  Direction = (1,1,1)
  Fit = 0
  FitJoin = 0
  InnerFit = 0
  InnerFitJoin = 0
  InvalidShape = false
  Length = 5
  Length2 = 100
  Linearize = true
  NewSolid = false
  Profile = -> Sketch073
  Refine = true
  Suppress = false
  TaperInnerAngle = 0
  TaperInnerAngleRev = 0
  TreeRank = 13
  Type = 1
  ValidateShape = true
  _ProfileBasedVersion = 1
  _Version = 1
FEATURE [PartDesign::Body] Body037  label="PlateInit"
  AutoGroupSolids = false
  BaseFeature = -> Pad042
  ClaimAllChildren = false
  ExportMode = 0
  Group = -> [Clone001,Sketch073,Pocket033]
  InvalidShape = false
  Origin = -> Origin057
  SingleSolid = true
  Tip = -> Pocket033
  TreeRank = 11
  ValidateShape = true
  _ExportChildren = -> [Clone001,Pocket033]
  _GroupVersion = 1
FEATURE [App::Part] Part012  label="CoinLogo"
  ClaimAllChildren = false
  ExportMode = 1
  Group = -> [Link067,Body036,WPProxy,ShapeString001,Body037]
  Origin = -> Origin055
  TreeRank = 0
  _ExportChildren = -> [Link067,Body036,WPProxy,ShapeString001,Body037]
  _GroupVersion = 1
FEATURE [TechDraw::DrawSVGTemplate] Template004
  Height = 210
  Orientation = 1
  TreeRank = 15
  Width = 297
FEATURE [TechDraw::DrawProjGroupItem] ProjItem008  label="Front009"
  CoarseView = false
  Direction = (0,-0.643,0.766)
  Focus = 100
  HardHidden = false
  IsoCount = 0
  IsoHidden = false
  IsoVisible = false
  LockPosition = true
  Perspective = false
  Rotation = 0
  RotationVector = (-1,0,0)
  ScaleType = 2
  ScrubCount = 0
  SeamHidden = false
  SeamVisible = true
  SmoothHidden = false
  SmoothVisible = true
  Source = -> [Pocket033]
  TreeRank = 18
  Type = 0
  X = 0
  XDirection = (-1,0,0)
  Y = 0
FEATURE [TechDraw::DrawProjGroup] ProjGroup008
  Anchor = -> ProjItem008
  AutoDistribute = true
  LockPosition = false
  ProjectionType = 0
  Rotation = 0
  ScaleType = 0
  Source = -> [Pocket033]
  TreeRank = 19
  Views = -> [ProjItem008]
  X = 24.3999
  Y = 186.325
  spacingX = 15
  spacingY = 15
FEATURE [TechDraw::DrawPage] Page004  label="Laser3mmPlateInit"
  KeepUpdated = true
  NextBalloonIndex = 1
  ProjectionType = 0
  Template = -> Template004
  TreeRank = 16
  Views = -> [ProjGroup008]
FEATURE [TechDraw::DrawSVGTemplate] Template005
  Height = 210
  Orientation = 1
  TreeRank = 21
  Width = 297
FEATURE [TechDraw::DrawProjGroupItem] ProjItem009  label="Front010"
  CoarseView = false
  Direction = (0,0,1)
  Focus = 100
  HardHidden = false
  IsoCount = 0
  IsoHidden = false
  IsoVisible = false
  LockPosition = true
  Perspective = false
  Rotation = 0
  RotationVector = (0,1,0)
  ScaleType = 2
  ScrubCount = 0
  SeamHidden = false
  SeamVisible = true
  SmoothHidden = false
  SmoothVisible = true
  Source = -> [Fillet013]
  TreeRank = 24
  Type = 0
  X = 0
  XDirection = (0,1,0)
  Y = 0
FEATURE [TechDraw::DrawProjGroup] ProjGroup009
  Anchor = -> ProjItem009
  AutoDistribute = true
  LockPosition = false
  ProjectionType = 0
  Rotation = 0
  ScaleType = 0
  Source = -> [Fillet013]
  TreeRank = 23
  Views = -> [ProjItem009]
  X = 49.3207
  Y = 152.885
  spacingX = 15
  spacingY = 15
FEATURE [TechDraw::DrawPage] Page005  label="Laser5mmCaleCentrale"
  KeepUpdated = true
  NextBalloonIndex = 1
  ProjectionType = 0
  Template = -> Template005
  TreeRank = 26
  Views = -> [ProjGroup009]
FEATURE [App::Link] Link068  label="Link068(633ZZ)"
  AutoLinkLabel = true
  AutoPlacement = true
  LinkPlacement = pos=(-123.877,-2.56104,0) rot=(0,0,1;0rad)
  LinkedObject = -> <external generic-hardware.FCStd>#Part035
  Placement = pos=(-123.877,-2.56104,0) rot=(0,0,1;0rad)
  SyncGroupVisibility = false
  TreeRank = 27
  _LinkVersion = 1
FEATURE [App::Link] Link069  label="Link069(*633ZZ)"
  AutoLinkLabel = true
  AutoPlacement = true
  LinkPlacement = pos=(59.7205,108.561,0) rot=(0,0,1;0rad)
  LinkedObject = -> Link068
  Placement = pos=(59.7205,108.561,0) rot=(0,0,1;0rad)
  SyncGroupVisibility = false
  TreeRank = 28
  _LinkVersion = 1
FEATURE [App::Link] Link070  label="Link070(*633ZZ)"
  AutoLinkLabel = true
  AutoPlacement = true
  LinkPlacement = pos=(123.877,-2.56104,0) rot=(0,0,1;0rad)
  LinkedObject = -> Link068
  Placement = pos=(123.877,-2.56104,0) rot=(0,0,1;0rad)
  SyncGroupVisibility = false
  TreeRank = 29
  _LinkVersion = 1
FEATURE [App::Link] Link071  label="Link071(*633ZZ)"
  AutoLinkLabel = true
  AutoPlacement = true
  LinkPlacement = pos=(-59.7205,108.561,0) rot=(0,0,1;0rad)
  LinkedObject = -> Link068
  Placement = pos=(-59.7205,108.561,0) rot=(0,0,1;0rad)
  SyncGroupVisibility = false
  TreeRank = 30
  _LinkVersion = 1
FEATURE [App::Link] Link072  label="Link072(*633ZZ)"
  AutoLinkLabel = true
  AutoPlacement = true
  LinkPlacement = pos=(64.1564,-106,0) rot=(0,0,1;0rad)
  LinkedObject = -> Link068
  Placement = pos=(64.1564,-106,0) rot=(0,0,1;0rad)
  SyncGroupVisibility = false
  TreeRank = 31
  _LinkVersion = 1
FEATURE [App::Link] Link073  label="Link073(*633ZZ)"
  AutoLinkLabel = true
  AutoPlacement = true
  LinkPlacement = pos=(-64.1564,-106,0) rot=(0,0,1;0rad)
  LinkedObject = -> Link068
  Placement = pos=(-64.1564,-106,0) rot=(0,0,1;0rad)
  SyncGroupVisibility = false
  TreeRank = 32
  _LinkVersion = 1
FEATURE [App::DocumentObjectGroup] Group003  label="Roulement"
  ClaimAllChildren = true
  ExportMode = 1
  Group = -> [Link068,Link069,Link070,Link071,Link072,Link073]
  TreeRank = 33
  _GroupVersion = 1
FEATURE [Part::FeaturePython] Screw004  label="M3x16-Screw"  # Fasteners workbench fastener (typed FeaturePython)
  InvalidShape = false
  Placement = pos=(59.7205,108.561,-5) rot=(-1,0,0;3.14159rad)
  TreeRank = 40
  ValidateShape = true
  baseObject = -> Body019 [?Edge333]
  diameter = 1
  invert = true
  leftHanded = false
  length = 5
  lengthCustom = 16
  matchOuter = false
  offset = 0
  thread = false
  type = 40
FEATURE [Part::FeaturePython] Screw005  label="M3x16-Screw041"  # Fasteners workbench fastener (typed FeaturePython)
  InvalidShape = false
  Placement = pos=(-59.7205,108.561,-5) rot=(-1,0,0;3.14159rad)
  TreeRank = 41
  ValidateShape = true
  baseObject = -> Body019 [?Edge297]
  diameter = 1
  invert = true
  leftHanded = false
  length = 5
  lengthCustom = 16
  matchOuter = false
  offset = 0
  thread = false
  type = 40
FEATURE [Part::FeaturePython] Screw006  label="M3x16-Screw042"  # Fasteners workbench fastener (typed FeaturePython)
  InvalidShape = false
  Placement = pos=(-123.877,-2.56104,-5) rot=(-1,0,0;3.14159rad)
  TreeRank = 42
  ValidateShape = true
  baseObject = -> Body019 [?Edge243]
  diameter = 1
  invert = true
  leftHanded = false
  length = 5
  lengthCustom = 16
  matchOuter = false
  offset = 0
  thread = false
  type = 40
FEATURE [Part::FeaturePython] Screw007  label="M3x16-Screw043"  # Fasteners workbench fastener (typed FeaturePython)
  InvalidShape = false
  Placement = pos=(-64.1564,-106,-5) rot=(-1,0,0;3.14159rad)
  TreeRank = 43
  ValidateShape = true
  baseObject = -> Body019 [?Edge209]
  diameter = 1
  invert = true
  leftHanded = false
  length = 5
  lengthCustom = 16
  matchOuter = false
  offset = 0
  thread = false
  type = 40
FEATURE [Part::FeaturePython] Screw008  label="M3x16-Screw044"  # Fasteners workbench fastener (typed FeaturePython)
  InvalidShape = false
  Placement = pos=(64.1564,-106,-5) rot=(-1,0,0;3.14159rad)
  TreeRank = 44
  ValidateShape = true
  baseObject = -> Body019 [?Edge251]
  diameter = 1
  invert = true
  leftHanded = false
  length = 5
  lengthCustom = 16
  matchOuter = false
  offset = 0
  thread = false
  type = 40
FEATURE [Part::FeaturePython] Screw009  label="M3x16-Screw045"  # Fasteners workbench fastener (typed FeaturePython)
  InvalidShape = false
  Placement = pos=(123.877,-2.56104,-5) rot=(-1,0,0;3.14159rad)
  TreeRank = 45
  ValidateShape = true
  baseObject = -> Body019 [?Edge285]
  diameter = 1
  invert = true
  leftHanded = false
  length = 5
  lengthCustom = 16
  matchOuter = false
  offset = 0
  thread = false
  type = 40
FEATURE [Part::FeaturePython] Nut  label="M3-Nut"  # Fasteners workbench fastener (typed FeaturePython)
  InvalidShape = false
  Placement = pos=(123.877,-2.56104,5) rot=(0,0,1;0rad)
  TreeRank = 59
  ValidateShape = true
  baseObject = -> Body019 [?Edge87]
  diameter = 1
  invert = false
  leftHanded = false
  matchOuter = false
  offset = 5
  thread = false
  type = 5
FEATURE [Part::FeaturePython] Nut001  label="M3-Nut051"  # Fasteners workbench fastener (typed FeaturePython)
  InvalidShape = false
  Placement = pos=(64.1564,-106,5) rot=(0,0,1;0rad)
  TreeRank = 60
  ValidateShape = true
  baseObject = -> Body019 [?Edge70]
  diameter = 1
  invert = false
  leftHanded = false
  matchOuter = false
  offset = 5
  thread = false
  type = 5
FEATURE [Part::FeaturePython] Nut002  label="M3-Nut052"  # Fasteners workbench fastener (typed FeaturePython)
  InvalidShape = false
  Placement = pos=(-64.1564,-106,5) rot=(0,0,1;0rad)
  TreeRank = 61
  ValidateShape = true
  baseObject = -> Body019 [?Edge49]
  diameter = 1
  invert = false
  leftHanded = false
  matchOuter = false
  offset = 5
  thread = false
  type = 5
FEATURE [Part::FeaturePython] Nut003  label="M3-Nut053"  # Fasteners workbench fastener (typed FeaturePython)
  InvalidShape = false
  Placement = pos=(-123.877,-2.56104,5) rot=(0,0,1;0rad)
  TreeRank = 62
  ValidateShape = true
  baseObject = -> Body019 [?Edge66]
  diameter = 1
  invert = false
  leftHanded = false
  matchOuter = false
  offset = 5
  thread = false
  type = 5
FEATURE [Part::FeaturePython] Nut004  label="M3-Nut054"  # Fasteners workbench fastener (typed FeaturePython)
  InvalidShape = false
  Placement = pos=(-59.7205,108.561,5) rot=(0,0,1;0rad)
  TreeRank = 63
  ValidateShape = true
  baseObject = -> Body019 [?Edge93]
  diameter = 1
  invert = false
  leftHanded = false
  matchOuter = false
  offset = 5
  thread = false
  type = 5
FEATURE [Part::FeaturePython] Nut005  label="M3-Nut055"  # Fasteners workbench fastener (typed FeaturePython)
  InvalidShape = false
  Placement = pos=(59.7205,108.561,5) rot=(0,0,1;0rad)
  TreeRank = 64
  ValidateShape = true
  baseObject = -> Body019 [?Edge111]
  diameter = 1
  invert = false
  leftHanded = false
  matchOuter = false
  offset = 5
  thread = false
  type = 5
FEATURE [App::DocumentObjectGroup] Group004  label="Visserie001"
  ClaimAllChildren = true
  ExportMode = 1
  Group = -> [Screw004,Screw005,Screw006,Screw007,Screw008,Screw009,Nut,Nut001,Nut002,Nut003,Nut004,Nut005]
  TreeRank = 46
  _GroupVersion = 1
FEATURE [App::Link] Link074  label="Link074(BAU-2195813)"
  AutoLinkLabel = true
  AutoPlacement = true
  LinkPlacement = pos=(-3.01e-14,-76.5631,42.1127) rot=(1,0,0;0.696386rad)
  LinkedObject = -> <external generic-hardware.FCStd>#Part036
  Placement = pos=(-3.01e-14,-76.5631,42.1127) rot=(1,0,0;0.696386rad)
  SyncGroupVisibility = false
  TreeRank = 65
  _LinkVersion = 1
FEATURE [App::Part] Part010  label="CoinBAU"
  ClaimAllChildren = false
  ExportMode = 1
  Group = -> [Link065,Body030,Link074]
  Origin = -> Origin047
  TreeRank = 0
  _ExportChildren = -> [Link065,Body030,Link074]
  _GroupVersion = 1
FEATURE [TechDraw::DrawSVGTemplate] Template006
  Height = 210
  Orientation = 1
  TreeRank = 68
  Width = 297
FEATURE [TechDraw::DrawSVGTemplate] Template007
  Height = 210
  Orientation = 1
  TreeRank = 80
  Width = 297
FEATURE [TechDraw::DrawProjGroupItem] ProjItem011  label="Front012"
  CoarseView = false
  Direction = (0,0,1)
  Focus = 100
  HardHidden = false
  IsoCount = 0
  IsoHidden = false
  IsoVisible = false
  LockPosition = true
  Perspective = false
  Rotation = 0
  RotationVector = (0,1,0)
  ScaleType = 2
  ScrubCount = 0
  SeamHidden = false
  SeamVisible = true
  SmoothHidden = false
  SmoothVisible = true
  Source = -> [Fillet011]
  TreeRank = 83
  Type = 0
  X = 0
  XDirection = (0,1,0)
  Y = 0
FEATURE [TechDraw::DrawProjGroup] ProjGroup011
  Anchor = -> ProjItem011
  AutoDistribute = true
  LockPosition = false
  ProjectionType = 0
  Rotation = 0
  ScaleType = 0
  Source = -> [Fillet011]
  TreeRank = 84
  Views = -> [ProjItem011]
  X = 148.5
  Y = 105
  spacingX = 15
  spacingY = 15
FEATURE [TechDraw::DrawPage] Page007  label="Laser5mmSemelle"
  KeepUpdated = true
  NextBalloonIndex = 1
  ProjectionType = 0
  Template = -> Template007
  TreeRank = 81
  Views = -> [ProjGroup011]
FEATURE [App::Link] Link075  label="Link075(Semelle)"
  AutoLinkLabel = true
  AutoPlacement = true
  LinkedObject = -> Body019
  ShowElement = false
  SyncGroupVisibility = false
  TreeRank = 94
  _LinkVersion = 1
FEATURE [Sketcher::SketchObject] Sketch074
  ArcFitTolerance = 1e-06
  AttachmentSupport = -> [XY_Plane047]
  ExternalBSplineMaxDegree = 5
  ExternalBSplineTolerance = 0.0001
  FullyConstrained = true
  InternalTolerance = 1e-06
  InvalidShape = false
  MakeInternals = true
  MapMode = 5
  Support = -> [XY_Plane047]
  TreeRank = 105
  ValidateShape = true
  sketch-geometry (1):
    g0: Circle CenterX=0 CenterY=0 CenterZ=0 NormalX=0 NormalY=0 NormalZ=1 AngleXU=0 Radius=10
  constraints (2):
    c: Coincident(g0,g-1)
    c: Diameter(g0) = 20
FEATURE [PartDesign::Pad] Pad043
  AddSubType = 0
  AlongSketchNormal = false
  AutoTaperInnerAngle = true
  CheckUpToFaceLimits = true
  ClaimChildren = false
  Direction = (0,0,1)
  Fit = 0
  FitJoin = 0
  InnerFit = 0
  InnerFitJoin = 0
  InvalidShape = false
  Length = 4
  Length2 = 100
  Linearize = true
  NewSolid = false
  Profile = -> Sketch074
  Refine = true
  Suppress = false
  TaperAngle = 10
  TaperInnerAngle = -10
  TaperInnerAngleRev = 0
  TreeRank = 106
  Type = 0
  ValidateShape = true
  _ProfileBasedVersion = 1
FEATURE [PartDesign::Pad] Pad044
  AddSubType = 0
  AlongSketchNormal = false
  AutoTaperInnerAngle = true
  BaseFeature = -> Pad043
  CheckUpToFaceLimits = true
  ClaimChildren = false
  Direction = (0,0,1)
  Fit = 0
  FitJoin = 0
  InnerFit = 0
  InnerFitJoin = 0
  InvalidShape = false
  Length = 2
  Length2 = 100
  Linearize = true
  NewSolid = false
  Profile = -> Pad043 [Face3]
  Refine = true
  Suppress = false
  TaperInnerAngle = 0
  TaperInnerAngleRev = 0
  TreeRank = 107
  Type = 0
  ValidateShape = true
  _ProfileBasedVersion = 1
FEATURE [Sketcher::SketchObject] Sketch075
  ArcFitTolerance = 1e-06
  AttachmentSupport = -> [Pad044]
  ExternalBSplineMaxDegree = 5
  ExternalBSplineTolerance = 0.0001
  FullyConstrained = true
  InternalTolerance = 1e-06
  InvalidShape = false
  MakeInternals = true
  MapMode = 5
  Placement = pos=(0,0,6) rot=(0,0,1;0rad)
  Support = -> [Pad044]
  TreeRank = 108
  ValidateShape = true
  sketch-geometry (1):
    g0: Circle CenterX=0 CenterY=0 CenterZ=0 NormalX=0 NormalY=0 NormalZ=1 AngleXU=0 Radius=35
  constraints (2):
    c: Coincident(g0,g-1)
    c: Diameter(g0) = 70
FEATURE [PartDesign::Pad] Pad045
  AddSubType = 0
  AlongSketchNormal = false
  AutoTaperInnerAngle = true
  BaseFeature = -> Pad044
  CheckUpToFaceLimits = true
  ClaimChildren = false
  Direction = (0,0,1)
  Fit = 0
  FitJoin = 0
  InnerFit = 0
  InnerFitJoin = 0
  InvalidShape = false
  Length = 15
  Length2 = 100
  Linearize = true
  NewSolid = false
  Profile = -> Sketch075
  Refine = true
  Suppress = false
  TaperAngle = 10
  TaperInnerAngle = -10
  TaperInnerAngleRev = 0
  TreeRank = 109
  Type = 0
  ValidateShape = true
  _ProfileBasedVersion = 1
FEATURE [Part::SubShapeBinder] Import002  label="Import002(Fillet011)"
  BindCopyOnChange = 0
  BindMode = 0
  ClaimChildren = false
  Context = -> Group002 [Body038.Import002.]
  EdgeTolerance = 1e-06
  FillStyle = 0
  Fuse = false
  InvalidShape = false
  MakeFace = false
  MergeEdges = true
  OffsetFill = false
  OffsetIntersection = false
  OffsetJoinType = 0
  OffsetOpenResult = false
  Outline = false
  PartialLoad = false
  Relative = true
  SplitEdges = false
  Support = -> [Link075[Fillet011.]]
  TightBound = false
  TreeRank = 110
  ValidateShape = true
  _Version = 8
FEATURE [Sketcher::SketchObject] Sketch076
  ArcFitTolerance = 1e-06
  AttachmentSupport = -> [YZ_Plane047]
  ExternalBSplineMaxDegree = 5
  ExternalBSplineTolerance = 0.0001
  ExternalGeometry = -> [Pad045]
  FullyConstrained = true
  InternalTolerance = 1e-06
  InvalidShape = false
  MakeInternals = true
  MapMode = 5
  Placement = pos=(0,0,0) rot=(0.57735,0.57735,0.57735;2.0944rad)
  Support = -> [YZ_Plane047]
  TreeRank = 111
  ValidateShape = true
  sketch-geometry (5):
    g0: LineSegment StartX=21 StartY=6 StartZ=0 EndX=29 EndY=6 EndZ=0
    g1: LineSegment StartX=29 StartY=6 StartZ=0 EndX=29 EndY=10 EndZ=0
    g2: LineSegment StartX=29 StartY=10 StartZ=0 EndX=21 EndY=10 EndZ=0
    g3: LineSegment StartX=21 StartY=10 StartZ=0 EndX=21 EndY=6 EndZ=0
    g4: LineSegment [constr] StartX=25 StartY=6 StartZ=0 EndX=25 EndY=10 EndZ=0
  constraints (15):
    c: Coincident(g0,g1)
    c: Coincident(g1,g2)
    c: Coincident(g2,g3)
    c: Coincident(g3,g0)
    c: Horizontal(g0)
    c: Horizontal(g2)
    c: Vertical(g1)
    c: Vertical(g3)
    c: PointOnObject(g4,g2)
    c: Vertical(g4)
    c: Symmetric(g0,g0,g4)
    c: DistanceX(g4) = 25
    c: DistanceX(g0,g0) = 8
    c: PointOnObject(g0,g-3)
    c: DistanceY(g1,g1) = 4
FEATURE [PartDesign::Groove] Groove
  AddSubType = 1
  Angle = 360
  Axis = (-2e-16,3e-16,1)
  Base = (0,0,0)
  BaseFeature = -> Pad045
  ClaimChildren = false
  Fit = 0
  FitJoin = 0
  InnerFit = 0
  InnerFitJoin = 0
  InvalidShape = false
  Linearize = true
  NewSolid = false
  Profile = -> Sketch076
  ReferenceAxis = -> Sketch076 [V_Axis]
  Refine = true
  Suppress = false
  TreeRank = 112
  ValidateShape = true
  _ProfileBasedVersion = 1
FEATURE [Sketcher::SketchObject] Sketch077
  ArcFitTolerance = 1e-06
  AttachmentSupport = -> [Groove]
  ExternalBSplineMaxDegree = 5
  ExternalBSplineTolerance = 0.0001
  FullyConstrained = true
  InternalTolerance = 1e-06
  InvalidShape = false
  MakeInternals = true
  MapMode = 5
  Placement = pos=(0,0,21) rot=(0,0,1;0rad)
  Support = -> [Groove]
  TreeRank = 113
  ValidateShape = true
  sketch-geometry (7):
    g0: Circle CenterX=-4.7166e-12 CenterY=11.3561 CenterZ=0 NormalX=0 NormalY=0 NormalZ=1 AngleXU=0 Radius=2.2
    g1: Circle CenterX=9.83464 CenterY=-5.67803 CenterZ=0 NormalX=0 NormalY=0 NormalZ=1 AngleXU=0 Radius=2.2
    g2: Circle CenterX=-9.83464 CenterY=-5.67803 CenterZ=0 NormalX=0 NormalY=0 NormalZ=1 AngleXU=0 Radius=2.2
    g3: Circle [constr] CenterX=7.482e-13 CenterY=1.30938e-11 CenterZ=0 NormalX=0 NormalY=0 NormalZ=1 AngleXU=0 Radius=11.3561
    g4: LineSegment [constr] StartX=-9.83464 StartY=-5.67803 StartZ=0 EndX=7.478e-13 EndY=1.30935e-11 EndZ=0
    g5: LineSegment [constr] StartX=7.482e-13 StartY=1.30938e-11 StartZ=0 EndX=9.83464 EndY=-5.67803 EndZ=0
    g6: LineSegment [constr] StartX=7.482e-13 StartY=1.30938e-11 StartZ=0 EndX=-4.7166e-12 EndY=11.3561 EndZ=0
  constraints (16):
    c: PointOnObject(g0,g-2)
    c: Coincident(g3,g-1)
    c: PointOnObject(g0,g3)
    c: PointOnObject(g1,g3)
    c: PointOnObject(g2,g3)
    c: Equal(g2,g1)
    c: Equal(g1,g0)
    c: Coincident(g4,g2)
    c: Coincident(g4,g3)
    c: Coincident(g5,g3)
    c: Coincident(g5,g1)
    c: Coincident(g6,g3)
    c: Coincident(g6,g0)
    c: Angle(g5,g6) = 2.0944
    c: Symmetric(g2,g1,g-2)
    c: Diameter(g1) = 4.4
FEATURE [PartDesign::Pocket] Pocket034
  AddSubType = 1
  AutoTaperInnerAngle = true
  BaseFeature = -> Groove
  CheckUpToFaceLimits = true
  ClaimChildren = false
  Direction = (1,1,1)
  Fit = 0
  FitJoin = 0
  InnerFit = 0
  InnerFitJoin = 0
  InvalidShape = false
  Length = 10
  Length2 = 100
  Linearize = true
  NewSolid = false
  Profile = -> Sketch077
  Refine = true
  Suppress = false
  TaperInnerAngle = 0
  TaperInnerAngleRev = 0
  TreeRank = 114
  Type = 0
  ValidateShape = true
  _ProfileBasedVersion = 1
  _Version = 1
FEATURE [PartDesign::Fillet] Fillet023
  AddSubType = 0
  Base = -> Pocket034 [Edge3]
  BaseFeature = -> Pocket034
  InvalidShape = false
  NewSolid = false
  Radius = 14
  Refine = true
  SupportTransform = false
  Suppress = false
  TreeRank = 115
  UseAllEdges = false
  ValidateShape = true
FEATURE [PartDesign::Chamfer] Chamfer025
  AddSubType = 0
  Angle = 45
  Base = -> Fillet023 [Edge3]
  BaseFeature = -> Fillet023
  ChamferType = 0
  FlipDirection = false
  InvalidShape = false
  NewSolid = false
  Refine = true
  Size = 2
  Size2 = 1
  SupportTransform = false
  Suppress = false
  TreeRank = 116
  UseAllEdges = false
  ValidateShape = true
FEATURE [PartDesign::Fillet] Fillet024
  AddSubType = 0
  Base = -> Chamfer025 [Edge13,Edge11]
  BaseFeature = -> Chamfer025
  InvalidShape = false
  NewSolid = false
  Radius = 2
  Refine = true
  SupportTransform = false
  Suppress = false
  TreeRank = 117
  UseAllEdges = false
  ValidateShape = true
FEATURE [PartDesign::Chamfer] Chamfer026
  AddSubType = 0
  Angle = 45
  Base = -> Fillet024 [Edge18,Edge3,Edge15]
  BaseFeature = -> Fillet024
  ChamferType = 0
  FlipDirection = false
  InvalidShape = false
  NewSolid = false
  Refine = true
  Size = 1
  Size2 = 1
  SupportTransform = false
  Suppress = false
  TreeRank = 118
  UseAllEdges = false
  ValidateShape = true
FEATURE [PartDesign::SubShapeBinder] Binder005  label="Binder005(Chamfer026)"
  BindCopyOnChange = 0
  BindMode = 0
  ClaimChildren = false
  Context = -> Group002 [Part013.Body039.Binder005.]
  EdgeTolerance = 1e-06
  FillStyle = 0
  Fuse = false
  InvalidShape = false
  MakeFace = true
  MergeEdges = true
  OffsetFill = false
  OffsetIntersection = false
  OffsetJoinType = 0
  OffsetOpenResult = false
  Outline = false
  PartialLoad = false
  Relative = true
  SplitEdges = false
  Support = -> [Body038[Chamfer026.Face17]]
  TightBound = false
  TreeRank = 133
  ValidateShape = true
  _Version = 8
FEATURE [Sketcher::SketchObject] Sketch078
  ArcFitTolerance = 1e-06
  AttachmentSupport = -> [Binder005]
  ExternalBSplineMaxDegree = 5
  ExternalBSplineTolerance = 0.0001
  FullyConstrained = true
  InternalTolerance = 1e-06
  InvalidShape = false
  MakeInternals = true
  MapMode = 5
  Placement = pos=(0,0,21) rot=(0,0,1;0rad)
  Support = -> [Binder005]
  TreeRank = 134
  ValidateShape = true
  sketch-geometry (12):
    g0: Circle CenterX=2.0355e-12 CenterY=-3.998e-13 CenterZ=0 NormalX=0 NormalY=0 NormalZ=1 AngleXU=0 Radius=85
    g1: Circle CenterX=2.0355e-12 CenterY=11.355 CenterZ=0 NormalX=0 NormalY=0 NormalZ=1 AngleXU=0 Radius=1.6
    g2: Circle CenterX=9.83372 CenterY=-5.6775 CenterZ=0 NormalX=0 NormalY=0 NormalZ=1 AngleXU=0 Radius=1.6
    g3: Circle CenterX=-9.83372 CenterY=-5.6775 CenterZ=0 NormalX=0 NormalY=0 NormalZ=1 AngleXU=0 Radius=1.6
    g4: Circle [constr] CenterX=2.0355e-12 CenterY=-3.998e-13 CenterZ=0 NormalX=0 NormalY=0 NormalZ=1 AngleXU=0 Radius=11.355
    g5: LineSegment [constr] StartX=2.0355e-12 StartY=11.355 StartZ=0 EndX=2.0355e-12 EndY=-3.997e-13 EndZ=0
    g6: LineSegment [constr] StartX=2.0355e-12 StartY=-3.998e-13 StartZ=0 EndX=-9.83372 EndY=-5.6775 EndZ=0
    g7: LineSegment [constr] StartX=2.0355e-12 StartY=-3.998e-13 StartZ=0 EndX=9.83372 EndY=-5.6775 EndZ=0
    g8: Circle CenterX=-3.78e-14 CenterY=60 CenterZ=0 NormalX=0 NormalY=0 NormalZ=1 AngleXU=0 Radius=1.6
    g9: Circle [constr] CenterX=2.0355e-12 CenterY=-3.998e-13 CenterZ=0 NormalX=0 NormalY=0 NormalZ=1 AngleXU=0 Radius=60
    g10: Circle CenterX=51.9615 CenterY=-30 CenterZ=0 NormalX=0 NormalY=0 NormalZ=1 AngleXU=0 Radius=1.6
    g11: Circle CenterX=-51.9615 CenterY=-30 CenterZ=0 NormalX=0 NormalY=0 NormalZ=1 AngleXU=0 Radius=1.6
  constraints (29):
    c: Coincident(g0,g-1)
    c: Diameter(g0) = 170
    c: Equal(g3,g2)
    c: Equal(g3,g1)
    c: Diameter(g3) = 3.2
    c: Coincident(g4,g0)
    c: PointOnObject(g1,g4)
    c: Diameter(g4) = 22.71
    c: Coincident(g5,g1)
    c: Coincident(g5,g0)
    c: Vertical(g5)
    c: Coincident(g6,g0)
    c: Coincident(g6,g3)
    c: Coincident(g7,g0)
    c: Coincident(g7,g2)
    c: Angle(g7,g5) = 2.0944
    c: Symmetric(g3,g2,g-2)
    c: PointOnObject(g2,g4)
    c: PointOnObject(g8,g-2)
    c: DistanceY(g8) = 60
    c: Equal(g8,g1)
    c: Coincident(g9,g0)
    c: PointOnObject(g8,g9)
    c: PointOnObject(g10,g9)
    c: PointOnObject(g11,g9)
    c: Equal(g11,g10)
    c: Equal(g10,g8)
    c: PointOnObject(g10,g7)
    c: PointOnObject(g11,g6)
FEATURE [PartDesign::Pad] Pad046
  AddSubType = 0
  AlongSketchNormal = false
  AutoTaperInnerAngle = true
  CheckUpToFaceLimits = true
  ClaimChildren = false
  Direction = (0,0,1)
  Fit = 0
  FitJoin = 0
  InnerFit = 0
  InnerFitJoin = 0
  InvalidShape = false
  Length = 3
  Length2 = 100
  Linearize = true
  NewSolid = false
  Profile = -> Sketch078
  Refine = true
  Suppress = false
  TaperInnerAngle = 0
  TaperInnerAngleRev = 0
  TreeRank = 135
  Type = 0
  ValidateShape = true
  _ProfileBasedVersion = 1
FEATURE [Sketcher::SketchObject] Sketch079
  ArcFitTolerance = 1e-06
  AttachmentSupport = -> [Chamfer026]
  ExternalBSplineMaxDegree = 5
  ExternalBSplineTolerance = 0.0001
  FullyConstrained = false
  InternalTolerance = 1e-06
  InvalidShape = false
  MakeInternals = true
  MapMode = 5
  Placement = pos=(0,0,21) rot=(0,0,1;0rad)
  Support = -> [Chamfer026]
  TreeRank = 136
  ValidateShape = true
  sketch-geometry (4):
    g0: ArcOfCircle CenterX=1.25182e-10 CenterY=4.9383e-12 CenterZ=0 NormalX=0 NormalY=0 NormalZ=1 AngleXU=0 Radius=34.3525 StartAngle=1.11893 EndAngle=2.02267
    g1: ArcOfCircle CenterX=1.25182e-10 CenterY=4.9383e-12 CenterZ=0 NormalX=0 NormalY=0 NormalZ=1 AngleXU=0 Radius=82.5 StartAngle=1.51015 EndAngle=1.63144
    g2: LineSegment StartX=-15 StartY=30.9046 StartZ=0 EndX=-5 EndY=82.3483 EndZ=0
    g3: LineSegment StartX=5 StartY=82.3483 StartZ=0 EndX=15 EndY=30.9046 EndZ=0
  constraints (11):
    c: Coincident(g0,g-1)
    c: Coincident(g1,g0)
    c: Symmetric(g1,g1,g-2)
    c: Symmetric(g0,g0,g-2)
    c: Coincident(g2,g0)
    c: Coincident(g2,g1)
    c: Coincident(g3,g1)
    c: Coincident(g3,g0)
    c: Diameter(g1) = 165
    c: DistanceX(g1,g1) = 10
    c: DistanceX(g0,g0) = 30
FEATURE [PartDesign::Pad] Pad047
  AddSubType = 0
  AlongSketchNormal = false
  AutoTaperInnerAngle = true
  BaseFeature = -> Chamfer026
  CheckUpToFaceLimits = true
  ClaimChildren = false
  Direction = (0,0,1)
  Fit = 0
  FitJoin = 0
  InnerFit = 0
  InnerFitJoin = 0
  InvalidShape = false
  Length = 10
  Length2 = 100
  Linearize = true
  NewSolid = false
  Profile = -> Sketch079
  Refine = true
  Reversed = true
  Suppress = false
  TaperInnerAngle = 0
  TaperInnerAngleRev = 0
  TreeRank = 137
  Type = 0
  ValidateShape = true
  _ProfileBasedVersion = 1
FEATURE [PartDesign::Chamfer] Chamfer027
  AddSubType = 0
  Angle = 45
  Base = -> Pad047 [Edge37]
  BaseFeature = -> Pad047
  ChamferType = 1
  FlipDirection = false
  InvalidShape = false
  NewSolid = false
  Refine = true
  Size = 40
  Size2 = 8
  SupportTransform = false
  Suppress = false
  TreeRank = 138
  UseAllEdges = false
  ValidateShape = true
FEATURE [PartDesign::Fillet] Fillet025
  AddSubType = 0
  Base = -> Chamfer027 [Edge3,Edge14]
  BaseFeature = -> Chamfer027
  InvalidShape = false
  NewSolid = false
  Radius = 10
  Refine = true
  SupportTransform = false
  Suppress = false
  TreeRank = 139
  UseAllEdges = false
  ValidateShape = true
FEATURE [PartDesign::Fillet] Fillet026
  AddSubType = 0
  Base = -> Fillet025 [Edge25,Edge5]
  BaseFeature = -> Fillet025
  InvalidShape = false
  NewSolid = false
  Radius = 3
  Refine = true
  SupportTransform = false
  Suppress = false
  TreeRank = 140
  UseAllEdges = false
  ValidateShape = true
FEATURE [PartDesign::Fillet] Fillet027
  AddSubType = 0
  Base = -> Fillet026 [Edge7]
  BaseFeature = -> Fillet026
  InvalidShape = false
  NewSolid = false
  Radius = 40
  Refine = true
  SupportTransform = false
  Suppress = false
  TreeRank = 141
  UseAllEdges = false
  ValidateShape = true
FEATURE [PartDesign::PolarPattern] PolarPattern
  AddSubType = 0
  Angle = 360
  Axis = -> Sketch079 [N_Axis]
  BaseFeature = -> Fillet027
  CopyShape = false
  InvalidShape = false
  NewSolid = false
  Occurrences = 3
  OriginalSubs = -> [Pad047,Chamfer027,Fillet025,Fillet026,Fillet027]
  Originals = -> [Pad047,Chamfer027,Fillet025,Fillet026,Fillet027]
  ParallelTransform = true
  Refine = true
  SubTransform = true
  Suppress = false
  TreeRank = 142
  ValidateShape = true
  _Version = 3
FEATURE [Sketcher::SketchObject] Sketch080
  ArcFitTolerance = 1e-06
  AttachmentSupport = -> [PolarPattern]
  ExternalBSplineMaxDegree = 5
  ExternalBSplineTolerance = 0.0001
  FullyConstrained = true
  InternalTolerance = 1e-06
  InvalidShape = false
  MakeInternals = true
  MapMode = 5
  Placement = pos=(0,0,21) rot=(0,0,1;0rad)
  Support = -> [PolarPattern]
  TreeRank = 143
  ValidateShape = true
  sketch-geometry (1):
    g0: Circle CenterX=0 CenterY=60 CenterZ=0 NormalX=0 NormalY=0 NormalZ=1 AngleXU=0 Radius=2.2
  constraints (3):
    c: PointOnObject(g0,g-2)
    c: Diameter(g0) = 4.4
    c: DistanceY(g-1,g0) = 60
FEATURE [PartDesign::Pocket] Pocket035
  AddSubType = 1
  AutoTaperInnerAngle = true
  BaseFeature = -> PolarPattern
  CheckUpToFaceLimits = true
  ClaimChildren = false
  Direction = (1,1,1)
  Fit = 0
  FitJoin = 0
  InnerFit = 0
  InnerFitJoin = 0
  InvalidShape = false
  Length = 5
  Length2 = 100
  Linearize = true
  NewSolid = false
  Profile = -> Sketch080
  Refine = true
  Suppress = false
  TaperInnerAngle = 0
  TaperInnerAngleRev = 0
  TreeRank = 144
  Type = 1
  ValidateShape = true
  _ProfileBasedVersion = 1
  _Version = 1
FEATURE [PartDesign::PolarPattern] PolarPattern016
  AddSubType = 0
  Angle = 360
  Axis = -> Sketch080 [N_Axis]
  BaseFeature = -> Pocket035
  CopyShape = false
  InvalidShape = false
  NewSolid = false
  Occurrences = 3
  OriginalSubs = -> [Pocket035]
  Originals = -> [Pocket035]
  ParallelTransform = true
  Refine = true
  SubTransform = true
  Suppress = false
  TreeRank = 145
  ValidateShape = true
  _Version = 3
FEATURE [PartDesign::Chamfer] Chamfer028
  AddSubType = 0
  Angle = 45
  Base = -> PolarPattern016 [Edge11,Edge114,Edge108]
  BaseFeature = -> PolarPattern016
  ChamferType = 0
  FlipDirection = false
  InvalidShape = false
  NewSolid = false
  Refine = true
  Size = 1
  Size2 = 1
  SupportTransform = false
  Suppress = false
  TreeRank = 146
  UseAllEdges = false
  ValidateShape = true
FEATURE [PartDesign::Chamfer] Chamfer029
  AddSubType = 0
  Angle = 45
  Base = -> Chamfer028 [Face11]
  BaseFeature = -> Chamfer028
  ChamferType = 0
  FlipDirection = false
  InvalidShape = false
  NewSolid = false
  Refine = true
  Size = 0.4
  Size2 = 1
  SupportTransform = false
  Suppress = false
  TreeRank = 147
  UseAllEdges = false
  ValidateShape = true
FEATURE [PartDesign::Body] Body038  label="PlugRobot"
  AutoGroupSolids = false
  ClaimAllChildren = false
  ExportMode = 0
  Group = -> [Sketch074,Pad043,Pad044,Sketch075,Pad045,Import002,Sketch076,Groove,Sketch077,Pocket034,Fillet023,Chamfer025,Fillet024,Chamfer026,Sketch079,Pad047,Chamfer027,Fillet025,Fillet026,Fillet027,PolarPattern,Sketch080,Pocket035,PolarPattern016,Chamfer028,Chamfer029]
  InvalidShape = false
  Origin = -> Origin059
  SingleSolid = true
  Tip = -> Chamfer029
  TreeRank = 104
  ValidateShape = true
  _ExportChildren = -> [Pad043,Pad044,Pad045,Import002,Groove,Pocket034,Fillet023,Chamfer025,Fillet024,Chamfer026,Pad047,Chamfer027,Fillet025,Fillet026,Fillet027,PolarPattern,Pocket035,PolarPattern016,Chamfer028,Chamfer029]
  _GroupVersion = 1
FEATURE [Sketcher::SketchObject] Sketch081
  ArcFitTolerance = 1e-06
  AttachmentSupport = -> [Pad046]
  ExternalBSplineMaxDegree = 5
  ExternalBSplineTolerance = 0.0001
  FullyConstrained = true
  InternalTolerance = 1e-06
  InvalidShape = false
  MakeInternals = true
  MapMode = 5
  Placement = pos=(0,0,24) rot=(0,0,1;0rad)
  Support = -> [Pad046]
  TreeRank = 148
  ValidateShape = true
  sketch-geometry (6):
    g0: LineSegment StartX=-40 StartY=-75 StartZ=0 EndX=-34.2265 EndY=-65 EndZ=0
    g1: ArcOfCircle CenterX=3.0925e-12 CenterY=-211.043 CenterZ=0 NormalX=0 NormalY=0 NormalZ=1 AngleXU=0 Radius=150 StartAngle=1.34059 EndAngle=1.801
    g2: ArcOfCircle CenterX=3.8288e-12 CenterY=2.3123e-12 CenterZ=0 NormalX=0 NormalY=0 NormalZ=1 AngleXU=0 Radius=85 StartAngle=4.22243 EndAngle=5.20235
    g3: LineSegment StartX=34.2265 StartY=-65 StartZ=0 EndX=40 EndY=-75 EndZ=0
    g4: LineSegment [constr] StartX=-40 StartY=-75 StartZ=0 EndX=-8.3276e-12 EndY=-5.71797 EndZ=0
    g5: LineSegment [constr] StartX=-8.3245e-12 StartY=-5.71797 StartZ=0 EndX=40 EndY=-75 EndZ=0
  constraints (18):
    c: PointOnObject(g1,g-2)
    c: Coincident(g1,g0)
    c: Coincident(g2,g-1)
    c: Coincident(g2,g0)
    c: Coincident(g3,g1)
    c: Coincident(g3,g2)
    c: Equal(g3,g0)
    c: Angle(g0,g3) = 1.0472
    c: Diameter(g1) = 300
    c: DistanceY(g0) = -65
    c: Diameter(g2) = 170
    c: Coincident(g4,g0)
    c: PointOnObject(g4,g-2)
    c: Coincident(g5,g4)
    c: Coincident(g5,g2)
    c: PointOnObject(g1,g5)
    c: PointOnObject(g0,g4)
    c: DistanceX(g0,g2) = 80
FEATURE [PartDesign::Pocket] Pocket036
  AddSubType = 1
  AutoTaperInnerAngle = true
  BaseFeature = -> Pad046
  CheckUpToFaceLimits = true
  ClaimChildren = false
  Direction = (1,1,1)
  Fit = 0
  FitJoin = 0
  InnerFit = 0
  InnerFitJoin = 0
  InvalidShape = false
  Length = 5
  Length2 = 100
  Linearize = true
  NewSolid = false
  Profile = -> Sketch081
  Refine = true
  Suppress = false
  TaperInnerAngle = 0
  TaperInnerAngleRev = 0
  TreeRank = 149
  Type = 1
  ValidateShape = true
  _ProfileBasedVersion = 1
  _Version = 1
FEATURE [PartDesign::Fillet] Fillet028
  AddSubType = 0
  Base = -> Pocket036 [Edge25,Edge14,Edge26,Edge13]
  BaseFeature = -> Pocket036
  InvalidShape = false
  NewSolid = false
  Radius = 7
  Refine = true
  SupportTransform = false
  Suppress = false
  TreeRank = 150
  UseAllEdges = false
  ValidateShape = true
FEATURE [PartDesign::PolarPattern] PolarPattern017
  AddSubType = 0
  Angle = 360
  Axis = -> Sketch081 [N_Axis]
  BaseFeature = -> Fillet028
  CopyShape = false
  InvalidShape = false
  NewSolid = false
  Occurrences = 3
  OriginalSubs = -> [Pocket036,Fillet028]
  Originals = -> [Pocket036,Fillet028]
  ParallelTransform = true
  Refine = true
  SubTransform = true
  Suppress = false
  TreeRank = 151
  ValidateShape = true
  _Version = 3
FEATURE [PartDesign::Body] Body039  label="Plate"
  AutoGroupSolids = false
  ClaimAllChildren = false
  ExportMode = 0
  Group = -> [Binder005,Sketch078,Pad046,Sketch081,Pocket036,Fillet028,PolarPattern017]
  InvalidShape = false
  Origin = -> Origin061
  SingleSolid = true
  Tip = -> PolarPattern017
  TreeRank = 132
  ValidateShape = true
  _ExportChildren = -> [Binder005,Pad046,Pocket036,Fillet028,PolarPattern017]
  _GroupVersion = 1
FEATURE [App::Part] Part013  label="RobotStand"
  ClaimAllChildren = false
  ExportMode = 1
  Group = -> [Body038,Body039]
  Origin = -> Origin060
  Placement = pos=(0,1e-15,8) rot=(1,0,0;3.14159rad)
  TreeRank = 122
  _ExportChildren = -> [Body038,Body039]
  _GroupVersion = 1
FEATURE [TechDraw::DrawSVGTemplate] Template008
  Height = 210
  Orientation = 1
  TreeRank = 153
  Width = 297
FEATURE [TechDraw::DrawProjGroupItem] ProjItem012  label="Front013"
  CoarseView = false
  Direction = (0,0,-1)
  Focus = 100
  HardHidden = false
  IsoCount = 0
  IsoHidden = false
  IsoVisible = false
  LockPosition = true
  Perspective = false
  Rotation = 0
  RotationVector = (1,0,0)
  ScaleType = 2
  ScrubCount = 0
  SeamHidden = false
  SeamVisible = true
  SmoothHidden = false
  SmoothVisible = true
  Source = -> [PolarPattern017]
  TreeRank = 156
  Type = 0
  X = 0
  XDirection = (1,0,0)
  Y = 0
FEATURE [TechDraw::DrawProjGroup] ProjGroup012
  Anchor = -> ProjItem012
  AutoDistribute = true
  LockPosition = false
  ProjectionType = 0
  Rotation = 0
  ScaleType = 0
  Source = -> [PolarPattern017]
  TreeRank = 157
  Views = -> [ProjItem012]
  X = 87.444
  Y = 129.768
  spacingX = 15
  spacingY = 15
FEATURE [TechDraw::DrawPage] Page008  label="Maser3mmPlateStandRobot"
  KeepUpdated = true
  NextBalloonIndex = 1
  ProjectionType = 0
  Template = -> Template008
  TreeRank = 154
  Views = -> [ProjGroup012]
FEATURE [Part::SubShapeBinder] Import003  label="Import003(Fillet011)"
  BindCopyOnChange = 0
  BindMode = 0
  ClaimChildren = false
  Context = -> <external ../robot_holonome.FCStd>#Part [Group001.Link.Part014.Body040.Import003.]
  EdgeTolerance = 1e-06
  FillStyle = 0
  FixShape = 1
  Fuse = false
  InvalidShape = false
  MakeFace = false
  MergeEdges = true
  OffsetFill = false
  OffsetIntersection = false
  OffsetJoinType = 0
  OffsetOpenResult = false
  Outline = false
  PartialLoad = false
  Relative = true
  SplitEdges = false
  Support = -> [Body019[Fillet011.]]
  TightBound = false
  TreeRank = 184
  ValidateShape = false
  _Version = 8
FEATURE [Sketcher::SketchObject] Sketch082
  ArcFitTolerance = 1e-06
  AttachmentSupport = -> [XY_Plane049]
  ExternalBSplineMaxDegree = 5
  ExternalBSplineTolerance = 0.0001
  ExternalGeometry = -> [Import003]
  FixShape = 1
  FullyConstrained = true
  InternalTolerance = 1e-06
  InvalidShape = false
  MakeInternals = false
  MapMode = 5
  Support = -> [XY_Plane049]
  TreeRank = 183
  ValidateShape = false
  sketch-geometry (16):
    g0: Circle [constr] CenterX=-78.5391 CenterY=-105.966 CenterZ=0 NormalX=0 NormalY=0 NormalZ=1 AngleXU=0 Radius=6.5
    g1: Circle [constr] CenterX=78.5391 CenterY=-105.966 CenterZ=0 NormalX=0 NormalY=0 NormalZ=1 AngleXU=0 Radius=6.5
    g2: Circle [constr] CenterX=-78.5391 CenterY=-105.966 CenterZ=0 NormalX=0 NormalY=0 NormalZ=1 AngleXU=0 Radius=7.5
    g3: Circle [constr] CenterX=78.5391 CenterY=-105.966 CenterZ=0 NormalX=0 NormalY=0 NormalZ=1 AngleXU=0 Radius=7.5
    g4: Circle CenterX=78.5391 CenterY=-105.966 CenterZ=0 NormalX=0 NormalY=0 NormalZ=1 AngleXU=0 Radius=1.6
    g5: ArcOfCircle CenterX=78.5391 CenterY=-105.966 CenterZ=0 NormalX=0 NormalY=0 NormalZ=1 AngleXU=0 Radius=5 StartAngle=3.65611 EndAngle=5.75959
    g6: Circle CenterX=82.0929 CenterY=-87.8109 CenterZ=0 NormalX=0 NormalY=0 NormalZ=1 AngleXU=0 Radius=4
    g7: Circle CenterX=34.4615 CenterY=-60.3109 CenterZ=0 NormalX=0 NormalY=0 NormalZ=1 AngleXU=0 Radius=5
    g8: Circle CenterX=69.1025 CenterY=-80.3109 CenterZ=0 NormalX=0 NormalY=0 NormalZ=1 AngleXU=0 Radius=5
    g9: Circle CenterX=51.782 CenterY=-70.3109 CenterZ=0 NormalX=0 NormalY=0 NormalZ=1 AngleXU=0 Radius=1.6
    g10: Circle CenterX=25.8013 CenterY=-55.3109 CenterZ=0 NormalX=0 NormalY=0 NormalZ=1 AngleXU=0 Radius=1.6
    g11: ArcOfCircle CenterX=0 CenterY=-150.365 CenterZ=0 NormalX=0 NormalY=0 NormalZ=1 AngleXU=0 Radius=85.2199 StartAngle=0.514518 EndAngle=1.5708
    g12: LineSegment StartX=0 StartY=-65.1451 StartZ=0 EndX=0 EndY=-47.1451 EndZ=0
    g13: LineSegment StartX=0 StartY=-47.1451 StartZ=0 EndX=26.6577 EndY=-47.1451 EndZ=0
    g14: LineSegment StartX=26.6577 StartY=-47.1451 StartZ=0 EndX=95.3692 EndY=-86.8157 EndZ=0
    g15: LineSegment StartX=95.3692 StartY=-86.8157 StartZ=0 EndX=82.8692 EndY=-108.466 EndZ=0
  constraints (39):
    c: Symmetric(g0,g1,g-2)
    c: Equal(g1,g0)
    c: Diameter(g1) = 13
    c: Coincident(g2,g0)
    c: Coincident(g3,g1)
    c: Equal(g3,g2)
    c: Diameter(g3) = 15
    c: Tangent(g3,g-3)
    c: Coincident(g4,g1)
    c: Diameter(g4) = 3.2
    c: Coincident(g5,g4)
    c: Radius(g5) = 5
    c: Coincident(g6,g-5)
    c: Diameter(g6) = 8
    c: Coincident(g7,g-8)
    c: Coincident(g8,g-7)
    c: Equal(g8,g7)
    c: Diameter(g8) = 10
    c: Coincident(g9,g-6)
    c: Coincident(g10,g-9)
    c: Equal(g10,g9)
    c: Diameter(g10) = 3.2
    c: PointOnObject(g11,g-2)
    c: PointOnObject(g11,g-2)
    c: Tangent(g11,g5) = 1.5708
    c: Tangent(g11,g-3)
    c: PointOnObject(g12,g11)
    c: PointOnObject(g12,g-2)
    c: Vertical(g12)
    c: Coincident(g12,g13)
    c: Horizontal(g13)
    c: Coincident(g13,g14)
    c: PointOnObject(g14,g-4)
    c: Coincident(g14,g15)
    c: Parallel(g14,g-3)
    c: DistanceY(g12,g12) = 18
    c: PointOnObject(g13,g-10)
    c: Tangent(g5,g15) = 1.5708
    c: PointOnObject(g-4,g15)
FEATURE [PartDesign::Pad] Pad048
  AddSubType = 0
  AlongSketchNormal = false
  AutoTaperInnerAngle = true
  CheckUpToFaceLimits = true
  ClaimChildren = false
  Direction = (0,0,1)
  Fit = 0
  FitJoin = 0
  FixShape = 1
  InnerFit = 0
  InnerFitJoin = 0
  InvalidShape = false
  Length = 3
  Length2 = 10
  Linearize = true
  NewSolid = false
  Profile = -> Sketch082
  ReferenceAxis = -> Sketch082 [N_Axis]
  Refine = true
  Suppress = false
  TaperInnerAngle = 0
  TaperInnerAngleRev = 0
  TreeRank = 185
  Type = 0
  ValidateShape = true
  _ProfileBasedVersion = 1
FEATURE [PartDesign::Fillet] Fillet029
  AddSubType = 0
  Base = -> Pad048 [Edge8]
  BaseFeature = -> Pad048
  FixShape = 1
  InvalidShape = false
  NewSolid = false
  Radius = 11
  Refine = true
  SupportTransform = false
  Suppress = false
  TreeRank = 186
  UseAllEdges = false
  ValidateShape = true
FEATURE [PartDesign::Fillet] Fillet030
  AddSubType = 0
  Base = -> Fillet029 [Edge31]
  BaseFeature = -> Fillet029
  FixShape = 1
  InvalidShape = false
  NewSolid = false
  Radius = 50
  Refine = true
  SupportTransform = false
  Suppress = false
  TreeRank = 187
  UseAllEdges = false
  ValidateShape = true
FEATURE [PartDesign::Mirrored] Mirrored007
  AddSubType = 0
  BaseFeature = -> Fillet030
  CopyShape = false
  FixShape = 1
  InvalidShape = false
  MirrorPlane = -> Fillet030 [Face7]
  NewSolid = false
  OriginalSubs = -> [Pad048,Fillet029,Fillet030]
  Originals = -> [Pad048,Fillet029,Fillet030]
  ParallelTransform = true
  Refine = true
  SubTransform = true
  Suppress = false
  TreeRank = 188
  ValidateShape = true
  _Version = 3
FEATURE [PartDesign::Body] Body040  label="PlaqueRoulement"
  AutoGroupSolids = false
  ClaimAllChildren = false
  ExportMode = 0
  FixShape = 1
  Group = -> [Sketch082,Import003,Pad048,Fillet029,Fillet030,Mirrored007]
  InvalidShape = false
  Origin = -> Origin063
  SingleSolid = true
  Tip = -> Mirrored007
  TreeRank = 170
  ValidateShape = false
  _ExportChildren = -> [Import003,Pad048,Fillet029,Fillet030,Mirrored007]
  _GroupVersion = 1
FEATURE [App::Link] Link076  label="Link076(633ZZ)"
  AutoLinkLabel = true
  AutoPlacement = true
  LinkPlacement = pos=(78.546,-105.963,3.00002) rot=(-1,0,0;0rad)
  LinkedObject = -> <external generic-hardware.FCStd>#Part035
  Placement = pos=(78.546,-105.963,3.00002) rot=(-1,0,0;0rad)
  SyncGroupVisibility = false
  TreeRank = 189
  _LinkVersion = 1
FEATURE [App::Link] Link077  label="Link077(*633ZZ)"
  AutoLinkLabel = true
  AutoPlacement = true
  LinkPlacement = pos=(-78.54,-105.97,3.00002) rot=(-1,0,0;0rad)
  LinkedObject = -> Link076
  Placement = pos=(-78.54,-105.97,3.00002) rot=(-1,0,0;0rad)
  SyncGroupVisibility = false
  TreeRank = 190
  _LinkVersion = 1
FEATURE [App::Part] Part014  label="EnsembleRoulementActionneur"
  ClaimAllChildren = false
  ExportMode = 1
  Group = -> [Link077,Link076,Body040]
  Origin = -> Origin062
  Placement = pos=(0,0,-8) rot=(0,0,1;0rad)
  TreeRank = 160
  _ExportChildren = -> [Link077,Link076,Body040]
  _GroupVersion = 1
FEATURE [App::Link] Link078  label="Link078(EnsembleRoulementActionneur)"
  AutoLinkLabel = true
  AutoPlacement = true
  LinkPlacement = pos=(0,0,-8) rot=(0,0,1;4.18879rad)
  LinkedObject = -> Part014
  Placement = pos=(0,0,-8) rot=(0,0,1;4.18879rad)
  SyncGroupVisibility = false
  TreeRank = 191
  _LinkVersion = 1
FEATURE [App::Link] Link079  label="Link079(*EnsembleRoulementActionneur)"
  AutoLinkLabel = true
  AutoPlacement = true
  LinkPlacement = pos=(0,0,-8) rot=(0,0,1;2.0944rad)
  LinkedObject = -> Link078
  Placement = pos=(0,0,-8) rot=(0,0,1;2.0944rad)
  SyncGroupVisibility = false
  TreeRank = 192
  _LinkVersion = 1
FEATURE [App::Part] Part007  label="EnsembleSemelle"
  ClaimAllChildren = false
  ExportMode = 1
  Group = -> [Body019,Body020,Link068,Link069,Link070,Link071,Link072,Link073,Group003,Group004,Screw004,Screw008,Screw005,Screw006,Screw007,Screw009,Nut,Nut001,Nut002,Nut003,Nut004,Nut005,Part014,Link078,Link079]
  Origin = -> Origin039
  TreeRank = 0
  _ExportChildren = -> [Body019,Body020,Group003,Group004,Part014,Link078,Link079]
  _GroupVersion = 1
FEATURE [App::DocumentObjectGroup] Group002  label="Parts"
  ClaimAllChildren = true
  ExportMode = 1
  Group = -> [Part,Part007,Body024,Part004,Part005,Part008,Part009,Part006,Part010,Body029,Part011,Part012,Part013]
  TreeRank = 0
  _GroupVersion = 1
FEATURE [TechDraw::DrawProjGroupItem] ProjItem010  label="Front011"
  CoarseView = false
  Direction = (0,0,1)
  Focus = 100
  HardHidden = false
  IsoCount = 0
  IsoHidden = false
  IsoVisible = false
  LockPosition = true
  Perspective = false
  Rotation = 0
  RotationVector = (1,0,0)
  Scale = 0.5
  ScaleType = 2
  ScrubCount = 0
  SeamHidden = false
  SeamVisible = true
  SmoothHidden = false
  SmoothVisible = true
  Source = -> [Part007]
  TreeRank = 71
  Type = 0
  X = 0
  XDirection = (1,0,0)
  Y = 0
FEATURE [TechDraw::DrawProjGroup] ProjGroup010
  Anchor = -> ProjItem010
  AutoDistribute = true
  LockPosition = false
  ProjectionType = 0
  Rotation = 0
  Scale = 0.5
  ScaleType = 2
  Source = -> [Part007]
  TreeRank = 72
  Views = -> [ProjItem010]
  X = 148.5
  Y = 105
  spacingX = 15
  spacingY = 15
FEATURE [TechDraw::DrawViewDimension] Dimension001
  AngleOverride = false
  Arbitrary = false
  ArbitraryTolerances = false
  EqualTolerance = true
  ExtensionAngle = 0
  FormatSpec = %.2f
  FormatSpecOverTolerance = %+.2f
  FormatSpecUnderTolerance = %+.2f
  Inverted = false
  LineAngle = 0
  LockPosition = false
  MeasureType = 1
  OverTolerance = 0
  References2D = -> [ProjItem010]
  Rotation = 0
  ScaleType = 0
  TheoreticalExact = false
  TreeRank = 74
  Type = 2
  UnderTolerance = 0
  X = -105.201
  Y = 7.2116
FEATURE [TechDraw::DrawViewDimension] Dimension
  AngleOverride = false
  Arbitrary = false
  ArbitraryTolerances = false
  EqualTolerance = true
  ExtensionAngle = 0
  FormatSpec = %.2f
  FormatSpecOverTolerance = %+.2f
  FormatSpecUnderTolerance = %+.2f
  Inverted = false
  LineAngle = 0
  LockPosition = false
  MeasureType = 1
  OverTolerance = 0
  References2D = -> [ProjItem010]
  Rotation = 0
  ScaleType = 0
  TheoreticalExact = false
  TreeRank = 75
  Type = 2
  UnderTolerance = 0
  X = -120.317
  Y = 3.82914
FEATURE [TechDraw::DrawViewDimension] Dimension002
  AngleOverride = false
  Arbitrary = false
  ArbitraryTolerances = false
  EqualTolerance = true
  ExtensionAngle = 0
  FormatSpec = %.2f
  FormatSpecOverTolerance = %+.2f
  FormatSpecUnderTolerance = %+.2f
  Inverted = false
  LineAngle = 0
  LockPosition = false
  MeasureType = 1
  OverTolerance = 0
  References2D = -> [ProjItem010]
  Rotation = 0
  ScaleType = 0
  TheoreticalExact = false
  TreeRank = 76
  Type = 2
  UnderTolerance = 0
  X = -88.6226
  Y = -26.0434
FEATURE [TechDraw::DrawViewDimension] Dimension003
  AngleOverride = false
  Arbitrary = false
  ArbitraryTolerances = false
  EqualTolerance = true
  ExtensionAngle = 0
  FormatSpec = %.2f
  FormatSpecOverTolerance = %+.2f
  FormatSpecUnderTolerance = %+.2f
  Inverted = false
  LineAngle = 0
  LockPosition = false
  MeasureType = 1
  OverTolerance = 0
  References2D = -> [ProjItem010]
  Rotation = 0
  ScaleType = 0
  TheoreticalExact = false
  TreeRank = 77
  Type = 2
  UnderTolerance = 0
  X = -88.471
  Y = 25.2924
FEATURE [TechDraw::DrawViewDimension] Dimension004
  AngleOverride = false
  Arbitrary = false
  ArbitraryTolerances = false
  EqualTolerance = true
  ExtensionAngle = 0
  FormatSpec = %.2f
  FormatSpecOverTolerance = %+.2f
  FormatSpecUnderTolerance = %+.2f
  Inverted = false
  LineAngle = 0
  LockPosition = false
  MeasureType = 1
  OverTolerance = 0
  References2D = -> [ProjItem010]
  Rotation = 0
  ScaleType = 0
  TheoreticalExact = false
  TreeRank = 78
  Type = 2
  UnderTolerance = 0
  X = 80.7437
  Y = -25.2392
FEATURE [TechDraw::DrawPage] Page006  label="PlanSemelle"
  KeepUpdated = true
  NextBalloonIndex = 1
  ProjectionType = 0
  Template = -> Template006
  TreeRank = 69
  Views = -> [ProjGroup010,Dimension001,Dimension,Dimension002,Dimension003,Dimension004]
FEATURE [App::DocumentObjectGroup] Group005  label="Plans"
  ClaimAllChildren = true
  ExportMode = 1
  Group = -> [Page006]
  TreeRank = 66
  _GroupVersion = 1
FEATURE [TechDraw::DrawSVGTemplate] Template009
  Height = 210
  Orientation = 1
  Template = <path>
  TreeRank = 194
  Width = 297
FEATURE [TechDraw::DrawProjGroupItem] ProjItem013  label="Front014"
  CoarseView = false
  Direction = (0,0,-1)
  Focus = 100
  HardHidden = false
  IsoCount = 0
  IsoHidden = false
  IsoVisible = false
  LockPosition = true
  Perspective = false
  Rotation = 0
  RotationVector = (-0.5,-0.866,0)
  ScaleType = 2
  ScrubCount = 0
  SeamHidden = false
  SeamVisible = false
  SmoothHidden = false
  SmoothVisible = false
  Source = -> [Mirrored007]
  TreeRank = 197
  Type = 0
  X = 0
  XDirection = (-0.5,-0.866,0)
  Y = 0
FEATURE [TechDraw::DrawProjGroup] ProjGroup013
  Anchor = -> ProjItem013
  AutoDistribute = true
  LockPosition = false
  ProjectionType = 0
  Rotation = 0
  ScaleType = 0
  Source = -> [Mirrored007]
  TreeRank = 198
  Views = -> [ProjItem013]
  X = 89.3237
  Y = 109.634
  spacingX = 15
  spacingY = 15
FEATURE [TechDraw::DrawProjGroupItem] ProjItem014  label="Front015"
  CoarseView = false
  Direction = (0,0,-1)
  Focus = 100
  HardHidden = false
  IsoCount = 0
  IsoHidden = false
  IsoVisible = false
  LockPosition = true
  Perspective = false
  Rotation = 0
  RotationVector = (-0.5,-0.866,0)
  ScaleType = 2
  ScrubCount = 0
  SeamHidden = false
  SeamVisible = false
  SmoothHidden = false
  SmoothVisible = false
  Source = -> [Mirrored007]
  TreeRank = 200
  Type = 0
  X = 0
  XDirection = (-0.5,-0.866,0)
  Y = 0
FEATURE [TechDraw::DrawProjGroup] ProjGroup014
  Anchor = -> ProjItem014
  AutoDistribute = true
  LockPosition = false
  ProjectionType = 0
  Rotation = 0
  ScaleType = 0
  Source = -> [Mirrored007]
  TreeRank = 201
  Views = -> [ProjItem014]
  X = 56.5271
  Y = 128.171
  spacingX = 15
  spacingY = 15
FEATURE [TechDraw::DrawPage] Page009  label="Laser3mm-PlaqueRoulement"
  KeepUpdated = true
  NextBalloonIndex = 1
  ProjectionType = 0
  Template = -> Template009
  TreeRank = 195
  Views = -> [ProjGroup013,ProjGroup014]
FEATURE [App::DocumentObjectGroup] Group  label="Laser"
  ClaimAllChildren = true
  ExportMode = 1
  Group = -> [Page,Page001,Page002,Page003,Page004,Page005,Page007,Page008,Page009]
  TreeRank = 0
  _GroupVersion = 1
note: 1 file-system path scrubbed to <path> (originals preserved in the JSON sidecar)

RESOLVED EXTERNAL PARTS (link-assembly join: the EXTERNAL_REF files above that resolve inside this repo's crawl, each included once):
---- part ../robot_holonome.FCStd = doc fcstd_26781265d2bc ----
FCSTD DOCUMENT  (FreeCAD 2024.113R14555 (Git shallow))
Label: robot_holonome
License: Creative Commons Attribution-NoDerivatives
LicenseURL: http://creativecommons.org/licenses/by-nd/4.0/
objects: App::Link×13, App::DocumentObjectGroup×4, Sketcher::SketchObject×3, PartDesign::Pad×3, PartDesign::Body×3, App::Part×3, App::VRMLObject×1
note: 18 computed .brp shape members not serialized (recipe doc carries the construction recipe); baked Part::Feature solids carry a one-line shape summary decoded from their .brp
EXTERNAL_REF file=mechanical-parts/structures.FCStd obj=Part007
EXTERNAL_REF file=mechanical-parts/colonne-moteur.FCStd obj=Part005
EXTERNAL_REF file=mechanical-parts/structures.FCStd obj=Body024
EXTERNAL_REF file=mechanical-parts/structures.FCStd obj=Part010
EXTERNAL_REF file=mechanical-parts/structures.FCStd obj=Part011
EXTERNAL_REF file=mechanical-parts/structures.FCStd obj=Part012
EXTERNAL_REF file=electronical-parts/beacon_assembled.FCStd obj=Part
EXTERNAL_REF file=electronical-parts/deplacement-sensor.FCStd obj=Part
EXTERNAL_REF file=electronical-parts/battery-assembled.FCStd obj=Part004
EXTERNAL_REF file=mechanical-parts/colonne-moteur.FCStd obj=Part011
EXTERNAL_REF file=mechanical-parts/colonne-moteur.FCStd obj=Part013

FEATURE [App::Link] Link  label="EnsembleSemelle"
  AutoLinkLabel = true
  AutoPlacement = true
  LinkedObject = -> <external mechanical-parts/structures.FCStd>#Part007
  SyncGroupVisibility = false
  TreeRank = 0
  _LinkVersion = 1
FEATURE [App::Link] Link001  label="ColonneMoteur01"
  AutoLinkLabel = true
  AutoPlacement = true
  LinkPlacement = pos=(0,45,-7.62939e-06) rot=(0,0,1;0rad)
  LinkedObject = -> <external mechanical-parts/colonne-moteur.FCStd>#Part005
  Placement = pos=(0,45,-7.62939e-06) rot=(0,0,1;0rad)
  SyncGroupVisibility = false
  TreeRank = 0
  _LinkVersion = 1
FEATURE [App::Link] Link002  label="ColonneMoteur02"
  AutoLinkLabel = true
  AutoPlacement = true
  LinkPlacement = pos=(-38.9711,-22.5,0) rot=(0,0,1;2.0944rad)
  LinkedObject = -> <external mechanical-parts/colonne-moteur.FCStd>#Part005
  Placement = pos=(-38.9711,-22.5,0) rot=(0,0,1;2.0944rad)
  SyncGroupVisibility = false
  TreeRank = 0
  _LinkVersion = 1
FEATURE [App::Link] Link003  label="ColonneMoteur03"
  AutoLinkLabel = true
  AutoPlacement = true
  LinkPlacement = pos=(38.9711,-22.5,0) rot=(0,0,1;4.18879rad)
  LinkedObject = -> <external mechanical-parts/colonne-moteur.FCStd>#Part005
  Placement = pos=(38.9711,-22.5,0) rot=(0,0,1;4.18879rad)
  SyncGroupVisibility = false
  TreeRank = 0
  _LinkVersion = 1
FEATURE [App::Link] Link004  label="PlaqueIntermediaire"
  AutoLinkLabel = true
  AutoPlacement = true
  LinkPlacement = pos=(0,-1.3113e-05,110) rot=(0,0,1;0rad)
  LinkedObject = -> <external mechanical-parts/structures.FCStd>#Body024
  Placement = pos=(0,-1.3113e-05,110) rot=(0,0,1;0rad)
  SyncGroupVisibility = false
  TreeRank = 0
  _LinkVersion = 1
FEATURE [App::Link] Link009  label="Link009(CoinBAU)"
  AutoLinkLabel = true
  AutoPlacement = true
  LinkPlacement = pos=(0,-3.21865e-05,270) rot=(0,0,1;0rad)
  LinkedObject = -> <external mechanical-parts/structures.FCStd>#Part010
  Placement = pos=(0,-3.21865e-05,270) rot=(0,0,1;0rad)
  SyncGroupVisibility = false
  TreeRank = 0
  _LinkVersion = 1
FEATURE [App::Link] Link010  label="Link010(CoinTirette)"
  AutoLinkLabel = true
  AutoPlacement = true
  LinkPlacement = pos=(-2.78743e-05,1.60933e-05,270) rot=(0,0,1;4.18879rad)
  LinkedObject = -> <external mechanical-parts/structures.FCStd>#Part011
  Placement = pos=(-2.78743e-05,1.60933e-05,270) rot=(0,0,1;4.18879rad)
  SyncGroupVisibility = false
  TreeRank = 0
  _LinkVersion = 1
FEATURE [App::Link] Link011  label="Link011(CoinLogo)"
  AutoLinkLabel = true
  AutoPlacement = true
  LinkPlacement = pos=(2.78743e-05,1.60933e-05,270) rot=(0,0,1;2.0944rad)
  LinkedObject = -> <external mechanical-parts/structures.FCStd>#Part012
  Placement = pos=(2.78743e-05,1.60933e-05,270) rot=(0,0,1;2.0944rad)
  SyncGroupVisibility = false
  TreeRank = 0
  _LinkVersion = 1
FEATURE [App::DocumentObjectGroup] Group001  label="Structure"
  ClaimAllChildren = true
  ExportMode = 1
  Group = -> [Link,Link001,Link003,Link002,Link004,Link009,Link010,Link011]
  TreeRank = 0
  _GroupVersion = 1
FEATURE [App::Link] Link014  label="BeaconAssembled"
  AutoLinkLabel = true
  AutoPlacement = true
  LinkPlacement = pos=(0,-3.8147e-05,320) rot=(0,0,1;0rad)
  LinkedObject = -> <external electronical-parts/beacon_assembled.FCStd>#Part
  Placement = pos=(0,-3.8147e-05,320) rot=(0,0,1;0rad)
  SyncGroupVisibility = false
  TreeRank = 0
  _LinkVersion = 1
FEATURE [App::DocumentObjectGroup] Group003  label="Carters"
  ClaimAllChildren = true
  ExportMode = 1
  TreeRank = 1
  _GroupVersion = 1
FEATURE [Sketcher::SketchObject] Sketch
  ArcFitTolerance = 0
  ExternalBSplineMaxDegree = 0
  ExternalBSplineTolerance = 0
  FullyConstrained = true
  InternalTolerance = 1e-06
  InvalidShape = false
  MakeInternals = false
  MapMode = 2
  TreeRank = 27
  ValidateShape = true
  sketch-geometry (1):
    g0: Circle CenterX=0 CenterY=0 CenterZ=0 NormalX=0 NormalY=0 NormalZ=1 AngleXU=0 Radius=163.134
  constraints (2):
    c: Coincident(g0,g-1)
    c: Diameter(g0) = 326.268
FEATURE [PartDesign::Pad] Pad
  AddSubType = 0
  AlongSketchNormal = false
  AutoTaperInnerAngle = false
  CheckUpToFaceLimits = true
  ClaimChildren = false
  Direction = (0,0,1)
  Fit = 0
  FitJoin = 0
  InnerFit = 0
  InnerFitJoin = 0
  InvalidShape = false
  Length = 350
  Length2 = 100
  Linearize = true
  NewSolid = false
  Profile = -> Sketch
  Refine = true
  Suppress = false
  TaperInnerAngle = 0
  TaperInnerAngleRev = 0
  TreeRank = 28
  Type = 0
  ValidateShape = true
  _ProfileBasedVersion = 1
FEATURE [PartDesign::Body] Body  label="Limite Non Déployé"
  AutoGroupSolids = false
  ClaimAllChildren = false
  ExportMode = 0
  Group = -> [Sketch,Pad]
  InvalidShape = false
  Origin = -> Origin001
  SingleSolid = true
  Tip = -> Pad
  TreeRank = 26
  ValidateShape = true
  _ExportChildren = -> [Pad]
  _GroupVersion = 1
FEATURE [Sketcher::SketchObject] Sketch001
  ArcFitTolerance = 0
  ExternalBSplineMaxDegree = 0
  ExternalBSplineTolerance = 0
  FullyConstrained = true
  InternalTolerance = 1e-06
  InvalidShape = false
  MakeInternals = false
  MapMode = 2
  TreeRank = 39
  ValidateShape = true
  sketch-geometry (1):
    g0: Circle CenterX=0 CenterY=0 CenterZ=0 NormalX=0 NormalY=0 NormalZ=1 AngleXU=0 Radius=175
  constraints (2):
    c: Coincident(g0,g-1)
    c: Diameter(g0) = 350
FEATURE [PartDesign::Pad] Pad001
  AddSubType = 0
  AlongSketchNormal = false
  AutoTaperInnerAngle = false
  CheckUpToFaceLimits = true
  ClaimChildren = false
  Direction = (0,0,1)
  Fit = 0
  FitJoin = 0
  InnerFit = 0
  InnerFitJoin = 0
  InvalidShape = false
  Length = 350
  Length2 = 100
  Linearize = true
  NewSolid = false
  Profile = -> Sketch001
  Refine = true
  Suppress = false
  TaperInnerAngle = 0
  TaperInnerAngleRev = 0
  TreeRank = 40
  Type = 0
  ValidateShape = true
  _ProfileBasedVersion = 1
FEATURE [PartDesign::Body] Body001  label="Limite Déployé"
  AutoGroupSolids = false
  ClaimAllChildren = false
  ExportMode = 0
  Group = -> [Sketch001,Pad001]
  InvalidShape = false
  Origin = -> Origin002
  SingleSolid = true
  Tip = -> Pad001
  TreeRank = 38
  ValidateShape = true
  _ExportChildren = -> [Pad001]
  _GroupVersion = 1
FEATURE [Sketcher::SketchObject] Sketch002
  ArcFitTolerance = 0
  ExternalBSplineMaxDegree = 0
  ExternalBSplineTolerance = 0
  FullyConstrained = false
  InternalTolerance = 1e-06
  InvalidShape = false
  MakeInternals = false
  MapMode = 2
  TreeRank = 51
  ValidateShape = true
  sketch-geometry (12):
    g0: LineSegment StartX=-85.2682 StartY=-99.392 StartZ=0 EndX=-14.2583 EndY=-111.375 EndZ=0
    g1: LineSegment StartX=-14.2583 StartY=-111.375 StartZ=0 EndX=-3.60679 EndY=-111.819 EndZ=0
    g2: LineSegment StartX=-3.60679 StartY=-111.819 StartZ=0 EndX=86.9308 EndY=-99.392 EndZ=0
    g3: LineSegment StartX=86.9308 StartY=-99.392 StartZ=0 EndX=114.447 EndY=-65.2184 EndZ=0
    g4: LineSegment StartX=114.447 StartY=-65.2184 StartZ=0 EndX=129.537 EndY=-30.1573 EndZ=0
    g5: LineSegment StartX=129.537 StartY=-30.1573 StartZ=0 EndX=173.666 EndY=49.5134 EndZ=0
    g6: LineSegment StartX=173.666 StartY=49.5134 StartZ=0 EndX=188.302 EndY=115.646 EndZ=0
    g7: LineSegment StartX=188.302 StartY=115.646 StartZ=0 EndX=179.629 EndY=134.077 EndZ=0
    g8: LineSegment StartX=179.629 StartY=134.077 StartZ=0 EndX=57.6393 EndY=125.177 EndZ=0
    g9: LineSegment StartX=57.6393 StartY=125.177 StartZ=0 EndX=-44.4375 EndY=125.177 EndZ=0
    g10: LineSegment StartX=-85.2682 StartY=-99.392 StartZ=0 EndX=-127.43 EndY=-23.5001 EndZ=0
    g11: LineSegment StartX=-127.43 StartY=-23.5001 StartZ=0 EndX=-44.4375 EndY=125.177 EndZ=0
  constraints (13):
    c: Coincident(g0,g1)
    c: Coincident(g1,g2)
    c: Coincident(g2,g3)
    c: Coincident(g3,g4)
    c: Coincident(g4,g5)
    c: Coincident(g5,g6)
    c: Coincident(g6,g7)
    c: Coincident(g7,g8)
    c: Coincident(g8,g9)
    c: Horizontal(g9)
    c: Coincident(g0,g10)
    c: Coincident(g10,g11)
    c: Coincident(g11,g9)
FEATURE [PartDesign::Pad] Pad002
  AddSubType = 0
  AlongSketchNormal = false
  AutoTaperInnerAngle = false
  CheckUpToFaceLimits = true
  ClaimChildren = false
  Direction = (0,0,1)
  Fit = 0
  FitJoin = 0
  InnerFit = 0
  InnerFitJoin = 0
  InvalidShape = false
  Length = 350
  Length2 = 100
  Linearize = true
  NewSolid = false
  Profile = -> Sketch002
  Refine = true
  Suppress = false
  TaperInnerAngle = 0
  TaperInnerAngleRev = 0
  TreeRank = 52
  Type = 0
  ValidateShape = true
  _ProfileBasedVersion = 1
FEATURE [PartDesign::Body] Body002  label="Perimètre Déployé"
  AutoGroupSolids = false
  ClaimAllChildren = false
  ExportMode = 0
  Group = -> [Sketch002,Pad002]
  InvalidShape = false
  Origin = -> Origin003
  SingleSolid = true
  Tip = -> Pad002
  TreeRank = 50
  ValidateShape = true
  _ExportChildren = -> [Pad002]
  _GroupVersion = 1
FEATURE [App::DocumentObjectGroup] Group004  label="Périmètres"
  ClaimAllChildren = true
  ExportMode = 1
  Group = -> [Body001,Body,Body002]
  TreeRank = 53
  _GroupVersion = 1
FEATURE [App::Link] Link039  label="SensorDeplacement-assembled"
  AutoLinkLabel = true
  AutoPlacement = true
  LinkPlacement = pos=(-2.51e-14,5.96047e-07,-5) rot=(0,0,1;3.14159rad)
  LinkedObject = -> <external electronical-parts/deplacement-sensor.FCStd>#Part
  Placement = pos=(-2.51e-14,5.96047e-07,-5) rot=(0,0,1;3.14159rad)
  SyncGroupVisibility = false
  TreeRank = 146
  _LinkVersion = 1
FEATURE [App::Link] Link041  label="LogementBatterie - 2024"
  AutoLinkLabel = true
  AutoPlacement = true
  LinkPlacement = pos=(0,120,156) rot=(0,0,1;0rad)
  LinkedObject = -> <external electronical-parts/battery-assembled.FCStd>#Part004
  Placement = pos=(0,120,156) rot=(0,0,1;0rad)
  SyncGroupVisibility = false
  TreeRank = 148
  _LinkVersion = 1
FEATURE [App::Link] Link043  label="EnsembleCarterIHM-V2"
  AutoLinkLabel = true
  AutoPlacement = true
  LinkPlacement = pos=(0,45,0) rot=(0,0,1;0rad)
  LinkedObject = -> <external mechanical-parts/colonne-moteur.FCStd>#Part011
  Placement = pos=(0,45,0) rot=(0,0,1;0rad)
  SyncGroupVisibility = false
  TreeRank = 183
  _LinkVersion = 1
FEATURE [App::VRMLObject] mainBoard_2024001  label="mainBoard-2024"
  Resources = mainBoard_2024001/ | mainBoard_2024001/ | mainBoard_2024001/ | mainBoard_2024001/ | mainBoard_2024001/ | mainBoard_2024001/ | mainBoard_2024001/ | mainBoard_2024001/ | mainBoard_2024001/ | mainBoard_2024001/ | mainBoard_2024001/ | mainBoard_2024001/ | mainBoard_2024001/ | mainBoard_2024001/ | mainBoard_2024001/ | mainBoard_2024001/ | mainBoard_2024001/ | mainBoard_2024001/ | mainBoard_2024001/ | mainBoard_2024001/
  TreeRank = 185
FEATURE [App::Part] Part005  label="MainBoard - 2024"
  ClaimAllChildren = false
  ExportMode = 1
  Group = -> [mainBoard_2024001]
  Origin = -> Origin010
  Placement = pos=(-19,87,262) rot=(-0.57735,0.57735,0.57735;4.18879rad)
  TreeRank = 155
  _ExportChildren = -> [mainBoard_2024001]
  _GroupVersion = 1
FEATURE [App::Part] Part004  label="EnsembleMainBoard - 2024"
  ClaimAllChildren = false
  ExportMode = 1
  Group = -> [Part005]
  Origin = -> Origin009
  TreeRank = 151
  _ExportChildren = -> [Part005]
  _GroupVersion = 1
FEATURE [App::Link] Link044  label="EnsembleTFTCarter"
  AutoLinkLabel = true
  AutoPlacement = true
  LinkPlacement = pos=(0,45,0) rot=(0,0,1;0rad)
  LinkedObject = -> <external mechanical-parts/colonne-moteur.FCStd>#Part013
  Placement = pos=(0,45,0) rot=(0,0,1;0rad)
  SyncGroupVisibility = false
  TreeRank = 186
  _LinkVersion = 1
FEATURE [App::DocumentObjectGroup] Group002  label="Electronique"
  ClaimAllChildren = true
  ExportMode = 1
  Group = -> [Link014,Link041,Part004,Link043,Link044]
  TreeRank = 0
  _GroupVersion = 1
FEATURE [App::Part] Part  label="RobotHolonome"
  ClaimAllChildren = false
  ExportMode = 1
  Group = -> [Group001,Group002,Link,Link001,Link003,Link002,Link004,Link009,Link010,Link011,Link014,Group003,Group004,Body001,Body002,Body,Link039,Link041,Part004,Link043,Link044]
  Origin = -> Origin
  TreeRank = 0
  _ExportChildren = -> [Group001,Group002,Group003,Group004,Link039]
  _GroupVersion = 1
---- part generic-hardware.FCStd = doc fcstd_3cd127f5b444 (208677 chars; too large to inline — full recipe in that document) ----
